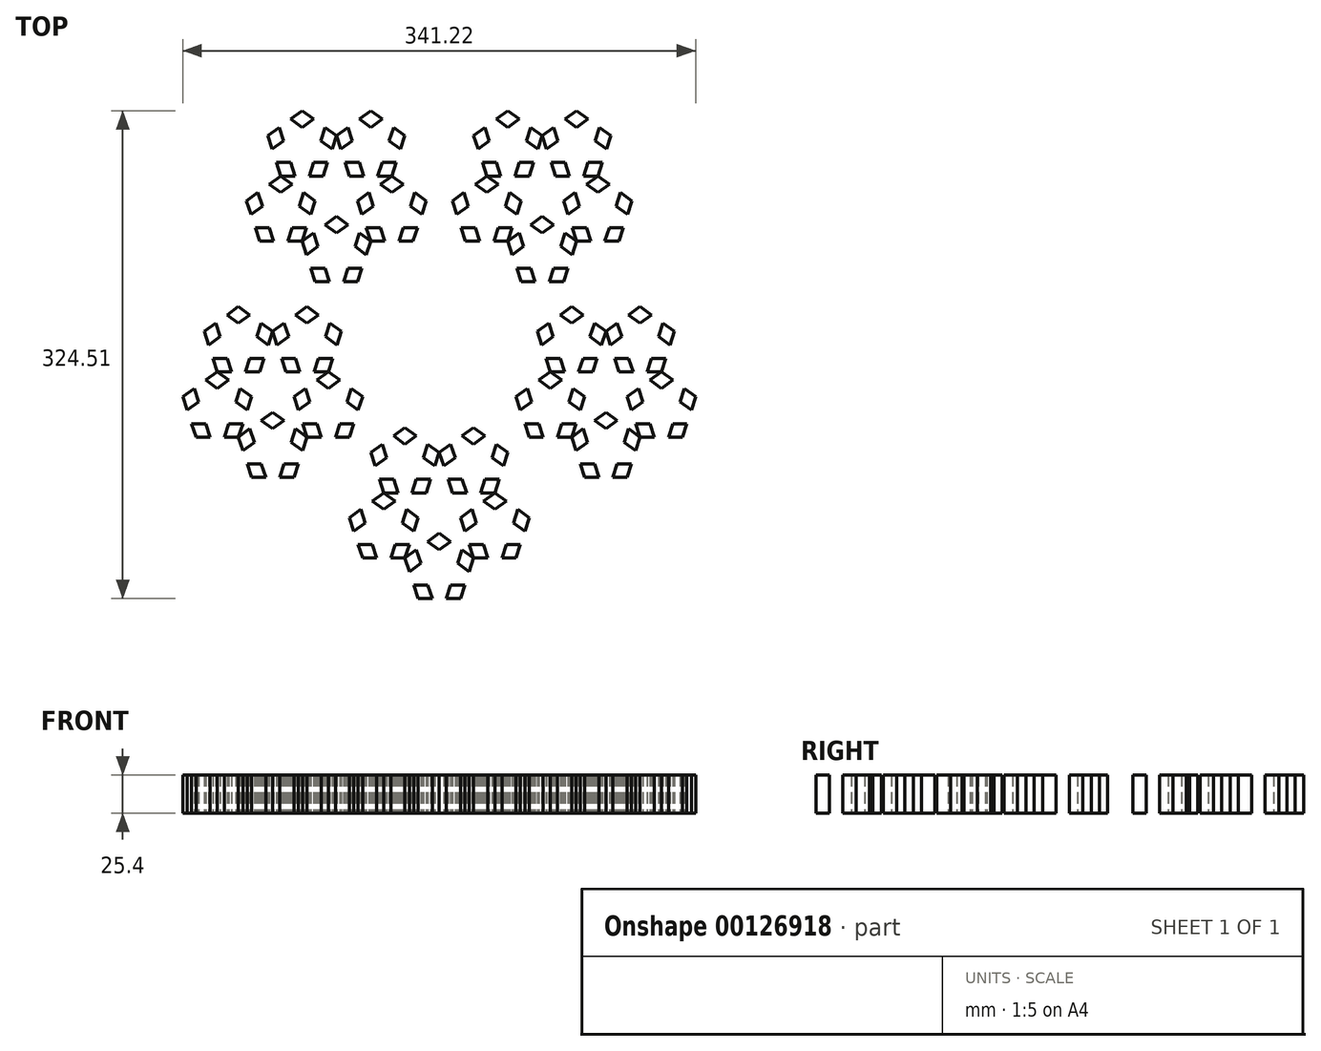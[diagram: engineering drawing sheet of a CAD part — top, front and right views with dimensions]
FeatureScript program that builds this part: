
annotation { "Feature Type Name" : "Feature", "Feature Type Description" : "" }
export const myFeature = defineFeature(function(context is Context, id is Id, definition is map)
    precondition{}
    {
        {
            var Q0;
            Q0=qCreatedBy(makeId("Top.planeOp"),FACE);
            var sketch = newSketch(context, id + "F0", { "sketchPlane" : qUnion([Q0])});
            skLineSegment(sketch, "E0.0", {"start": v(127, -174.8) * mm, "end": v(-127, -174.8) * mm});
            skLineSegment(sketch, "E0.1", {"start": v(-127, -174.8) * mm, "end": v(-205.5, 66.77) * mm});
            skLineSegment(sketch, "E0.2", {"start": v(-205.5, 66.77) * mm, "end": v(0, 216.07) * mm});
            skLineSegment(sketch, "E0.3", {"start": v(0, 216.07) * mm, "end": v(205.5, 66.77) * mm});
            skLineSegment(sketch, "E0.4", {"start": v(205.5, 66.77) * mm, "end": v(127, -174.8) * mm});
            skPoint(sketch, "E0.0.midPoint", {"position": v(0, -174.8) * mm});
            skLineSegment(sketch, "E1.0", {"start": v(42.33, -174.8) * mm, "end": v(-42.33, -174.8) * mm});
            skLineSegment(sketch, "E1.1", {"start": v(-42.33, -174.8) * mm, "end": v(-68.5, -94.28) * mm});
            skLineSegment(sketch, "E1.2", {"start": v(-68.5, -94.28) * mm, "end": v(0, -44.51) * mm});
            skLineSegment(sketch, "E1.3", {"start": v(0, -44.51) * mm, "end": v(68.5, -94.28) * mm});
            skLineSegment(sketch, "E1.4", {"start": v(68.5, -94.28) * mm, "end": v(42.33, -174.8) * mm});
            skLineSegment(sketch, "E2.0", {"start": v(14.11, -174.8) * mm, "end": v(-14.11, -174.8) * mm});
            skLineSegment(sketch, "E2.1", {"start": v(-14.11, -174.8) * mm, "end": v(-22.83, -147.96) * mm});
            skLineSegment(sketch, "E2.2", {"start": v(-22.83, -147.96) * mm, "end": v(0, -131.37) * mm});
            skLineSegment(sketch, "E2.3", {"start": v(0, -131.37) * mm, "end": v(22.83, -147.96) * mm});
            skLineSegment(sketch, "E2.4", {"start": v(22.83, -147.96) * mm, "end": v(14.11, -174.8) * mm});
            skLineSegment(sketch, "E3.0", {"start": v(4.7, -174.8) * mm, "end": v(-4.7, -174.8) * mm});
            skLineSegment(sketch, "E3.1", {"start": v(-4.7, -174.8) * mm, "end": v(-7.61, -165.85) * mm});
            skLineSegment(sketch, "E3.2", {"start": v(-7.61, -165.85) * mm, "end": v(0, -160.32) * mm});
            skLineSegment(sketch, "E3.3", {"start": v(0, -160.32) * mm, "end": v(7.61, -165.85) * mm});
            skLineSegment(sketch, "E3.4", {"start": v(7.61, -165.85) * mm, "end": v(4.7, -174.8) * mm});
            skLineSegment(sketch, "E4.1.0", {"start": v(4.7, -156.9) * mm, "end": v(12.31, -151.38) * mm});
            skLineSegment(sketch, "E4.1.1", {"start": v(19.93, -156.9) * mm, "end": v(17.02, -165.85) * mm});
            skPoint(sketch, "E4.1.2", {"position": v(18.47, -161.38) * mm});
            skLineSegment(sketch, "E4.1.3", {"start": v(17.02, -165.85) * mm, "end": v(7.61, -165.85) * mm});
            skLineSegment(sketch, "E4.1.4", {"start": v(12.31, -151.38) * mm, "end": v(19.93, -156.9) * mm});
            skLineSegment(sketch, "E4.1.5", {"start": v(7.61, -165.85) * mm, "end": v(4.7, -156.9) * mm});
            skPoint(sketch, "E4.1.6", {"position": v(18.47, -161.38) * mm});
            skPoint(sketch, "E4.1.7", {"position": v(18.47, -161.38) * mm});
            skPoint(sketch, "E4.1.8", {"position": v(18.47, -161.38) * mm});
            skLineSegment(sketch, "E4.2.0", {"start": v(2.9, -151.38) * mm, "end": v(0, -142.43) * mm});
            skLineSegment(sketch, "E4.2.1", {"start": v(7.61, -136.9) * mm, "end": v(15.22, -142.43) * mm});
            skPoint(sketch, "E4.2.2", {"position": v(11.42, -139.67) * mm});
            skLineSegment(sketch, "E4.2.3", {"start": v(15.22, -142.43) * mm, "end": v(12.31, -151.38) * mm});
            skLineSegment(sketch, "E4.2.4", {"start": v(0, -142.43) * mm, "end": v(7.61, -136.9) * mm});
            skLineSegment(sketch, "E4.2.5", {"start": v(12.31, -151.38) * mm, "end": v(2.9, -151.38) * mm});
            skPoint(sketch, "E4.2.6", {"position": v(11.42, -139.67) * mm});
            skPoint(sketch, "E4.2.7", {"position": v(11.42, -139.67) * mm});
            skPoint(sketch, "E4.2.8", {"position": v(11.42, -139.67) * mm});
            skLineSegment(sketch, "E4.3.0", {"start": v(-2.9, -151.38) * mm, "end": v(-12.31, -151.38) * mm});
            skLineSegment(sketch, "E4.3.1", {"start": v(-15.22, -142.43) * mm, "end": v(-7.61, -136.9) * mm});
            skPoint(sketch, "E4.3.2", {"position": v(-11.42, -139.67) * mm});
            skLineSegment(sketch, "E4.3.3", {"start": v(-7.61, -136.9) * mm, "end": v(0, -142.43) * mm});
            skLineSegment(sketch, "E4.3.4", {"start": v(-12.31, -151.38) * mm, "end": v(-15.22, -142.43) * mm});
            skLineSegment(sketch, "E4.3.5", {"start": v(0, -142.43) * mm, "end": v(-2.9, -151.38) * mm});
            skPoint(sketch, "E4.3.6", {"position": v(-11.42, -139.67) * mm});
            skPoint(sketch, "E4.3.7", {"position": v(-11.42, -139.67) * mm});
            skPoint(sketch, "E4.3.8", {"position": v(-11.42, -139.67) * mm});
            skLineSegment(sketch, "E4.4.0", {"start": v(-4.7, -156.9) * mm, "end": v(-7.61, -165.85) * mm});
            skLineSegment(sketch, "E4.4.1", {"start": v(-17.02, -165.85) * mm, "end": v(-19.93, -156.9) * mm});
            skPoint(sketch, "E4.4.2", {"position": v(-18.47, -161.38) * mm});
            skLineSegment(sketch, "E4.4.3", {"start": v(-19.93, -156.9) * mm, "end": v(-12.31, -151.38) * mm});
            skLineSegment(sketch, "E4.4.4", {"start": v(-7.61, -165.85) * mm, "end": v(-17.02, -165.85) * mm});
            skLineSegment(sketch, "E4.4.5", {"start": v(-12.31, -151.38) * mm, "end": v(-4.7, -156.9) * mm});
            skPoint(sketch, "E4.4.6", {"position": v(-18.47, -161.38) * mm});
            skPoint(sketch, "E4.4.7", {"position": v(-18.47, -161.38) * mm});
            skPoint(sketch, "E4.4.8", {"position": v(-18.47, -161.38) * mm});
            skPoint(sketch, "E4.center", {"position": v(0, -155.38) * mm});
            skLineSegment(sketch, "E5.1.0", {"start": v(34.04, -124.54) * mm, "end": v(24.63, -124.54) * mm});
            skLineSegment(sketch, "E5.1.1", {"start": v(44.55, -139.01) * mm, "end": v(41.65, -147.96) * mm});
            skLineSegment(sketch, "E5.1.2", {"start": v(52.16, -115.59) * mm, "end": v(49.26, -124.54) * mm});
            skLineSegment(sketch, "E5.1.3", {"start": v(24.63, -124.54) * mm, "end": v(32.24, -130.07) * mm});
            skLineSegment(sketch, "E5.1.4", {"start": v(41.65, -130.07) * mm, "end": v(49.26, -124.54) * mm});
            skLineSegment(sketch, "E5.1.5", {"start": v(32.24, -130.07) * mm, "end": v(29.33, -139.01) * mm});
            skLineSegment(sketch, "E5.1.6", {"start": v(36.94, -104.53) * mm, "end": v(59.78, -121.12) * mm});
            skLineSegment(sketch, "E5.1.7", {"start": v(39.85, -124.54) * mm, "end": v(36.94, -115.59) * mm});
            skLineSegment(sketch, "E5.1.8", {"start": v(29.33, -139.01) * mm, "end": v(36.94, -133.48) * mm});
            skPoint(sketch, "E5.1.9", {"position": v(18.47, -134.54) * mm});
            skPoint(sketch, "E5.1.10", {"position": v(48.36, -112.82) * mm});
            skPoint(sketch, "E5.1.11", {"position": v(55.42, -134.54) * mm});
            skLineSegment(sketch, "E5.1.12", {"start": v(53.96, -139.01) * mm, "end": v(44.55, -139.01) * mm});
            skLineSegment(sketch, "E5.1.13", {"start": v(22.83, -147.96) * mm, "end": v(14.11, -121.12) * mm});
            skLineSegment(sketch, "E5.1.14", {"start": v(29.33, -139.01) * mm, "end": v(19.93, -139.01) * mm});
            skLineSegment(sketch, "E5.1.15", {"start": v(14.11, -121.12) * mm, "end": v(36.94, -104.53) * mm});
            skLineSegment(sketch, "E5.1.16", {"start": v(36.94, -133.48) * mm, "end": v(44.55, -139.01) * mm});
            skLineSegment(sketch, "E5.1.17", {"start": v(59.78, -121.12) * mm, "end": v(51.05, -147.96) * mm});
            skLineSegment(sketch, "E5.1.18", {"start": v(56.87, -130.07) * mm, "end": v(53.96, -139.01) * mm});
            skLineSegment(sketch, "E5.1.19", {"start": v(24.63, -124.54) * mm, "end": v(21.72, -115.59) * mm});
            skLineSegment(sketch, "E5.1.20", {"start": v(44.55, -110.06) * mm, "end": v(52.16, -115.59) * mm});
            skLineSegment(sketch, "E5.1.21", {"start": v(17.02, -130.07) * mm, "end": v(24.63, -124.54) * mm});
            skPoint(sketch, "E5.1.22", {"position": v(36.94, -128.54) * mm});
            skLineSegment(sketch, "E5.1.23", {"start": v(36.94, -115.59) * mm, "end": v(34.04, -124.54) * mm});
            skLineSegment(sketch, "E5.1.24", {"start": v(44.55, -139.01) * mm, "end": v(41.65, -130.07) * mm});
            skLineSegment(sketch, "E5.1.25", {"start": v(49.26, -124.54) * mm, "end": v(56.87, -130.07) * mm});
            skLineSegment(sketch, "E5.1.26", {"start": v(29.33, -110.06) * mm, "end": v(36.94, -115.59) * mm});
            skLineSegment(sketch, "E5.1.27", {"start": v(36.94, -115.59) * mm, "end": v(44.55, -110.06) * mm});
            skPoint(sketch, "E5.1.28", {"position": v(36.94, -147.96) * mm});
            skLineSegment(sketch, "E5.1.29", {"start": v(32.24, -147.96) * mm, "end": v(29.33, -139.01) * mm});
            skLineSegment(sketch, "E5.1.30", {"start": v(51.05, -147.96) * mm, "end": v(22.83, -147.96) * mm});
            skPoint(sketch, "E5.1.31", {"position": v(25.53, -112.82) * mm});
            skLineSegment(sketch, "E5.1.32", {"start": v(49.26, -124.54) * mm, "end": v(39.85, -124.54) * mm});
            skPoint(sketch, "E5.1.33", {"position": v(48.36, -112.82) * mm});
            skPoint(sketch, "E5.1.34", {"position": v(36.94, -147.96) * mm});
            skPoint(sketch, "E5.1.35", {"position": v(55.42, -134.54) * mm});
            skPoint(sketch, "E5.1.36", {"position": v(18.47, -134.54) * mm});
            skLineSegment(sketch, "E5.1.37", {"start": v(41.65, -147.96) * mm, "end": v(32.24, -147.96) * mm});
            skPoint(sketch, "E5.1.38", {"position": v(25.53, -112.82) * mm});
            skPoint(sketch, "E5.1.39", {"position": v(48.36, -112.82) * mm});
            skPoint(sketch, "E5.1.40", {"position": v(18.47, -134.54) * mm});
            skPoint(sketch, "E5.1.41", {"position": v(25.53, -112.82) * mm});
            skLineSegment(sketch, "E5.1.42", {"start": v(21.72, -115.59) * mm, "end": v(29.33, -110.06) * mm});
            skLineSegment(sketch, "E5.1.43", {"start": v(19.93, -139.01) * mm, "end": v(17.02, -130.07) * mm});
            skPoint(sketch, "E5.1.44", {"position": v(55.42, -134.54) * mm});
            skPoint(sketch, "E5.1.45", {"position": v(36.94, -147.96) * mm});
            skPoint(sketch, "E5.1.46", {"position": v(36.94, -147.96) * mm});
            skPoint(sketch, "E5.1.47", {"position": v(55.42, -134.54) * mm});
            skPoint(sketch, "E5.1.48", {"position": v(25.53, -112.82) * mm});
            skPoint(sketch, "E5.1.49", {"position": v(18.47, -134.54) * mm});
            skPoint(sketch, "E5.1.50", {"position": v(48.36, -112.82) * mm});
            skLineSegment(sketch, "E5.2.0", {"start": v(18.13, -86.64) * mm, "end": v(15.22, -95.58) * mm});
            skLineSegment(sketch, "E5.2.1", {"start": v(35.15, -81.1) * mm, "end": v(42.76, -86.64) * mm});
            skLineSegment(sketch, "E5.2.2", {"start": v(15.22, -66.63) * mm, "end": v(22.83, -72.16) * mm});
            skLineSegment(sketch, "E5.2.3", {"start": v(15.22, -95.58) * mm, "end": v(22.83, -90.05) * mm});
            skLineSegment(sketch, "E5.2.4", {"start": v(25.74, -81.1) * mm, "end": v(22.83, -72.16) * mm});
            skLineSegment(sketch, "E5.2.5", {"start": v(22.83, -90.05) * mm, "end": v(30.44, -95.58) * mm});
            skLineSegment(sketch, "E5.2.6", {"start": v(0, -77.69) * mm, "end": v(22.83, -61.1) * mm});
            skLineSegment(sketch, "E5.2.7", {"start": v(19.93, -81.1) * mm, "end": v(10.52, -81.1) * mm});
            skLineSegment(sketch, "E5.2.8", {"start": v(30.44, -95.58) * mm, "end": v(27.54, -86.64) * mm});
            skPoint(sketch, "E5.2.9", {"position": v(22.83, -104.53) * mm});
            skPoint(sketch, "E5.2.10", {"position": v(11.42, -69.4) * mm});
            skPoint(sketch, "E5.2.11", {"position": v(34.25, -69.4) * mm});
            skLineSegment(sketch, "E5.2.12", {"start": v(38.05, -72.16) * mm, "end": v(35.15, -81.1) * mm});
            skLineSegment(sketch, "E5.2.13", {"start": v(36.94, -104.53) * mm, "end": v(8.72, -104.53) * mm});
            skLineSegment(sketch, "E5.2.14", {"start": v(30.44, -95.58) * mm, "end": v(27.54, -104.53) * mm});
            skLineSegment(sketch, "E5.2.15", {"start": v(8.72, -104.53) * mm, "end": v(0, -77.69) * mm});
            skLineSegment(sketch, "E5.2.16", {"start": v(27.54, -86.64) * mm, "end": v(35.15, -81.1) * mm});
            skLineSegment(sketch, "E5.2.17", {"start": v(22.83, -61.1) * mm, "end": v(45.66, -77.69) * mm});
            skLineSegment(sketch, "E5.2.18", {"start": v(30.44, -66.63) * mm, "end": v(38.05, -72.16) * mm});
            skLineSegment(sketch, "E5.2.19", {"start": v(15.22, -95.58) * mm, "end": v(5.81, -95.58) * mm});
            skLineSegment(sketch, "E5.2.20", {"start": v(7.61, -72.16) * mm, "end": v(15.22, -66.63) * mm});
            skLineSegment(sketch, "E5.2.21", {"start": v(18.13, -104.53) * mm, "end": v(15.22, -95.58) * mm});
            skPoint(sketch, "E5.2.22", {"position": v(22.83, -85.1) * mm});
            skLineSegment(sketch, "E5.2.23", {"start": v(10.52, -81.1) * mm, "end": v(18.13, -86.64) * mm});
            skLineSegment(sketch, "E5.2.24", {"start": v(35.15, -81.1) * mm, "end": v(25.74, -81.1) * mm});
            skLineSegment(sketch, "E5.2.25", {"start": v(22.83, -72.16) * mm, "end": v(30.44, -66.63) * mm});
            skLineSegment(sketch, "E5.2.26", {"start": v(2.9, -86.64) * mm, "end": v(10.52, -81.1) * mm});
            skLineSegment(sketch, "E5.2.27", {"start": v(10.52, -81.1) * mm, "end": v(7.61, -72.16) * mm});
            skPoint(sketch, "E5.2.28", {"position": v(41.3, -91.1) * mm});
            skLineSegment(sketch, "E5.2.29", {"start": v(39.85, -95.58) * mm, "end": v(30.44, -95.58) * mm});
            skLineSegment(sketch, "E5.2.30", {"start": v(45.66, -77.69) * mm, "end": v(36.94, -104.53) * mm});
            skPoint(sketch, "E5.2.31", {"position": v(4.36, -91.1) * mm});
            skLineSegment(sketch, "E5.2.32", {"start": v(22.83, -72.16) * mm, "end": v(19.93, -81.1) * mm});
            skPoint(sketch, "E5.2.33", {"position": v(11.42, -69.4) * mm});
            skPoint(sketch, "E5.2.34", {"position": v(41.3, -91.1) * mm});
            skPoint(sketch, "E5.2.35", {"position": v(34.25, -69.4) * mm});
            skPoint(sketch, "E5.2.36", {"position": v(22.83, -104.53) * mm});
            skLineSegment(sketch, "E5.2.37", {"start": v(42.76, -86.64) * mm, "end": v(39.85, -95.58) * mm});
            skPoint(sketch, "E5.2.38", {"position": v(4.36, -91.1) * mm});
            skPoint(sketch, "E5.2.39", {"position": v(11.42, -69.4) * mm});
            skPoint(sketch, "E5.2.40", {"position": v(22.83, -104.53) * mm});
            skPoint(sketch, "E5.2.41", {"position": v(4.36, -91.1) * mm});
            skLineSegment(sketch, "E5.2.42", {"start": v(5.81, -95.58) * mm, "end": v(2.9, -86.64) * mm});
            skLineSegment(sketch, "E5.2.43", {"start": v(27.54, -104.53) * mm, "end": v(18.13, -104.53) * mm});
            skPoint(sketch, "E5.2.44", {"position": v(34.25, -69.4) * mm});
            skPoint(sketch, "E5.2.45", {"position": v(41.3, -91.1) * mm});
            skPoint(sketch, "E5.2.46", {"position": v(41.3, -91.1) * mm});
            skPoint(sketch, "E5.2.47", {"position": v(34.25, -69.4) * mm});
            skPoint(sketch, "E5.2.48", {"position": v(4.36, -91.1) * mm});
            skPoint(sketch, "E5.2.49", {"position": v(22.83, -104.53) * mm});
            skPoint(sketch, "E5.2.50", {"position": v(11.42, -69.4) * mm});
            skLineSegment(sketch, "E5.3.0", {"start": v(-22.83, -90.05) * mm, "end": v(-15.22, -95.58) * mm});
            skLineSegment(sketch, "E5.3.1", {"start": v(-22.83, -72.16) * mm, "end": v(-15.22, -66.63) * mm});
            skLineSegment(sketch, "E5.3.2", {"start": v(-42.76, -86.64) * mm, "end": v(-35.15, -81.1) * mm});
            skLineSegment(sketch, "E5.3.3", {"start": v(-15.22, -95.58) * mm, "end": v(-18.13, -86.64) * mm});
            skLineSegment(sketch, "E5.3.4", {"start": v(-25.74, -81.1) * mm, "end": v(-35.15, -81.1) * mm});
            skLineSegment(sketch, "E5.3.5", {"start": v(-18.13, -86.64) * mm, "end": v(-10.52, -81.1) * mm});
            skLineSegment(sketch, "E5.3.6", {"start": v(-36.94, -104.53) * mm, "end": v(-45.66, -77.69) * mm});
            skLineSegment(sketch, "E5.3.7", {"start": v(-27.54, -86.64) * mm, "end": v(-30.44, -95.58) * mm});
            skLineSegment(sketch, "E5.3.8", {"start": v(-10.52, -81.1) * mm, "end": v(-19.93, -81.1) * mm});
            skPoint(sketch, "E5.3.9", {"position": v(-4.36, -91.1) * mm});
            skPoint(sketch, "E5.3.10", {"position": v(-41.3, -91.1) * mm});
            skPoint(sketch, "E5.3.11", {"position": v(-34.25, -69.4) * mm});
            skLineSegment(sketch, "E5.3.12", {"start": v(-30.44, -66.63) * mm, "end": v(-22.83, -72.16) * mm});
            skLineSegment(sketch, "E5.3.13", {"start": v(0, -77.69) * mm, "end": v(-8.72, -104.53) * mm});
            skLineSegment(sketch, "E5.3.14", {"start": v(-10.52, -81.1) * mm, "end": v(-2.9, -86.64) * mm});
            skLineSegment(sketch, "E5.3.15", {"start": v(-8.72, -104.53) * mm, "end": v(-36.94, -104.53) * mm});
            skLineSegment(sketch, "E5.3.16", {"start": v(-19.93, -81.1) * mm, "end": v(-22.83, -72.16) * mm});
            skLineSegment(sketch, "E5.3.17", {"start": v(-45.66, -77.69) * mm, "end": v(-22.83, -61.1) * mm});
            skLineSegment(sketch, "E5.3.18", {"start": v(-38.05, -72.16) * mm, "end": v(-30.44, -66.63) * mm});
            skLineSegment(sketch, "E5.3.19", {"start": v(-15.22, -95.58) * mm, "end": v(-18.13, -104.53) * mm});
            skLineSegment(sketch, "E5.3.20", {"start": v(-39.85, -95.58) * mm, "end": v(-42.76, -86.64) * mm});
            skLineSegment(sketch, "E5.3.21", {"start": v(-5.81, -95.58) * mm, "end": v(-15.22, -95.58) * mm});
            skPoint(sketch, "E5.3.22", {"position": v(-22.83, -85.1) * mm});
            skLineSegment(sketch, "E5.3.23", {"start": v(-30.44, -95.58) * mm, "end": v(-22.83, -90.05) * mm});
            skLineSegment(sketch, "E5.3.24", {"start": v(-22.83, -72.16) * mm, "end": v(-25.74, -81.1) * mm});
            skLineSegment(sketch, "E5.3.25", {"start": v(-35.15, -81.1) * mm, "end": v(-38.05, -72.16) * mm});
            skLineSegment(sketch, "E5.3.26", {"start": v(-27.54, -104.53) * mm, "end": v(-30.44, -95.58) * mm});
            skLineSegment(sketch, "E5.3.27", {"start": v(-30.44, -95.58) * mm, "end": v(-39.85, -95.58) * mm});
            skPoint(sketch, "E5.3.28", {"position": v(-11.42, -69.4) * mm});
            skLineSegment(sketch, "E5.3.29", {"start": v(-7.61, -72.16) * mm, "end": v(-10.52, -81.1) * mm});
            skLineSegment(sketch, "E5.3.30", {"start": v(-22.83, -61.1) * mm, "end": v(0, -77.69) * mm});
            skPoint(sketch, "E5.3.31", {"position": v(-22.83, -104.53) * mm});
            skLineSegment(sketch, "E5.3.32", {"start": v(-35.15, -81.1) * mm, "end": v(-27.54, -86.64) * mm});
            skPoint(sketch, "E5.3.33", {"position": v(-41.3, -91.1) * mm});
            skPoint(sketch, "E5.3.34", {"position": v(-11.42, -69.4) * mm});
            skPoint(sketch, "E5.3.35", {"position": v(-34.25, -69.4) * mm});
            skPoint(sketch, "E5.3.36", {"position": v(-4.36, -91.1) * mm});
            skLineSegment(sketch, "E5.3.37", {"start": v(-15.22, -66.63) * mm, "end": v(-7.61, -72.16) * mm});
            skPoint(sketch, "E5.3.38", {"position": v(-22.83, -104.53) * mm});
            skPoint(sketch, "E5.3.39", {"position": v(-41.3, -91.1) * mm});
            skPoint(sketch, "E5.3.40", {"position": v(-4.36, -91.1) * mm});
            skPoint(sketch, "E5.3.41", {"position": v(-22.83, -104.53) * mm});
            skLineSegment(sketch, "E5.3.42", {"start": v(-18.13, -104.53) * mm, "end": v(-27.54, -104.53) * mm});
            skLineSegment(sketch, "E5.3.43", {"start": v(-2.9, -86.64) * mm, "end": v(-5.81, -95.58) * mm});
            skPoint(sketch, "E5.3.44", {"position": v(-34.25, -69.4) * mm});
            skPoint(sketch, "E5.3.45", {"position": v(-11.42, -69.4) * mm});
            skPoint(sketch, "E5.3.46", {"position": v(-11.42, -69.4) * mm});
            skPoint(sketch, "E5.3.47", {"position": v(-34.25, -69.4) * mm});
            skPoint(sketch, "E5.3.48", {"position": v(-22.83, -104.53) * mm});
            skPoint(sketch, "E5.3.49", {"position": v(-4.36, -91.1) * mm});
            skPoint(sketch, "E5.3.50", {"position": v(-41.3, -91.1) * mm});
            skLineSegment(sketch, "E5.4.0", {"start": v(-32.24, -130.07) * mm, "end": v(-24.63, -124.54) * mm});
            skLineSegment(sketch, "E5.4.1", {"start": v(-49.26, -124.54) * mm, "end": v(-52.16, -115.59) * mm});
            skLineSegment(sketch, "E5.4.2", {"start": v(-41.65, -147.96) * mm, "end": v(-44.55, -139.01) * mm});
            skLineSegment(sketch, "E5.4.3", {"start": v(-24.63, -124.54) * mm, "end": v(-34.04, -124.54) * mm});
            skLineSegment(sketch, "E5.4.4", {"start": v(-41.65, -130.07) * mm, "end": v(-44.55, -139.01) * mm});
            skLineSegment(sketch, "E5.4.5", {"start": v(-34.04, -124.54) * mm, "end": v(-36.94, -115.59) * mm});
            skLineSegment(sketch, "E5.4.6", {"start": v(-22.83, -147.96) * mm, "end": v(-51.05, -147.96) * mm});
            skLineSegment(sketch, "E5.4.7", {"start": v(-36.94, -133.48) * mm, "end": v(-29.33, -139.01) * mm});
            skLineSegment(sketch, "E5.4.8", {"start": v(-36.94, -115.59) * mm, "end": v(-39.85, -124.54) * mm});
            skPoint(sketch, "E5.4.9", {"position": v(-25.53, -112.82) * mm});
            skPoint(sketch, "E5.4.10", {"position": v(-36.94, -147.96) * mm});
            skPoint(sketch, "E5.4.11", {"position": v(-55.42, -134.54) * mm});
            skLineSegment(sketch, "E5.4.12", {"start": v(-56.87, -130.07) * mm, "end": v(-49.26, -124.54) * mm});
            skLineSegment(sketch, "E5.4.13", {"start": v(-36.94, -104.53) * mm, "end": v(-14.11, -121.12) * mm});
            skLineSegment(sketch, "E5.4.14", {"start": v(-36.94, -115.59) * mm, "end": v(-29.33, -110.06) * mm});
            skLineSegment(sketch, "E5.4.15", {"start": v(-14.11, -121.12) * mm, "end": v(-22.83, -147.96) * mm});
            skLineSegment(sketch, "E5.4.16", {"start": v(-39.85, -124.54) * mm, "end": v(-49.26, -124.54) * mm});
            skLineSegment(sketch, "E5.4.17", {"start": v(-51.05, -147.96) * mm, "end": v(-59.78, -121.12) * mm});
            skLineSegment(sketch, "E5.4.18", {"start": v(-53.96, -139.01) * mm, "end": v(-56.87, -130.07) * mm});
            skLineSegment(sketch, "E5.4.19", {"start": v(-24.63, -124.54) * mm, "end": v(-17.02, -130.07) * mm});
            skLineSegment(sketch, "E5.4.20", {"start": v(-32.24, -147.96) * mm, "end": v(-41.65, -147.96) * mm});
            skLineSegment(sketch, "E5.4.21", {"start": v(-21.72, -115.59) * mm, "end": v(-24.63, -124.54) * mm});
            skPoint(sketch, "E5.4.22", {"position": v(-36.94, -128.54) * mm});
            skLineSegment(sketch, "E5.4.23", {"start": v(-29.33, -139.01) * mm, "end": v(-32.24, -130.07) * mm});
            skLineSegment(sketch, "E5.4.24", {"start": v(-49.26, -124.54) * mm, "end": v(-41.65, -130.07) * mm});
            skLineSegment(sketch, "E5.4.25", {"start": v(-44.55, -139.01) * mm, "end": v(-53.96, -139.01) * mm});
            skLineSegment(sketch, "E5.4.26", {"start": v(-19.93, -139.01) * mm, "end": v(-29.33, -139.01) * mm});
            skLineSegment(sketch, "E5.4.27", {"start": v(-29.33, -139.01) * mm, "end": v(-32.24, -147.96) * mm});
            skPoint(sketch, "E5.4.28", {"position": v(-48.36, -112.82) * mm});
            skLineSegment(sketch, "E5.4.29", {"start": v(-44.55, -110.06) * mm, "end": v(-36.94, -115.59) * mm});
            skLineSegment(sketch, "E5.4.30", {"start": v(-59.78, -121.12) * mm, "end": v(-36.94, -104.53) * mm});
            skPoint(sketch, "E5.4.31", {"position": v(-18.47, -134.54) * mm});
            skLineSegment(sketch, "E5.4.32", {"start": v(-44.55, -139.01) * mm, "end": v(-36.94, -133.48) * mm});
            skPoint(sketch, "E5.4.33", {"position": v(-36.94, -147.96) * mm});
            skPoint(sketch, "E5.4.34", {"position": v(-48.36, -112.82) * mm});
            skPoint(sketch, "E5.4.35", {"position": v(-55.42, -134.54) * mm});
            skPoint(sketch, "E5.4.36", {"position": v(-25.53, -112.82) * mm});
            skLineSegment(sketch, "E5.4.37", {"start": v(-52.16, -115.59) * mm, "end": v(-44.55, -110.06) * mm});
            skPoint(sketch, "E5.4.38", {"position": v(-18.47, -134.54) * mm});
            skPoint(sketch, "E5.4.39", {"position": v(-36.94, -147.96) * mm});
            skPoint(sketch, "E5.4.40", {"position": v(-25.53, -112.82) * mm});
            skPoint(sketch, "E5.4.41", {"position": v(-18.47, -134.54) * mm});
            skLineSegment(sketch, "E5.4.42", {"start": v(-17.02, -130.07) * mm, "end": v(-19.93, -139.01) * mm});
            skLineSegment(sketch, "E5.4.43", {"start": v(-29.33, -110.06) * mm, "end": v(-21.72, -115.59) * mm});
            skPoint(sketch, "E5.4.44", {"position": v(-55.42, -134.54) * mm});
            skPoint(sketch, "E5.4.45", {"position": v(-48.36, -112.82) * mm});
            skPoint(sketch, "E5.4.46", {"position": v(-48.36, -112.82) * mm});
            skPoint(sketch, "E5.4.47", {"position": v(-55.42, -134.54) * mm});
            skPoint(sketch, "E5.4.48", {"position": v(-18.47, -134.54) * mm});
            skPoint(sketch, "E5.4.49", {"position": v(-25.53, -112.82) * mm});
            skPoint(sketch, "E5.4.50", {"position": v(-36.94, -147.96) * mm});
            skPoint(sketch, "E5.center", {"position": v(0, -116.53) * mm});
            skPoint(sketch, "E6.1.0", {"position": v(145.08, 11.13) * mm});
            skPoint(sketch, "E6.1.1", {"position": v(55.42, -54.02) * mm});
            skPoint(sketch, "E6.1.2", {"position": v(159.19, -32.3) * mm});
            skPoint(sketch, "E6.1.3", {"position": v(62.47, -32.3) * mm});
            skPoint(sketch, "E6.1.4", {"position": v(99.41, -59.14) * mm});
            skPoint(sketch, "E6.1.5", {"position": v(110.83, -74.86) * mm});
            skPoint(sketch, "E6.1.6", {"position": v(99.41, 11.13) * mm});
            skPoint(sketch, "E6.1.7", {"position": v(73.89, -67.44) * mm});
            skPoint(sketch, "E6.1.8", {"position": v(92.36, -80.86) * mm});
            skPoint(sketch, "E6.1.9", {"position": v(85.3, -32.3) * mm});
            skPoint(sketch, "E6.1.10", {"position": v(129.3, -80.86) * mm});
            skPoint(sketch, "E6.1.11", {"position": v(166.25, -54.02) * mm});
            skPoint(sketch, "E6.1.12", {"position": v(115.2, -10.59) * mm});
            skPoint(sketch, "E6.1.13", {"position": v(147.77, -67.44) * mm});
            skPoint(sketch, "E6.1.14", {"position": v(122.25, -59.14) * mm});
            skPoint(sketch, "E6.1.15", {"position": v(136.36, -32.3) * mm});
            skLineSegment(sketch, "E6.1.16", {"start": v(110.83, 36.01) * mm, "end": v(179.33, -13.75) * mm});
            skPoint(sketch, "E6.1.17", {"position": v(122.25, 11.13) * mm});
            skLineSegment(sketch, "E6.1.18", {"start": v(68.5, -94.28) * mm, "end": v(42.33, -13.75) * mm});
            skPoint(sketch, "E6.1.19", {"position": v(69.53, -10.59) * mm});
            skPoint(sketch, "E6.1.20", {"position": v(110.83, -36.01) * mm});
            skLineSegment(sketch, "E6.1.21", {"start": v(179.33, -13.75) * mm, "end": v(153.16, -94.28) * mm});
            skPoint(sketch, "E6.1.22", {"position": v(133.66, -4.58) * mm});
            skPoint(sketch, "E6.1.23", {"position": v(88, -24) * mm});
            skPoint(sketch, "E6.1.24", {"position": v(133.66, -24) * mm});
            skPoint(sketch, "E6.1.25", {"position": v(110.83, -94.28) * mm});
            skPoint(sketch, "E6.1.26", {"position": v(92.36, -54.02) * mm});
            skLineSegment(sketch, "E6.1.27", {"start": v(153.16, -94.28) * mm, "end": v(68.5, -94.28) * mm});
            skPoint(sketch, "E6.1.28", {"position": v(106.47, -10.59) * mm});
            skPoint(sketch, "E6.1.29", {"position": v(129.3, -54.02) * mm});
            skPoint(sketch, "E6.1.30", {"position": v(152.13, -10.59) * mm});
            skPoint(sketch, "E6.1.31", {"position": v(76.58, 11.13) * mm});
            skLineSegment(sketch, "E6.1.32", {"start": v(42.33, -13.75) * mm, "end": v(110.83, 36.01) * mm});
            skPoint(sketch, "E6.1.33", {"position": v(147.77, -48.01) * mm});
            skPoint(sketch, "E6.1.34", {"position": v(88, -4.58) * mm});
            skPoint(sketch, "E6.1.35", {"position": v(73.89, -48.01) * mm});
            skPoint(sketch, "E6.1.36", {"position": v(88, -24) * mm});
            skPoint(sketch, "E6.1.37", {"position": v(62.47, -32.3) * mm});
            skPoint(sketch, "E6.1.38", {"position": v(106.47, -10.59) * mm});
            skPoint(sketch, "E6.1.39", {"position": v(129.3, -54.02) * mm});
            skPoint(sketch, "E6.1.40", {"position": v(110.83, -94.28) * mm});
            skPoint(sketch, "E6.1.41", {"position": v(145.08, 11.13) * mm});
            skPoint(sketch, "E6.1.42", {"position": v(122.25, -59.14) * mm});
            skPoint(sketch, "E6.1.43", {"position": v(115.2, -10.59) * mm});
            skPoint(sketch, "E6.1.44", {"position": v(159.19, -32.3) * mm});
            skPoint(sketch, "E6.1.45", {"position": v(133.66, -24) * mm});
            skPoint(sketch, "E6.1.46", {"position": v(76.58, 11.13) * mm});
            skPoint(sketch, "E6.1.47", {"position": v(69.53, -10.59) * mm});
            skPoint(sketch, "E6.1.48", {"position": v(73.89, -67.44) * mm});
            skPoint(sketch, "E6.1.49", {"position": v(136.36, -32.3) * mm});
            skPoint(sketch, "E6.1.50", {"position": v(92.36, -54.02) * mm});
            skPoint(sketch, "E6.1.51", {"position": v(99.41, 11.13) * mm});
            skPoint(sketch, "E6.1.52", {"position": v(129.3, -80.86) * mm});
            skPoint(sketch, "E6.1.53", {"position": v(152.13, -10.59) * mm});
            skPoint(sketch, "E6.1.54", {"position": v(85.3, -32.3) * mm});
            skPoint(sketch, "E6.1.55", {"position": v(92.36, -80.86) * mm});
            skPoint(sketch, "E6.1.56", {"position": v(122.25, 11.13) * mm});
            skPoint(sketch, "E6.1.57", {"position": v(99.41, -59.14) * mm});
            skPoint(sketch, "E6.1.58", {"position": v(147.77, -67.44) * mm});
            skPoint(sketch, "E6.1.59", {"position": v(166.25, -54.02) * mm});
            skPoint(sketch, "E6.1.60", {"position": v(55.42, -54.02) * mm});
            skLineSegment(sketch, "E6.1.61", {"start": v(145.98, -0.58) * mm, "end": v(136.57, -0.58) * mm});
            skPoint(sketch, "E6.1.62", {"position": v(129.3, -54.02) * mm});
            skLineSegment(sketch, "E6.1.63", {"start": v(100.31, -0.58) * mm, "end": v(90.9, -0.58) * mm});
            skLineSegment(sketch, "E6.1.64", {"start": v(133.66, 19.42) * mm, "end": v(156.5, 2.83) * mm});
            skLineSegment(sketch, "E6.1.65", {"start": v(110.83, 2.83) * mm, "end": v(133.66, 19.42) * mm});
            skLineSegment(sketch, "E6.1.66", {"start": v(86.2, -44.01) * mm, "end": v(76.8, -44.01) * mm});
            skLineSegment(sketch, "E6.1.67", {"start": v(88, -9.53) * mm, "end": v(95.6, -15.06) * mm});
            skLineSegment(sketch, "E6.1.68", {"start": v(115.53, -76.38) * mm, "end": v(123.14, -70.85) * mm});
            skLineSegment(sketch, "E6.1.69", {"start": v(128.96, -24) * mm, "end": v(126.05, -15.06) * mm});
            skPoint(sketch, "E6.1.70", {"position": v(69.53, -10.59) * mm});
            skLineSegment(sketch, "E6.1.71", {"start": v(73.89, -24) * mm, "end": v(96.72, -40.6) * mm});
            skLineSegment(sketch, "E6.1.72", {"start": v(110.83, 2.83) * mm, "end": v(102.1, -24) * mm});
            skPoint(sketch, "E6.1.73", {"position": v(122.25, 11.13) * mm});
            skPoint(sketch, "E6.1.74", {"position": v(99.41, -59.14) * mm});
            skLineSegment(sketch, "E6.1.75", {"start": v(141.27, -15.06) * mm, "end": v(138.37, -6.11) * mm});
            skLineSegment(sketch, "E6.1.76", {"start": v(51.05, -40.6) * mm, "end": v(73.89, -24) * mm});
            skLineSegment(sketch, "E6.1.77", {"start": v(81.5, -58.49) * mm, "end": v(78.6, -49.54) * mm});
            skLineSegment(sketch, "E6.1.78", {"start": v(66.28, -58.49) * mm, "end": v(73.89, -52.96) * mm});
            skLineSegment(sketch, "E6.1.79", {"start": v(110.83, -79.8) * mm, "end": v(118.44, -85.33) * mm});
            skLineSegment(sketch, "E6.1.80", {"start": v(143.07, -49.54) * mm, "end": v(140.16, -58.49) * mm});
            skLineSegment(sketch, "E6.1.81", {"start": v(98.52, -70.85) * mm, "end": v(106.13, -76.38) * mm});
            skLineSegment(sketch, "E6.1.82", {"start": v(123.14, -70.85) * mm, "end": v(130.76, -76.38) * mm});
            skLineSegment(sketch, "E6.1.83", {"start": v(136.57, -0.58) * mm, "end": v(133.66, 8.36) * mm});
            skLineSegment(sketch, "E6.1.84", {"start": v(90.9, -58.49) * mm, "end": v(81.5, -58.49) * mm});
            skPoint(sketch, "E6.1.85", {"position": v(55.42, -54.02) * mm});
            skLineSegment(sketch, "E6.1.86", {"start": v(76.8, -44.01) * mm, "end": v(73.89, -35.07) * mm});
            skLineSegment(sketch, "E6.1.87", {"start": v(85.1, -0.58) * mm, "end": v(75.68, -0.58) * mm});
            skLineSegment(sketch, "E6.1.88", {"start": v(110.83, -50.85) * mm, "end": v(133.66, -67.44) * mm});
            skLineSegment(sketch, "E6.1.89", {"start": v(140.16, -58.49) * mm, "end": v(147.77, -52.96) * mm});
            skLineSegment(sketch, "E6.1.90", {"start": v(103.22, -85.33) * mm, "end": v(110.83, -79.8) * mm});
            skPoint(sketch, "E6.1.91", {"position": v(62.47, -32.3) * mm});
            skLineSegment(sketch, "E6.1.92", {"start": v(150.68, -15.06) * mm, "end": v(141.27, -15.06) * mm});
            skLineSegment(sketch, "E6.1.93", {"start": v(147.77, -35.07) * mm, "end": v(155.38, -29.54) * mm});
            skPoint(sketch, "E6.1.94", {"position": v(145.08, 11.13) * mm});
            skLineSegment(sketch, "E6.1.95", {"start": v(133.66, -67.44) * mm, "end": v(124.94, -94.28) * mm});
            skLineSegment(sketch, "E6.1.96", {"start": v(88, 19.42) * mm, "end": v(110.83, 2.83) * mm});
            skLineSegment(sketch, "E6.1.97", {"start": v(110.83, -61.9) * mm, "end": v(107.92, -70.85) * mm});
            skLineSegment(sketch, "E6.1.98", {"start": v(123.14, -70.85) * mm, "end": v(113.74, -70.85) * mm});
            skLineSegment(sketch, "E6.1.99", {"start": v(143.07, -67.44) * mm, "end": v(140.16, -58.49) * mm});
            skLineSegment(sketch, "E6.1.100", {"start": v(138.37, -6.11) * mm, "end": v(145.98, -0.58) * mm});
            skPoint(sketch, "E6.1.101", {"position": v(110.83, -94.28) * mm});
            skPoint(sketch, "E6.1.102", {"position": v(129.3, -80.86) * mm});
            skLineSegment(sketch, "E6.1.103", {"start": v(133.66, -9.53) * mm, "end": v(141.27, -15.06) * mm});
            skLineSegment(sketch, "E6.1.104", {"start": v(147.77, -35.07) * mm, "end": v(144.87, -44.01) * mm});
            skLineSegment(sketch, "E6.1.105", {"start": v(121.35, -0.58) * mm, "end": v(128.96, -6.11) * mm});
            skPoint(sketch, "E6.1.106", {"position": v(152.13, -10.59) * mm});
            skPoint(sketch, "E6.1.107", {"position": v(136.36, -32.3) * mm});
            skLineSegment(sketch, "E6.1.108", {"start": v(96.72, -40.6) * mm, "end": v(88, -67.44) * mm});
            skPoint(sketch, "E6.1.109", {"position": v(159.19, -32.3) * mm});
            skPoint(sketch, "E6.1.110", {"position": v(106.47, -10.59) * mm});
            skLineSegment(sketch, "E6.1.111", {"start": v(78.6, -49.54) * mm, "end": v(86.2, -44.01) * mm});
            skLineSegment(sketch, "E6.1.112", {"start": v(170.6, -40.6) * mm, "end": v(161.88, -67.44) * mm});
            skLineSegment(sketch, "E6.1.113", {"start": v(144.87, -44.01) * mm, "end": v(135.46, -44.01) * mm});
            skLineSegment(sketch, "E6.1.114", {"start": v(90.9, -0.58) * mm, "end": v(88, 8.36) * mm});
            skLineSegment(sketch, "E6.1.115", {"start": v(80.39, -15.06) * mm, "end": v(88, -9.53) * mm});
            skLineSegment(sketch, "E6.1.116", {"start": v(65.17, 2.83) * mm, "end": v(88, 19.42) * mm});
            skLineSegment(sketch, "E6.1.117", {"start": v(150.68, -44.01) * mm, "end": v(147.77, -35.07) * mm});
            skLineSegment(sketch, "E6.1.118", {"start": v(130.76, -0.58) * mm, "end": v(121.35, -0.58) * mm});
            skLineSegment(sketch, "E6.1.119", {"start": v(124.94, -94.28) * mm, "end": v(96.72, -94.28) * mm});
            skLineSegment(sketch, "E6.1.120", {"start": v(147.77, -52.96) * mm, "end": v(155.38, -58.49) * mm});
            skLineSegment(sketch, "E6.1.121", {"start": v(88, 8.36) * mm, "end": v(85.1, -0.58) * mm});
            skLineSegment(sketch, "E6.1.122", {"start": v(69.18, -49.54) * mm, "end": v(66.28, -58.49) * mm});
            skLineSegment(sketch, "E6.1.123", {"start": v(160.09, -44.01) * mm, "end": v(150.68, -44.01) * mm});
            skLineSegment(sketch, "E6.1.124", {"start": v(61.57, -44.01) * mm, "end": v(69.18, -49.54) * mm});
            skLineSegment(sketch, "E6.1.125", {"start": v(88, -67.44) * mm, "end": v(59.78, -67.44) * mm});
            skLineSegment(sketch, "E6.1.126", {"start": v(128.96, -6.11) * mm, "end": v(126.05, -15.06) * mm});
            skPoint(sketch, "E6.1.127", {"position": v(76.58, 11.13) * mm});
            skLineSegment(sketch, "E6.1.128", {"start": v(124.94, -40.6) * mm, "end": v(147.77, -24) * mm});
            skLineSegment(sketch, "E6.1.129", {"start": v(147.77, -24) * mm, "end": v(170.6, -40.6) * mm});
            skLineSegment(sketch, "E6.1.130", {"start": v(106.13, -94.28) * mm, "end": v(103.22, -85.33) * mm});
            skPoint(sketch, "E6.1.131", {"position": v(73.89, -67.44) * mm});
            skLineSegment(sketch, "E6.1.132", {"start": v(96.72, -94.28) * mm, "end": v(88, -67.44) * mm});
            skLineSegment(sketch, "E6.1.133", {"start": v(161.88, -67.44) * mm, "end": v(133.66, -67.44) * mm});
            skLineSegment(sketch, "E6.1.134", {"start": v(106.13, -76.38) * mm, "end": v(103.22, -85.33) * mm});
            skLineSegment(sketch, "E6.1.135", {"start": v(160.09, -44.01) * mm, "end": v(167.7, -49.54) * mm});
            skPoint(sketch, "E6.1.136", {"position": v(92.36, -80.86) * mm});
            skLineSegment(sketch, "E6.1.137", {"start": v(75.68, -0.58) * mm, "end": v(83.3, -6.11) * mm});
            skLineSegment(sketch, "E6.1.138", {"start": v(107.92, -70.85) * mm, "end": v(98.52, -70.85) * mm});
            skLineSegment(sketch, "E6.1.139", {"start": v(119.55, -24) * mm, "end": v(110.83, 2.83) * mm});
            skLineSegment(sketch, "E6.1.140", {"start": v(133.66, -67.44) * mm, "end": v(124.94, -40.6) * mm});
            skLineSegment(sketch, "E6.1.141", {"start": v(95.6, -15.06) * mm, "end": v(92.7, -6.11) * mm});
            skPoint(sketch, "E6.1.142", {"position": v(88, -24) * mm});
            skPoint(sketch, "E6.1.143", {"position": v(92.36, -54.02) * mm});
            skLineSegment(sketch, "E6.1.144", {"start": v(92.7, -6.11) * mm, "end": v(100.31, -0.58) * mm});
            skLineSegment(sketch, "E6.1.145", {"start": v(88, -67.44) * mm, "end": v(110.83, -50.85) * mm});
            skLineSegment(sketch, "E6.1.146", {"start": v(73.89, -52.96) * mm, "end": v(81.5, -58.49) * mm});
            skLineSegment(sketch, "E6.1.147", {"start": v(118.44, -85.33) * mm, "end": v(115.53, -76.38) * mm});
            skLineSegment(sketch, "E6.1.148", {"start": v(73.89, -24) * mm, "end": v(65.17, 2.83) * mm});
            skLineSegment(sketch, "E6.1.149", {"start": v(126.05, -15.06) * mm, "end": v(133.66, -9.53) * mm});
            skLineSegment(sketch, "E6.1.150", {"start": v(83.3, -24) * mm, "end": v(80.39, -15.06) * mm});
            skLineSegment(sketch, "E6.1.151", {"start": v(73.89, -35.07) * mm, "end": v(70.98, -44.01) * mm});
            skLineSegment(sketch, "E6.1.152", {"start": v(59.78, -67.44) * mm, "end": v(51.05, -40.6) * mm});
            skLineSegment(sketch, "E6.1.153", {"start": v(113.74, -70.85) * mm, "end": v(110.83, -61.9) * mm});
            skLineSegment(sketch, "E6.1.154", {"start": v(110.83, -61.9) * mm, "end": v(118.44, -56.38) * mm});
            skLineSegment(sketch, "E6.1.155", {"start": v(135.46, -44.01) * mm, "end": v(143.07, -49.54) * mm});
            skLineSegment(sketch, "E6.1.156", {"start": v(147.77, -24) * mm, "end": v(119.55, -24) * mm});
            skLineSegment(sketch, "E6.1.157", {"start": v(133.66, 8.36) * mm, "end": v(130.76, -0.58) * mm});
            skLineSegment(sketch, "E6.1.158", {"start": v(102.1, -24) * mm, "end": v(73.89, -24) * mm});
            skLineSegment(sketch, "E6.1.159", {"start": v(133.66, 8.36) * mm, "end": v(141.27, 13.9) * mm});
            skLineSegment(sketch, "E6.1.160", {"start": v(83.3, -6.11) * mm, "end": v(80.39, -15.06) * mm});
            skLineSegment(sketch, "E6.1.161", {"start": v(152.48, -49.54) * mm, "end": v(160.09, -44.01) * mm});
            skPoint(sketch, "E6.1.162", {"position": v(85.3, -32.3) * mm});
            skPoint(sketch, "E6.1.163", {"position": v(115.2, -10.59) * mm});
            skLineSegment(sketch, "E6.1.164", {"start": v(70.98, -44.01) * mm, "end": v(61.57, -44.01) * mm});
            skLineSegment(sketch, "E6.1.165", {"start": v(156.5, 2.83) * mm, "end": v(147.77, -24) * mm});
            skLineSegment(sketch, "E6.1.166", {"start": v(100.31, -0.58) * mm, "end": v(107.92, -6.11) * mm});
            skPoint(sketch, "E6.1.167", {"position": v(122.25, -59.14) * mm});
            skLineSegment(sketch, "E6.1.168", {"start": v(155.38, -58.49) * mm, "end": v(152.48, -49.54) * mm});
            skPoint(sketch, "E6.1.169", {"position": v(147.77, -67.44) * mm});
            skPoint(sketch, "E6.1.170", {"position": v(133.66, -24) * mm});
            skPoint(sketch, "E6.1.171", {"position": v(99.41, 11.13) * mm});
            skPoint(sketch, "E6.1.172", {"position": v(166.25, -54.02) * mm});
            skPoint(sketch, "E6.1.173", {"position": v(92.36, -80.86) * mm});
            skPoint(sketch, "E6.1.174", {"position": v(88, -24) * mm});
            skPoint(sketch, "E6.1.175", {"position": v(166.25, -54.02) * mm});
            skPoint(sketch, "E6.1.176", {"position": v(85.3, -32.3) * mm});
            skPoint(sketch, "E6.1.177", {"position": v(62.47, -32.3) * mm});
            skPoint(sketch, "E6.1.178", {"position": v(147.77, -67.44) * mm});
            skPoint(sketch, "E6.1.179", {"position": v(122.25, -59.14) * mm});
            skPoint(sketch, "E6.1.180", {"position": v(73.89, -67.44) * mm});
            skPoint(sketch, "E6.1.181", {"position": v(133.66, -24) * mm});
            skPoint(sketch, "E6.1.182", {"position": v(115.2, -10.59) * mm});
            skPoint(sketch, "E6.1.183", {"position": v(122.25, 11.13) * mm});
            skPoint(sketch, "E6.1.184", {"position": v(129.3, -80.86) * mm});
            skPoint(sketch, "E6.1.185", {"position": v(99.41, 11.13) * mm});
            skPoint(sketch, "E6.1.186", {"position": v(69.53, -10.59) * mm});
            skPoint(sketch, "E6.1.187", {"position": v(136.36, -32.3) * mm});
            skPoint(sketch, "E6.1.188", {"position": v(159.19, -32.3) * mm});
            skPoint(sketch, "E6.1.189", {"position": v(152.13, -10.59) * mm});
            skPoint(sketch, "E6.1.190", {"position": v(55.42, -54.02) * mm});
            skPoint(sketch, "E6.1.191", {"position": v(99.41, -59.14) * mm});
            skPoint(sketch, "E6.1.192", {"position": v(129.3, -54.02) * mm});
            skPoint(sketch, "E6.1.193", {"position": v(145.08, 11.13) * mm});
            skPoint(sketch, "E6.1.194", {"position": v(106.47, -10.59) * mm});
            skPoint(sketch, "E6.1.195", {"position": v(110.83, -94.28) * mm});
            skPoint(sketch, "E6.1.196", {"position": v(76.58, 11.13) * mm});
            skPoint(sketch, "E6.1.197", {"position": v(92.36, -54.02) * mm});
            skLineSegment(sketch, "E6.1.198", {"start": v(80.39, -15.06) * mm, "end": v(70.98, -15.06) * mm});
            skLineSegment(sketch, "E6.1.199", {"start": v(70.98, -15.06) * mm, "end": v(68.07, -6.11) * mm});
            skLineSegment(sketch, "E6.1.200", {"start": v(127.85, -49.54) * mm, "end": v(135.46, -44.01) * mm});
            skLineSegment(sketch, "E6.1.201", {"start": v(113.74, -6.11) * mm, "end": v(121.35, -0.58) * mm});
            skLineSegment(sketch, "E6.1.202", {"start": v(80.39, 13.9) * mm, "end": v(88, 8.36) * mm});
            skLineSegment(sketch, "E6.1.203", {"start": v(141.27, 13.9) * mm, "end": v(148.88, 8.36) * mm});
            skLineSegment(sketch, "E6.1.204", {"start": v(89.1, -35.07) * mm, "end": v(86.2, -44.01) * mm});
            skLineSegment(sketch, "E6.1.205", {"start": v(88, 8.36) * mm, "end": v(95.6, 13.9) * mm});
            skLineSegment(sketch, "E6.1.206", {"start": v(95.6, -15.06) * mm, "end": v(92.7, -24) * mm});
            skLineSegment(sketch, "E6.1.207", {"start": v(132.55, -35.07) * mm, "end": v(140.16, -29.54) * mm});
            skLineSegment(sketch, "E6.1.208", {"start": v(121.35, -0.58) * mm, "end": v(118.44, 8.36) * mm});
            skLineSegment(sketch, "E6.1.209", {"start": v(93.81, -85.33) * mm, "end": v(90.9, -76.38) * mm});
            skLineSegment(sketch, "E6.1.210", {"start": v(164.8, -58.49) * mm, "end": v(155.38, -58.49) * mm});
            skLineSegment(sketch, "E6.1.211", {"start": v(126.05, 13.9) * mm, "end": v(133.66, 8.36) * mm});
            skLineSegment(sketch, "E6.1.212", {"start": v(118.44, -85.33) * mm, "end": v(115.53, -94.28) * mm});
            skLineSegment(sketch, "E6.1.213", {"start": v(118.44, -56.38) * mm, "end": v(126.05, -61.9) * mm});
            skLineSegment(sketch, "E6.1.214", {"start": v(95.6, -61.9) * mm, "end": v(103.22, -56.38) * mm});
            skLineSegment(sketch, "E6.1.215", {"start": v(163, -35.07) * mm, "end": v(160.09, -44.01) * mm});
            skLineSegment(sketch, "E6.1.216", {"start": v(53.96, -49.54) * mm, "end": v(61.57, -44.01) * mm});
            skLineSegment(sketch, "E6.1.217", {"start": v(69.18, -67.44) * mm, "end": v(66.28, -58.49) * mm});
            skLineSegment(sketch, "E6.1.218", {"start": v(90.9, -76.38) * mm, "end": v(98.52, -70.85) * mm});
            skLineSegment(sketch, "E6.1.219", {"start": v(103.22, 8.36) * mm, "end": v(100.31, -0.58) * mm});
            skLineSegment(sketch, "E6.1.220", {"start": v(155.38, -58.49) * mm, "end": v(152.48, -67.44) * mm});
            skLineSegment(sketch, "E6.1.221", {"start": v(145.98, -0.58) * mm, "end": v(153.59, -6.11) * mm});
            skLineSegment(sketch, "E6.1.222", {"start": v(61.57, -44.01) * mm, "end": v(58.67, -35.07) * mm});
            skLineSegment(sketch, "E6.1.223", {"start": v(78.6, -67.44) * mm, "end": v(69.18, -67.44) * mm});
            skLineSegment(sketch, "E6.1.224", {"start": v(73.89, -35.07) * mm, "end": v(81.5, -29.54) * mm});
            skLineSegment(sketch, "E6.1.225", {"start": v(138.37, -24) * mm, "end": v(128.96, -24) * mm});
            skLineSegment(sketch, "E6.1.226", {"start": v(72.78, 8.36) * mm, "end": v(80.39, 13.9) * mm});
            skLineSegment(sketch, "E6.1.227", {"start": v(155.38, -29.54) * mm, "end": v(163, -35.07) * mm});
            skLineSegment(sketch, "E6.1.228", {"start": v(58.67, -35.07) * mm, "end": v(66.28, -29.54) * mm});
            skLineSegment(sketch, "E6.1.229", {"start": v(86.2, -44.01) * mm, "end": v(93.81, -49.54) * mm});
            skLineSegment(sketch, "E6.1.230", {"start": v(105.02, -15.06) * mm, "end": v(95.6, -15.06) * mm});
            skLineSegment(sketch, "E6.1.231", {"start": v(93.81, -49.54) * mm, "end": v(90.9, -58.49) * mm});
            skLineSegment(sketch, "E6.1.232", {"start": v(130.76, -58.49) * mm, "end": v(127.85, -49.54) * mm});
            skLineSegment(sketch, "E6.1.233", {"start": v(126.05, -61.9) * mm, "end": v(123.14, -70.85) * mm});
            skLineSegment(sketch, "E6.1.234", {"start": v(68.07, -6.11) * mm, "end": v(75.68, -0.58) * mm});
            skLineSegment(sketch, "E6.1.235", {"start": v(153.59, -6.11) * mm, "end": v(150.68, -15.06) * mm});
            skLineSegment(sketch, "E6.1.236", {"start": v(141.27, -15.06) * mm, "end": v(138.37, -24) * mm});
            skLineSegment(sketch, "E6.1.237", {"start": v(130.76, -76.38) * mm, "end": v(127.85, -85.33) * mm});
            skLineSegment(sketch, "E6.1.238", {"start": v(103.22, -85.33) * mm, "end": v(93.81, -85.33) * mm});
            skLineSegment(sketch, "E6.1.239", {"start": v(56.87, -58.49) * mm, "end": v(53.96, -49.54) * mm});
            skLineSegment(sketch, "E6.1.240", {"start": v(107.92, -6.11) * mm, "end": v(105.02, -15.06) * mm});
            skLineSegment(sketch, "E6.1.241", {"start": v(98.52, -70.85) * mm, "end": v(95.6, -61.9) * mm});
            skLineSegment(sketch, "E6.1.242", {"start": v(126.05, -15.06) * mm, "end": v(116.64, -15.06) * mm});
            skLineSegment(sketch, "E6.1.243", {"start": v(167.7, -49.54) * mm, "end": v(164.8, -58.49) * mm});
            skLineSegment(sketch, "E6.1.244", {"start": v(116.64, -15.06) * mm, "end": v(113.74, -6.11) * mm});
            skLineSegment(sketch, "E6.1.245", {"start": v(127.85, -85.33) * mm, "end": v(118.44, -85.33) * mm});
            skLineSegment(sketch, "E6.1.246", {"start": v(152.48, -67.44) * mm, "end": v(143.07, -67.44) * mm});
            skLineSegment(sketch, "E6.1.247", {"start": v(118.44, 8.36) * mm, "end": v(126.05, 13.9) * mm});
            skLineSegment(sketch, "E6.1.248", {"start": v(103.22, -56.38) * mm, "end": v(110.83, -61.9) * mm});
            skLineSegment(sketch, "E6.1.249", {"start": v(75.68, -0.58) * mm, "end": v(72.78, 8.36) * mm});
            skLineSegment(sketch, "E6.1.250", {"start": v(81.5, -58.49) * mm, "end": v(78.6, -67.44) * mm});
            skLineSegment(sketch, "E6.1.251", {"start": v(140.16, -29.54) * mm, "end": v(147.77, -35.07) * mm});
            skLineSegment(sketch, "E6.1.252", {"start": v(66.28, -29.54) * mm, "end": v(73.89, -35.07) * mm});
            skLineSegment(sketch, "E6.1.253", {"start": v(66.28, -58.49) * mm, "end": v(56.87, -58.49) * mm});
            skLineSegment(sketch, "E6.1.254", {"start": v(135.46, -44.01) * mm, "end": v(132.55, -35.07) * mm});
            skLineSegment(sketch, "E6.1.255", {"start": v(92.7, -24) * mm, "end": v(83.3, -24) * mm});
            skLineSegment(sketch, "E6.1.256", {"start": v(95.6, 13.9) * mm, "end": v(103.22, 8.36) * mm});
            skLineSegment(sketch, "E6.1.257", {"start": v(81.5, -29.54) * mm, "end": v(89.1, -35.07) * mm});
            skLineSegment(sketch, "E6.1.258", {"start": v(115.53, -94.28) * mm, "end": v(106.13, -94.28) * mm});
            skLineSegment(sketch, "E6.1.259", {"start": v(140.16, -58.49) * mm, "end": v(130.76, -58.49) * mm});
            skLineSegment(sketch, "E6.1.260", {"start": v(148.88, 8.36) * mm, "end": v(145.98, -0.58) * mm});
            skPoint(sketch, "E6.2.0", {"position": v(34.25, 141.42) * mm});
            skPoint(sketch, "E6.2.1", {"position": v(68.5, 36.01) * mm});
            skPoint(sketch, "E6.2.2", {"position": v(79.91, 141.42) * mm});
            skPoint(sketch, "E6.2.3", {"position": v(50.03, 49.43) * mm});
            skPoint(sketch, "E6.2.4", {"position": v(86.97, 76.27) * mm});
            skPoint(sketch, "E6.2.5", {"position": v(105.44, 82.27) * mm});
            skPoint(sketch, "E6.2.6", {"position": v(20.14, 97.99) * mm});
            skPoint(sketch, "E6.2.7", {"position": v(86.97, 49.43) * mm});
            skPoint(sketch, "E6.2.8", {"position": v(105.44, 62.85) * mm});
            skPoint(sketch, "E6.2.9", {"position": v(57.08, 71.15) * mm});
            skPoint(sketch, "E6.2.10", {"position": v(116.86, 97.99) * mm});
            skPoint(sketch, "E6.2.11", {"position": v(102.75, 141.42) * mm});
            skPoint(sketch, "E6.2.12", {"position": v(45.66, 106.28) * mm});
            skPoint(sketch, "E6.2.13", {"position": v(109.8, 119.7) * mm});
            skPoint(sketch, "E6.2.14", {"position": v(94.02, 97.99) * mm});
            skPoint(sketch, "E6.2.15", {"position": v(72.86, 119.7) * mm});
            skLineSegment(sketch, "E6.2.16", {"start": v(0, 116.53) * mm, "end": v(68.5, 166.3) * mm});
            skPoint(sketch, "E6.2.17", {"position": v(27.2, 119.7) * mm});
            skLineSegment(sketch, "E6.2.18", {"start": v(110.83, 36.01) * mm, "end": v(26.16, 36.01) * mm});
            skPoint(sketch, "E6.2.19", {"position": v(31.55, 62.85) * mm});
            skPoint(sketch, "E6.2.20", {"position": v(68.5, 94.28) * mm});
            skLineSegment(sketch, "E6.2.21", {"start": v(68.5, 166.3) * mm, "end": v(137, 116.53) * mm});
            skPoint(sketch, "E6.2.22", {"position": v(45.66, 125.7) * mm});
            skPoint(sketch, "E6.2.23", {"position": v(50.03, 76.27) * mm});
            skPoint(sketch, "E6.2.24", {"position": v(64.14, 119.7) * mm});
            skPoint(sketch, "E6.2.25", {"position": v(123.91, 76.27) * mm});
            skPoint(sketch, "E6.2.26", {"position": v(79.91, 71.15) * mm});
            skLineSegment(sketch, "E6.2.27", {"start": v(137, 116.53) * mm, "end": v(110.83, 36.01) * mm});
            skPoint(sketch, "E6.2.28", {"position": v(42.97, 97.99) * mm});
            skPoint(sketch, "E6.2.29", {"position": v(91.33, 106.28) * mm});
            skPoint(sketch, "E6.2.30", {"position": v(57.08, 141.42) * mm});
            skPoint(sketch, "E6.2.31", {"position": v(13.08, 76.27) * mm});
            skLineSegment(sketch, "E6.2.32", {"start": v(26.16, 36.01) * mm, "end": v(0, 116.53) * mm});
            skPoint(sketch, "E6.2.33", {"position": v(91.33, 125.7) * mm});
            skPoint(sketch, "E6.2.34", {"position": v(31.55, 82.27) * mm});
            skPoint(sketch, "E6.2.35", {"position": v(68.5, 55.43) * mm});
            skPoint(sketch, "E6.2.36", {"position": v(50.03, 76.27) * mm});
            skPoint(sketch, "E6.2.37", {"position": v(50.03, 49.43) * mm});
            skPoint(sketch, "E6.2.38", {"position": v(42.97, 97.99) * mm});
            skPoint(sketch, "E6.2.39", {"position": v(91.33, 106.28) * mm});
            skPoint(sketch, "E6.2.40", {"position": v(123.91, 76.27) * mm});
            skPoint(sketch, "E6.2.41", {"position": v(34.25, 141.42) * mm});
            skPoint(sketch, "E6.2.42", {"position": v(94.02, 97.99) * mm});
            skPoint(sketch, "E6.2.43", {"position": v(45.66, 106.28) * mm});
            skPoint(sketch, "E6.2.44", {"position": v(79.91, 141.42) * mm});
            skPoint(sketch, "E6.2.45", {"position": v(64.14, 119.7) * mm});
            skPoint(sketch, "E6.2.46", {"position": v(13.08, 76.27) * mm});
            skPoint(sketch, "E6.2.47", {"position": v(31.55, 62.85) * mm});
            skPoint(sketch, "E6.2.48", {"position": v(86.97, 49.43) * mm});
            skPoint(sketch, "E6.2.49", {"position": v(72.86, 119.7) * mm});
            skPoint(sketch, "E6.2.50", {"position": v(79.91, 71.15) * mm});
            skPoint(sketch, "E6.2.51", {"position": v(20.14, 97.99) * mm});
            skPoint(sketch, "E6.2.52", {"position": v(116.86, 97.99) * mm});
            skPoint(sketch, "E6.2.53", {"position": v(57.08, 141.42) * mm});
            skPoint(sketch, "E6.2.54", {"position": v(57.08, 71.15) * mm});
            skPoint(sketch, "E6.2.55", {"position": v(105.44, 62.85) * mm});
            skPoint(sketch, "E6.2.56", {"position": v(27.2, 119.7) * mm});
            skPoint(sketch, "E6.2.57", {"position": v(86.97, 76.27) * mm});
            skPoint(sketch, "E6.2.58", {"position": v(109.8, 119.7) * mm});
            skPoint(sketch, "E6.2.59", {"position": v(102.75, 141.42) * mm});
            skPoint(sketch, "E6.2.60", {"position": v(68.5, 36.01) * mm});
            skLineSegment(sketch, "E6.2.61", {"start": v(45.66, 138.65) * mm, "end": v(42.76, 129.7) * mm});
            skPoint(sketch, "E6.2.62", {"position": v(91.33, 106.28) * mm});
            skLineSegment(sketch, "E6.2.63", {"start": v(31.55, 95.22) * mm, "end": v(28.65, 86.28) * mm});
            skLineSegment(sketch, "E6.2.64", {"start": v(22.83, 133.12) * mm, "end": v(45.66, 149.71) * mm});
            skLineSegment(sketch, "E6.2.65", {"start": v(31.55, 106.28) * mm, "end": v(22.83, 133.12) * mm});
            skLineSegment(sketch, "E6.2.66", {"start": v(68.5, 68.38) * mm, "end": v(65.59, 59.43) * mm});
            skLineSegment(sketch, "E6.2.67", {"start": v(36.26, 80.75) * mm, "end": v(43.87, 86.28) * mm});
            skLineSegment(sketch, "E6.2.68", {"start": v(108.35, 86.28) * mm, "end": v(105.44, 95.22) * mm});
            skLineSegment(sketch, "E6.2.69", {"start": v(62.68, 115.23) * mm, "end": v(53.28, 115.23) * mm});
            skPoint(sketch, "E6.2.70", {"position": v(31.55, 62.85) * mm});
            skLineSegment(sketch, "E6.2.71", {"start": v(45.66, 62.85) * mm, "end": v(68.5, 79.44) * mm});
            skLineSegment(sketch, "E6.2.72", {"start": v(31.55, 106.28) * mm, "end": v(54.39, 89.7) * mm});
            skPoint(sketch, "E6.2.73", {"position": v(27.2, 119.7) * mm});
            skPoint(sketch, "E6.2.74", {"position": v(86.97, 76.27) * mm});
            skLineSegment(sketch, "E6.2.75", {"start": v(57.98, 129.7) * mm, "end": v(48.57, 129.7) * mm});
            skLineSegment(sketch, "E6.2.76", {"start": v(54.39, 36.01) * mm, "end": v(45.66, 62.85) * mm});
            skLineSegment(sketch, "E6.2.77", {"start": v(80.81, 59.43) * mm, "end": v(71.4, 59.43) * mm});
            skLineSegment(sketch, "E6.2.78", {"start": v(76.1, 44.96) * mm, "end": v(73.2, 53.9) * mm});
            skLineSegment(sketch, "E6.2.79", {"start": v(110.14, 80.75) * mm, "end": v(117.75, 86.28) * mm});
            skLineSegment(sketch, "E6.2.80", {"start": v(91.33, 120.76) * mm, "end": v(98.94, 115.23) * mm});
            skLineSegment(sketch, "E6.2.81", {"start": v(97.83, 71.8) * mm, "end": v(105.44, 77.33) * mm});
            skLineSegment(sketch, "E6.2.82", {"start": v(105.44, 95.22) * mm, "end": v(113.05, 100.75) * mm});
            skLineSegment(sketch, "E6.2.83", {"start": v(42.76, 129.7) * mm, "end": v(33.35, 129.7) * mm});
            skLineSegment(sketch, "E6.2.84", {"start": v(83.72, 68.38) * mm, "end": v(80.81, 59.43) * mm});
            skPoint(sketch, "E6.2.85", {"position": v(68.5, 36.01) * mm});
            skLineSegment(sketch, "E6.2.86", {"start": v(65.59, 59.43) * mm, "end": v(56.18, 59.43) * mm});
            skLineSegment(sketch, "E6.2.87", {"start": v(26.85, 80.75) * mm, "end": v(23.94, 71.8) * mm});
            skLineSegment(sketch, "E6.2.88", {"start": v(82.6, 89.7) * mm, "end": v(105.44, 106.28) * mm});
            skLineSegment(sketch, "E6.2.89", {"start": v(98.94, 115.23) * mm, "end": v(96.03, 124.18) * mm});
            skLineSegment(sketch, "E6.2.90", {"start": v(113.05, 71.8) * mm, "end": v(110.14, 80.75) * mm});
            skPoint(sketch, "E6.2.91", {"position": v(50.03, 49.43) * mm});
            skLineSegment(sketch, "E6.2.92", {"start": v(60.89, 138.65) * mm, "end": v(57.98, 129.7) * mm});
            skLineSegment(sketch, "E6.2.93", {"start": v(79.01, 129.7) * mm, "end": v(76.1, 138.65) * mm});
            skPoint(sketch, "E6.2.94", {"position": v(34.25, 141.42) * mm});
            skLineSegment(sketch, "E6.2.95", {"start": v(105.44, 106.28) * mm, "end": v(128.27, 89.7) * mm});
            skLineSegment(sketch, "E6.2.96", {"start": v(8.72, 89.7) * mm, "end": v(31.55, 106.28) * mm});
            skLineSegment(sketch, "E6.2.97", {"start": v(93.13, 86.28) * mm, "end": v(100.74, 80.75) * mm});
            skLineSegment(sketch, "E6.2.98", {"start": v(105.44, 95.22) * mm, "end": v(102.53, 86.28) * mm});
            skLineSegment(sketch, "E6.2.99", {"start": v(108.35, 115.23) * mm, "end": v(98.94, 115.23) * mm});
            skLineSegment(sketch, "E6.2.100", {"start": v(48.57, 129.7) * mm, "end": v(45.66, 138.65) * mm});
            skPoint(sketch, "E6.2.101", {"position": v(123.91, 76.27) * mm});
            skPoint(sketch, "E6.2.102", {"position": v(116.86, 97.99) * mm});
            skLineSegment(sketch, "E6.2.103", {"start": v(50.37, 124.18) * mm, "end": v(57.98, 129.7) * mm});
            skLineSegment(sketch, "E6.2.104", {"start": v(79.01, 129.7) * mm, "end": v(86.63, 124.18) * mm});
            skLineSegment(sketch, "E6.2.105", {"start": v(38.05, 115.23) * mm, "end": v(45.66, 120.76) * mm});
            skPoint(sketch, "E6.2.106", {"position": v(57.08, 141.42) * mm});
            skPoint(sketch, "E6.2.107", {"position": v(72.86, 119.7) * mm});
            skLineSegment(sketch, "E6.2.108", {"start": v(68.5, 79.44) * mm, "end": v(91.33, 62.85) * mm});
            skPoint(sketch, "E6.2.109", {"position": v(79.91, 141.42) * mm});
            skPoint(sketch, "E6.2.110", {"position": v(42.97, 97.99) * mm});
            skLineSegment(sketch, "E6.2.111", {"start": v(71.4, 59.43) * mm, "end": v(68.5, 68.38) * mm});
            skLineSegment(sketch, "E6.2.112", {"start": v(91.33, 149.71) * mm, "end": v(114.16, 133.12) * mm});
            skLineSegment(sketch, "E6.2.113", {"start": v(86.63, 124.18) * mm, "end": v(83.72, 115.23) * mm});
            skLineSegment(sketch, "E6.2.114", {"start": v(28.65, 86.28) * mm, "end": v(19.24, 86.28) * mm});
            skLineSegment(sketch, "E6.2.115", {"start": v(39.16, 71.8) * mm, "end": v(36.26, 80.75) * mm});
            skLineSegment(sketch, "E6.2.116", {"start": v(17.44, 62.85) * mm, "end": v(8.72, 89.7) * mm});
            skLineSegment(sketch, "E6.2.117", {"start": v(88.42, 129.7) * mm, "end": v(79.01, 129.7) * mm});
            skLineSegment(sketch, "E6.2.118", {"start": v(40.96, 124.18) * mm, "end": v(38.05, 115.23) * mm});
            skLineSegment(sketch, "E6.2.119", {"start": v(128.27, 89.7) * mm, "end": v(119.55, 62.85) * mm});
            skLineSegment(sketch, "E6.2.120", {"start": v(96.03, 124.18) * mm, "end": v(103.64, 129.7) * mm});
            skLineSegment(sketch, "E6.2.121", {"start": v(19.24, 86.28) * mm, "end": v(26.85, 80.75) * mm});
            skLineSegment(sketch, "E6.2.122", {"start": v(68.5, 50.49) * mm, "end": v(76.1, 44.96) * mm});
            skLineSegment(sketch, "E6.2.123", {"start": v(91.33, 138.65) * mm, "end": v(88.42, 129.7) * mm});
            skLineSegment(sketch, "E6.2.124", {"start": v(60.89, 44.96) * mm, "end": v(68.5, 50.49) * mm});
            skLineSegment(sketch, "E6.2.125", {"start": v(91.33, 62.85) * mm, "end": v(82.6, 36.01) * mm});
            skLineSegment(sketch, "E6.2.126", {"start": v(45.66, 120.76) * mm, "end": v(53.28, 115.23) * mm});
            skPoint(sketch, "E6.2.127", {"position": v(13.08, 76.27) * mm});
            skLineSegment(sketch, "E6.2.128", {"start": v(77.22, 106.28) * mm, "end": v(68.5, 133.12) * mm});
            skLineSegment(sketch, "E6.2.129", {"start": v(68.5, 133.12) * mm, "end": v(91.33, 149.71) * mm});
            skLineSegment(sketch, "E6.2.130", {"start": v(122.46, 71.8) * mm, "end": v(113.05, 71.8) * mm});
            skPoint(sketch, "E6.2.131", {"position": v(86.97, 49.43) * mm});
            skLineSegment(sketch, "E6.2.132", {"start": v(119.55, 62.85) * mm, "end": v(91.33, 62.85) * mm});
            skLineSegment(sketch, "E6.2.133", {"start": v(114.16, 133.12) * mm, "end": v(105.44, 106.28) * mm});
            skLineSegment(sketch, "E6.2.134", {"start": v(105.44, 77.33) * mm, "end": v(113.05, 71.8) * mm});
            skLineSegment(sketch, "E6.2.135", {"start": v(91.33, 138.65) * mm, "end": v(98.94, 144.18) * mm});
            skPoint(sketch, "E6.2.136", {"position": v(105.44, 62.85) * mm});
            skLineSegment(sketch, "E6.2.137", {"start": v(23.94, 71.8) * mm, "end": v(31.55, 77.33) * mm});
            skLineSegment(sketch, "E6.2.138", {"start": v(100.74, 80.75) * mm, "end": v(97.83, 71.8) * mm});
            skLineSegment(sketch, "E6.2.139", {"start": v(59.78, 106.28) * mm, "end": v(31.55, 106.28) * mm});
            skLineSegment(sketch, "E6.2.140", {"start": v(105.44, 106.28) * mm, "end": v(77.22, 106.28) * mm});
            skLineSegment(sketch, "E6.2.141", {"start": v(43.87, 86.28) * mm, "end": v(34.46, 86.28) * mm});
            skPoint(sketch, "E6.2.142", {"position": v(50.03, 76.27) * mm});
            skPoint(sketch, "E6.2.143", {"position": v(79.91, 71.15) * mm});
            skLineSegment(sketch, "E6.2.144", {"start": v(34.46, 86.28) * mm, "end": v(31.55, 95.22) * mm});
            skLineSegment(sketch, "E6.2.145", {"start": v(91.33, 62.85) * mm, "end": v(82.6, 89.7) * mm});
            skLineSegment(sketch, "E6.2.146", {"start": v(73.2, 53.9) * mm, "end": v(80.81, 59.43) * mm});
            skLineSegment(sketch, "E6.2.147", {"start": v(117.75, 86.28) * mm, "end": v(108.35, 86.28) * mm});
            skLineSegment(sketch, "E6.2.148", {"start": v(45.66, 62.85) * mm, "end": v(17.44, 62.85) * mm});
            skLineSegment(sketch, "E6.2.149", {"start": v(53.28, 115.23) * mm, "end": v(50.37, 124.18) * mm});
            skLineSegment(sketch, "E6.2.150", {"start": v(48.57, 71.8) * mm, "end": v(39.16, 71.8) * mm});
            skLineSegment(sketch, "E6.2.151", {"start": v(56.18, 59.43) * mm, "end": v(63.8, 53.9) * mm});
            skLineSegment(sketch, "E6.2.152", {"start": v(82.6, 36.01) * mm, "end": v(54.39, 36.01) * mm});
            skLineSegment(sketch, "E6.2.153", {"start": v(102.53, 86.28) * mm, "end": v(93.13, 86.28) * mm});
            skLineSegment(sketch, "E6.2.154", {"start": v(93.13, 86.28) * mm, "end": v(90.22, 95.22) * mm});
            skLineSegment(sketch, "E6.2.155", {"start": v(83.72, 115.23) * mm, "end": v(91.33, 120.76) * mm});
            skLineSegment(sketch, "E6.2.156", {"start": v(68.5, 133.12) * mm, "end": v(59.78, 106.28) * mm});
            skLineSegment(sketch, "E6.2.157", {"start": v(33.35, 129.7) * mm, "end": v(40.96, 124.18) * mm});
            skLineSegment(sketch, "E6.2.158", {"start": v(54.39, 89.7) * mm, "end": v(45.66, 62.85) * mm});
            skLineSegment(sketch, "E6.2.159", {"start": v(33.35, 129.7) * mm, "end": v(30.44, 138.65) * mm});
            skLineSegment(sketch, "E6.2.160", {"start": v(31.55, 77.33) * mm, "end": v(39.16, 71.8) * mm});
            skLineSegment(sketch, "E6.2.161", {"start": v(94.24, 129.7) * mm, "end": v(91.33, 138.65) * mm});
            skPoint(sketch, "E6.2.162", {"position": v(57.08, 71.15) * mm});
            skPoint(sketch, "E6.2.163", {"position": v(45.66, 106.28) * mm});
            skLineSegment(sketch, "E6.2.164", {"start": v(63.8, 53.9) * mm, "end": v(60.89, 44.96) * mm});
            skLineSegment(sketch, "E6.2.165", {"start": v(45.66, 149.71) * mm, "end": v(68.5, 133.12) * mm});
            skLineSegment(sketch, "E6.2.166", {"start": v(31.55, 95.22) * mm, "end": v(39.16, 100.75) * mm});
            skPoint(sketch, "E6.2.167", {"position": v(94.02, 97.99) * mm});
            skLineSegment(sketch, "E6.2.168", {"start": v(103.64, 129.7) * mm, "end": v(94.24, 129.7) * mm});
            skPoint(sketch, "E6.2.169", {"position": v(109.8, 119.7) * mm});
            skPoint(sketch, "E6.2.170", {"position": v(64.14, 119.7) * mm});
            skPoint(sketch, "E6.2.171", {"position": v(20.14, 97.99) * mm});
            skPoint(sketch, "E6.2.172", {"position": v(102.75, 141.42) * mm});
            skPoint(sketch, "E6.2.173", {"position": v(105.44, 62.85) * mm});
            skPoint(sketch, "E6.2.174", {"position": v(50.03, 76.27) * mm});
            skPoint(sketch, "E6.2.175", {"position": v(102.75, 141.42) * mm});
            skPoint(sketch, "E6.2.176", {"position": v(57.08, 71.15) * mm});
            skPoint(sketch, "E6.2.177", {"position": v(50.03, 49.43) * mm});
            skPoint(sketch, "E6.2.178", {"position": v(109.8, 119.7) * mm});
            skPoint(sketch, "E6.2.179", {"position": v(94.02, 97.99) * mm});
            skPoint(sketch, "E6.2.180", {"position": v(86.97, 49.43) * mm});
            skPoint(sketch, "E6.2.181", {"position": v(64.14, 119.7) * mm});
            skPoint(sketch, "E6.2.182", {"position": v(45.66, 106.28) * mm});
            skPoint(sketch, "E6.2.183", {"position": v(27.2, 119.7) * mm});
            skPoint(sketch, "E6.2.184", {"position": v(116.86, 97.99) * mm});
            skPoint(sketch, "E6.2.185", {"position": v(20.14, 97.99) * mm});
            skPoint(sketch, "E6.2.186", {"position": v(31.55, 62.85) * mm});
            skPoint(sketch, "E6.2.187", {"position": v(72.86, 119.7) * mm});
            skPoint(sketch, "E6.2.188", {"position": v(79.91, 141.42) * mm});
            skPoint(sketch, "E6.2.189", {"position": v(57.08, 141.42) * mm});
            skPoint(sketch, "E6.2.190", {"position": v(68.5, 36.01) * mm});
            skPoint(sketch, "E6.2.191", {"position": v(86.97, 76.27) * mm});
            skPoint(sketch, "E6.2.192", {"position": v(91.33, 106.28) * mm});
            skPoint(sketch, "E6.2.193", {"position": v(34.25, 141.42) * mm});
            skPoint(sketch, "E6.2.194", {"position": v(42.97, 97.99) * mm});
            skPoint(sketch, "E6.2.195", {"position": v(123.91, 76.27) * mm});
            skPoint(sketch, "E6.2.196", {"position": v(13.08, 76.27) * mm});
            skPoint(sketch, "E6.2.197", {"position": v(79.91, 71.15) * mm});
            skLineSegment(sketch, "E6.2.198", {"start": v(39.16, 71.8) * mm, "end": v(36.26, 62.85) * mm});
            skLineSegment(sketch, "E6.2.199", {"start": v(36.26, 62.85) * mm, "end": v(26.85, 62.85) * mm});
            skLineSegment(sketch, "E6.2.200", {"start": v(86.63, 106.28) * mm, "end": v(83.72, 115.23) * mm});
            skLineSegment(sketch, "E6.2.201", {"start": v(40.96, 106.28) * mm, "end": v(38.05, 115.23) * mm});
            skLineSegment(sketch, "E6.2.202", {"start": v(11.63, 80.75) * mm, "end": v(19.24, 86.28) * mm});
            skLineSegment(sketch, "E6.2.203", {"start": v(30.44, 138.65) * mm, "end": v(38.05, 144.18) * mm});
            skLineSegment(sketch, "E6.2.204", {"start": v(60.89, 73.91) * mm, "end": v(68.5, 68.38) * mm});
            skLineSegment(sketch, "E6.2.205", {"start": v(19.24, 86.28) * mm, "end": v(16.33, 95.22) * mm});
            skLineSegment(sketch, "E6.2.206", {"start": v(43.87, 86.28) * mm, "end": v(51.48, 80.75) * mm});
            skLineSegment(sketch, "E6.2.207", {"start": v(74.31, 115.23) * mm, "end": v(71.4, 124.18) * mm});
            skLineSegment(sketch, "E6.2.208", {"start": v(38.05, 115.23) * mm, "end": v(28.65, 115.23) * mm});
            skLineSegment(sketch, "E6.2.209", {"start": v(110.14, 62.85) * mm, "end": v(100.74, 62.85) * mm});
            skLineSegment(sketch, "E6.2.210", {"start": v(106.55, 138.65) * mm, "end": v(103.64, 129.7) * mm});
            skLineSegment(sketch, "E6.2.211", {"start": v(25.74, 124.18) * mm, "end": v(33.35, 129.7) * mm});
            skLineSegment(sketch, "E6.2.212", {"start": v(117.75, 86.28) * mm, "end": v(125.37, 80.75) * mm});
            skLineSegment(sketch, "E6.2.213", {"start": v(90.22, 95.22) * mm, "end": v(97.83, 100.75) * mm});
            skLineSegment(sketch, "E6.2.214", {"start": v(88.42, 71.8) * mm, "end": v(85.51, 80.75) * mm});
            skLineSegment(sketch, "E6.2.215", {"start": v(83.72, 144.18) * mm, "end": v(91.33, 138.65) * mm});
            skLineSegment(sketch, "E6.2.216", {"start": v(63.8, 36.01) * mm, "end": v(60.89, 44.96) * mm});
            skLineSegment(sketch, "E6.2.217", {"start": v(85.51, 44.96) * mm, "end": v(76.1, 44.96) * mm});
            skLineSegment(sketch, "E6.2.218", {"start": v(100.74, 62.85) * mm, "end": v(97.83, 71.8) * mm});
            skLineSegment(sketch, "E6.2.219", {"start": v(23.94, 100.75) * mm, "end": v(31.55, 95.22) * mm});
            skLineSegment(sketch, "E6.2.220", {"start": v(103.64, 129.7) * mm, "end": v(111.25, 124.18) * mm});
            skLineSegment(sketch, "E6.2.221", {"start": v(45.66, 138.65) * mm, "end": v(53.28, 144.18) * mm});
            skLineSegment(sketch, "E6.2.222", {"start": v(60.89, 44.96) * mm, "end": v(51.48, 44.96) * mm});
            skLineSegment(sketch, "E6.2.223", {"start": v(88.42, 53.9) * mm, "end": v(85.51, 44.96) * mm});
            skLineSegment(sketch, "E6.2.224", {"start": v(56.18, 59.43) * mm, "end": v(53.28, 68.38) * mm});
            skLineSegment(sketch, "E6.2.225", {"start": v(65.59, 124.18) * mm, "end": v(62.68, 115.23) * mm});
            skLineSegment(sketch, "E6.2.226", {"start": v(14.54, 71.8) * mm, "end": v(11.63, 80.75) * mm});
            skLineSegment(sketch, "E6.2.227", {"start": v(76.1, 138.65) * mm, "end": v(83.72, 144.18) * mm});
            skLineSegment(sketch, "E6.2.228", {"start": v(51.48, 44.96) * mm, "end": v(48.57, 53.9) * mm});
            skLineSegment(sketch, "E6.2.229", {"start": v(68.5, 68.38) * mm, "end": v(76.1, 73.91) * mm});
            skLineSegment(sketch, "E6.2.230", {"start": v(46.77, 95.22) * mm, "end": v(43.87, 86.28) * mm});
            skLineSegment(sketch, "E6.2.231", {"start": v(76.1, 73.91) * mm, "end": v(83.72, 68.38) * mm});
            skLineSegment(sketch, "E6.2.232", {"start": v(96.03, 106.28) * mm, "end": v(86.63, 106.28) * mm});
            skLineSegment(sketch, "E6.2.233", {"start": v(97.83, 100.75) * mm, "end": v(105.44, 95.22) * mm});
            skLineSegment(sketch, "E6.2.234", {"start": v(26.85, 62.85) * mm, "end": v(23.94, 71.8) * mm});
            skLineSegment(sketch, "E6.2.235", {"start": v(53.28, 144.18) * mm, "end": v(60.89, 138.65) * mm});
            skLineSegment(sketch, "E6.2.236", {"start": v(57.98, 129.7) * mm, "end": v(65.59, 124.18) * mm});
            skLineSegment(sketch, "E6.2.237", {"start": v(113.05, 100.75) * mm, "end": v(120.66, 95.22) * mm});
            skLineSegment(sketch, "E6.2.238", {"start": v(113.05, 71.8) * mm, "end": v(110.14, 62.85) * mm});
            skLineSegment(sketch, "E6.2.239", {"start": v(73.2, 36.01) * mm, "end": v(63.8, 36.01) * mm});
            skLineSegment(sketch, "E6.2.240", {"start": v(39.16, 100.75) * mm, "end": v(46.77, 95.22) * mm});
            skLineSegment(sketch, "E6.2.241", {"start": v(97.83, 71.8) * mm, "end": v(88.42, 71.8) * mm});
            skLineSegment(sketch, "E6.2.242", {"start": v(53.28, 115.23) * mm, "end": v(50.37, 106.28) * mm});
            skLineSegment(sketch, "E6.2.243", {"start": v(98.94, 144.18) * mm, "end": v(106.55, 138.65) * mm});
            skLineSegment(sketch, "E6.2.244", {"start": v(50.37, 106.28) * mm, "end": v(40.96, 106.28) * mm});
            skLineSegment(sketch, "E6.2.245", {"start": v(120.66, 95.22) * mm, "end": v(117.75, 86.28) * mm});
            skLineSegment(sketch, "E6.2.246", {"start": v(111.25, 124.18) * mm, "end": v(108.35, 115.23) * mm});
            skLineSegment(sketch, "E6.2.247", {"start": v(28.65, 115.23) * mm, "end": v(25.74, 124.18) * mm});
            skLineSegment(sketch, "E6.2.248", {"start": v(85.51, 80.75) * mm, "end": v(93.13, 86.28) * mm});
            skLineSegment(sketch, "E6.2.249", {"start": v(23.94, 71.8) * mm, "end": v(14.54, 71.8) * mm});
            skLineSegment(sketch, "E6.2.250", {"start": v(80.81, 59.43) * mm, "end": v(88.42, 53.9) * mm});
            skLineSegment(sketch, "E6.2.251", {"start": v(71.4, 124.18) * mm, "end": v(79.01, 129.7) * mm});
            skLineSegment(sketch, "E6.2.252", {"start": v(48.57, 53.9) * mm, "end": v(56.18, 59.43) * mm});
            skLineSegment(sketch, "E6.2.253", {"start": v(76.1, 44.96) * mm, "end": v(73.2, 36.01) * mm});
            skLineSegment(sketch, "E6.2.254", {"start": v(83.72, 115.23) * mm, "end": v(74.31, 115.23) * mm});
            skLineSegment(sketch, "E6.2.255", {"start": v(51.48, 80.75) * mm, "end": v(48.57, 71.8) * mm});
            skLineSegment(sketch, "E6.2.256", {"start": v(16.33, 95.22) * mm, "end": v(23.94, 100.75) * mm});
            skLineSegment(sketch, "E6.2.257", {"start": v(53.28, 68.38) * mm, "end": v(60.89, 73.91) * mm});
            skLineSegment(sketch, "E6.2.258", {"start": v(125.37, 80.75) * mm, "end": v(122.46, 71.8) * mm});
            skLineSegment(sketch, "E6.2.259", {"start": v(98.94, 115.23) * mm, "end": v(96.03, 106.28) * mm});
            skLineSegment(sketch, "E6.2.260", {"start": v(38.05, 144.18) * mm, "end": v(45.66, 138.65) * mm});
            skPoint(sketch, "E6.3.0", {"position": v(-123.91, 76.27) * mm});
            skPoint(sketch, "E6.3.1", {"position": v(-13.08, 76.27) * mm});
            skPoint(sketch, "E6.3.2", {"position": v(-109.8, 119.7) * mm});
            skPoint(sketch, "E6.3.3", {"position": v(-31.55, 62.85) * mm});
            skPoint(sketch, "E6.3.4", {"position": v(-45.66, 106.28) * mm});
            skPoint(sketch, "E6.3.5", {"position": v(-45.66, 125.7) * mm});
            skPoint(sketch, "E6.3.6", {"position": v(-86.97, 49.43) * mm});
            skPoint(sketch, "E6.3.7", {"position": v(-20.14, 97.99) * mm});
            skPoint(sketch, "E6.3.8", {"position": v(-27.2, 119.7) * mm});
            skPoint(sketch, "E6.3.9", {"position": v(-50.03, 76.27) * mm});
            skPoint(sketch, "E6.3.10", {"position": v(-57.08, 141.42) * mm});
            skPoint(sketch, "E6.3.11", {"position": v(-102.75, 141.42) * mm});
            skPoint(sketch, "E6.3.12", {"position": v(-86.97, 76.27) * mm});
            skPoint(sketch, "E6.3.13", {"position": v(-79.91, 141.42) * mm});
            skPoint(sketch, "E6.3.14", {"position": v(-64.14, 119.7) * mm});
            skPoint(sketch, "E6.3.15", {"position": v(-91.33, 106.28) * mm});
            skLineSegment(sketch, "E6.3.16", {"start": v(-110.83, 36.01) * mm, "end": v(-137, 116.53) * mm});
            skPoint(sketch, "E6.3.17", {"position": v(-105.44, 62.85) * mm});
            skLineSegment(sketch, "E6.3.18", {"start": v(0, 116.53) * mm, "end": v(-26.16, 36.01) * mm});
            skPoint(sketch, "E6.3.19", {"position": v(-50.03, 49.43) * mm});
            skPoint(sketch, "E6.3.20", {"position": v(-68.5, 94.28) * mm});
            skLineSegment(sketch, "E6.3.21", {"start": v(-137, 116.53) * mm, "end": v(-68.5, 166.3) * mm});
            skPoint(sketch, "E6.3.22", {"position": v(-105.44, 82.27) * mm});
            skPoint(sketch, "E6.3.23", {"position": v(-57.08, 71.15) * mm});
            skPoint(sketch, "E6.3.24", {"position": v(-94.02, 97.99) * mm});
            skPoint(sketch, "E6.3.25", {"position": v(-34.25, 141.42) * mm});
            skPoint(sketch, "E6.3.26", {"position": v(-42.97, 97.99) * mm});
            skLineSegment(sketch, "E6.3.27", {"start": v(-68.5, 166.3) * mm, "end": v(0, 116.53) * mm});
            skPoint(sketch, "E6.3.28", {"position": v(-79.91, 71.15) * mm});
            skPoint(sketch, "E6.3.29", {"position": v(-72.86, 119.7) * mm});
            skPoint(sketch, "E6.3.30", {"position": v(-116.86, 97.99) * mm});
            skPoint(sketch, "E6.3.31", {"position": v(-68.5, 36.01) * mm});
            skLineSegment(sketch, "E6.3.32", {"start": v(-26.16, 36.01) * mm, "end": v(-110.83, 36.01) * mm});
            skPoint(sketch, "E6.3.33", {"position": v(-91.33, 125.7) * mm});
            skPoint(sketch, "E6.3.34", {"position": v(-68.5, 55.43) * mm});
            skPoint(sketch, "E6.3.35", {"position": v(-31.55, 82.27) * mm});
            skPoint(sketch, "E6.3.36", {"position": v(-57.08, 71.15) * mm});
            skPoint(sketch, "E6.3.37", {"position": v(-31.55, 62.85) * mm});
            skPoint(sketch, "E6.3.38", {"position": v(-79.91, 71.15) * mm});
            skPoint(sketch, "E6.3.39", {"position": v(-72.86, 119.7) * mm});
            skPoint(sketch, "E6.3.40", {"position": v(-34.25, 141.42) * mm});
            skPoint(sketch, "E6.3.41", {"position": v(-123.91, 76.27) * mm});
            skPoint(sketch, "E6.3.42", {"position": v(-64.14, 119.7) * mm});
            skPoint(sketch, "E6.3.43", {"position": v(-86.97, 76.27) * mm});
            skPoint(sketch, "E6.3.44", {"position": v(-109.8, 119.7) * mm});
            skPoint(sketch, "E6.3.45", {"position": v(-94.02, 97.99) * mm});
            skPoint(sketch, "E6.3.46", {"position": v(-68.5, 36.01) * mm});
            skPoint(sketch, "E6.3.47", {"position": v(-50.03, 49.43) * mm});
            skPoint(sketch, "E6.3.48", {"position": v(-20.14, 97.99) * mm});
            skPoint(sketch, "E6.3.49", {"position": v(-91.33, 106.28) * mm});
            skPoint(sketch, "E6.3.50", {"position": v(-42.97, 97.99) * mm});
            skPoint(sketch, "E6.3.51", {"position": v(-86.97, 49.43) * mm});
            skPoint(sketch, "E6.3.52", {"position": v(-57.08, 141.42) * mm});
            skPoint(sketch, "E6.3.53", {"position": v(-116.86, 97.99) * mm});
            skPoint(sketch, "E6.3.54", {"position": v(-50.03, 76.27) * mm});
            skPoint(sketch, "E6.3.55", {"position": v(-27.2, 119.7) * mm});
            skPoint(sketch, "E6.3.56", {"position": v(-105.44, 62.85) * mm});
            skPoint(sketch, "E6.3.57", {"position": v(-45.66, 106.28) * mm});
            skPoint(sketch, "E6.3.58", {"position": v(-79.91, 141.42) * mm});
            skPoint(sketch, "E6.3.59", {"position": v(-102.75, 141.42) * mm});
            skPoint(sketch, "E6.3.60", {"position": v(-13.08, 76.27) * mm});
            skLineSegment(sketch, "E6.3.61", {"start": v(-117.75, 86.28) * mm, "end": v(-110.14, 80.75) * mm});
            skPoint(sketch, "E6.3.62", {"position": v(-72.86, 119.7) * mm});
            skLineSegment(sketch, "E6.3.63", {"start": v(-80.81, 59.43) * mm, "end": v(-73.2, 53.9) * mm});
            skLineSegment(sketch, "E6.3.64", {"start": v(-119.55, 62.85) * mm, "end": v(-128.27, 89.7) * mm});
            skLineSegment(sketch, "E6.3.65", {"start": v(-91.33, 62.85) * mm, "end": v(-119.55, 62.85) * mm});
            skLineSegment(sketch, "E6.3.66", {"start": v(-43.87, 86.28) * mm, "end": v(-36.26, 80.75) * mm});
            skLineSegment(sketch, "E6.3.67", {"start": v(-65.59, 59.43) * mm, "end": v(-68.5, 68.38) * mm});
            skLineSegment(sketch, "E6.3.68", {"start": v(-48.57, 129.7) * mm, "end": v(-57.98, 129.7) * mm});
            skLineSegment(sketch, "E6.3.69", {"start": v(-90.22, 95.22) * mm, "end": v(-93.13, 86.28) * mm});
            skPoint(sketch, "E6.3.70", {"position": v(-50.03, 49.43) * mm});
            skLineSegment(sketch, "E6.3.71", {"start": v(-45.66, 62.85) * mm, "end": v(-54.39, 89.7) * mm});
            skLineSegment(sketch, "E6.3.72", {"start": v(-91.33, 62.85) * mm, "end": v(-68.5, 79.44) * mm});
            skPoint(sketch, "E6.3.73", {"position": v(-105.44, 62.85) * mm});
            skPoint(sketch, "E6.3.74", {"position": v(-45.66, 106.28) * mm});
            skLineSegment(sketch, "E6.3.75", {"start": v(-105.44, 95.22) * mm, "end": v(-108.35, 86.28) * mm});
            skLineSegment(sketch, "E6.3.76", {"start": v(-17.44, 62.85) * mm, "end": v(-45.66, 62.85) * mm});
            skLineSegment(sketch, "E6.3.77", {"start": v(-31.55, 95.22) * mm, "end": v(-34.46, 86.28) * mm});
            skLineSegment(sketch, "E6.3.78", {"start": v(-19.24, 86.28) * mm, "end": v(-28.65, 86.28) * mm});
            skLineSegment(sketch, "E6.3.79", {"start": v(-42.76, 129.7) * mm, "end": v(-45.66, 138.65) * mm});
            skLineSegment(sketch, "E6.3.80", {"start": v(-86.63, 124.18) * mm, "end": v(-79.01, 129.7) * mm});
            skLineSegment(sketch, "E6.3.81", {"start": v(-38.05, 115.23) * mm, "end": v(-40.96, 124.18) * mm});
            skLineSegment(sketch, "E6.3.82", {"start": v(-57.98, 129.7) * mm, "end": v(-60.89, 138.65) * mm});
            skLineSegment(sketch, "E6.3.83", {"start": v(-110.14, 80.75) * mm, "end": v(-113.05, 71.8) * mm});
            skLineSegment(sketch, "E6.3.84", {"start": v(-39.16, 100.75) * mm, "end": v(-31.55, 95.22) * mm});
            skPoint(sketch, "E6.3.85", {"position": v(-13.08, 76.27) * mm});
            skLineSegment(sketch, "E6.3.86", {"start": v(-36.26, 80.75) * mm, "end": v(-39.16, 71.8) * mm});
            skLineSegment(sketch, "E6.3.87", {"start": v(-68.5, 50.49) * mm, "end": v(-60.89, 44.96) * mm});
            skLineSegment(sketch, "E6.3.88", {"start": v(-59.78, 106.28) * mm, "end": v(-68.5, 133.12) * mm});
            skLineSegment(sketch, "E6.3.89", {"start": v(-79.01, 129.7) * mm, "end": v(-88.42, 129.7) * mm});
            skLineSegment(sketch, "E6.3.90", {"start": v(-33.35, 129.7) * mm, "end": v(-42.76, 129.7) * mm});
            skPoint(sketch, "E6.3.91", {"position": v(-31.55, 62.85) * mm});
            skLineSegment(sketch, "E6.3.92", {"start": v(-113.05, 100.75) * mm, "end": v(-105.44, 95.22) * mm});
            skLineSegment(sketch, "E6.3.93", {"start": v(-98.94, 115.23) * mm, "end": v(-108.35, 115.23) * mm});
            skPoint(sketch, "E6.3.94", {"position": v(-123.91, 76.27) * mm});
            skLineSegment(sketch, "E6.3.95", {"start": v(-68.5, 133.12) * mm, "end": v(-45.66, 149.71) * mm});
            skLineSegment(sketch, "E6.3.96", {"start": v(-82.6, 36.01) * mm, "end": v(-91.33, 62.85) * mm});
            skLineSegment(sketch, "E6.3.97", {"start": v(-53.28, 115.23) * mm, "end": v(-45.66, 120.76) * mm});
            skLineSegment(sketch, "E6.3.98", {"start": v(-57.98, 129.7) * mm, "end": v(-50.37, 124.18) * mm});
            skLineSegment(sketch, "E6.3.99", {"start": v(-76.1, 138.65) * mm, "end": v(-79.01, 129.7) * mm});
            skLineSegment(sketch, "E6.3.100", {"start": v(-108.35, 86.28) * mm, "end": v(-117.75, 86.28) * mm});
            skPoint(sketch, "E6.3.101", {"position": v(-34.25, 141.42) * mm});
            skPoint(sketch, "E6.3.102", {"position": v(-57.08, 141.42) * mm});
            skLineSegment(sketch, "E6.3.103", {"start": v(-102.53, 86.28) * mm, "end": v(-105.44, 95.22) * mm});
            skLineSegment(sketch, "E6.3.104", {"start": v(-98.94, 115.23) * mm, "end": v(-91.33, 120.76) * mm});
            skLineSegment(sketch, "E6.3.105", {"start": v(-97.83, 71.8) * mm, "end": v(-100.74, 80.75) * mm});
            skPoint(sketch, "E6.3.106", {"position": v(-116.86, 97.99) * mm});
            skPoint(sketch, "E6.3.107", {"position": v(-91.33, 106.28) * mm});
            skLineSegment(sketch, "E6.3.108", {"start": v(-54.39, 89.7) * mm, "end": v(-31.55, 106.28) * mm});
            skPoint(sketch, "E6.3.109", {"position": v(-109.8, 119.7) * mm});
            skPoint(sketch, "E6.3.110", {"position": v(-79.91, 71.15) * mm});
            skLineSegment(sketch, "E6.3.111", {"start": v(-34.46, 86.28) * mm, "end": v(-43.87, 86.28) * mm});
            skLineSegment(sketch, "E6.3.112", {"start": v(-114.16, 133.12) * mm, "end": v(-91.33, 149.71) * mm});
            skLineSegment(sketch, "E6.3.113", {"start": v(-91.33, 120.76) * mm, "end": v(-83.72, 115.23) * mm});
            skLineSegment(sketch, "E6.3.114", {"start": v(-73.2, 53.9) * mm, "end": v(-76.1, 44.96) * mm});
            skLineSegment(sketch, "E6.3.115", {"start": v(-56.18, 59.43) * mm, "end": v(-65.59, 59.43) * mm});
            skLineSegment(sketch, "E6.3.116", {"start": v(-54.39, 36.01) * mm, "end": v(-82.6, 36.01) * mm});
            skLineSegment(sketch, "E6.3.117", {"start": v(-96.03, 124.18) * mm, "end": v(-98.94, 115.23) * mm});
            skLineSegment(sketch, "E6.3.118", {"start": v(-105.44, 77.33) * mm, "end": v(-97.83, 71.8) * mm});
            skLineSegment(sketch, "E6.3.119", {"start": v(-45.66, 149.71) * mm, "end": v(-22.83, 133.12) * mm});
            skLineSegment(sketch, "E6.3.120", {"start": v(-88.42, 129.7) * mm, "end": v(-91.33, 138.65) * mm});
            skLineSegment(sketch, "E6.3.121", {"start": v(-76.1, 44.96) * mm, "end": v(-68.5, 50.49) * mm});
            skLineSegment(sketch, "E6.3.122", {"start": v(-26.85, 80.75) * mm, "end": v(-19.24, 86.28) * mm});
            skLineSegment(sketch, "E6.3.123", {"start": v(-103.64, 129.7) * mm, "end": v(-96.03, 124.18) * mm});
            skLineSegment(sketch, "E6.3.124", {"start": v(-23.94, 71.8) * mm, "end": v(-26.85, 80.75) * mm});
            skLineSegment(sketch, "E6.3.125", {"start": v(-31.55, 106.28) * mm, "end": v(-8.72, 89.7) * mm});
            skLineSegment(sketch, "E6.3.126", {"start": v(-100.74, 80.75) * mm, "end": v(-93.13, 86.28) * mm});
            skPoint(sketch, "E6.3.127", {"position": v(-68.5, 36.01) * mm});
            skLineSegment(sketch, "E6.3.128", {"start": v(-77.22, 106.28) * mm, "end": v(-105.44, 106.28) * mm});
            skLineSegment(sketch, "E6.3.129", {"start": v(-105.44, 106.28) * mm, "end": v(-114.16, 133.12) * mm});
            skLineSegment(sketch, "E6.3.130", {"start": v(-30.44, 138.65) * mm, "end": v(-33.35, 129.7) * mm});
            skPoint(sketch, "E6.3.131", {"position": v(-20.14, 97.99) * mm});
            skLineSegment(sketch, "E6.3.132", {"start": v(-22.83, 133.12) * mm, "end": v(-31.55, 106.28) * mm});
            skLineSegment(sketch, "E6.3.133", {"start": v(-91.33, 149.71) * mm, "end": v(-68.5, 133.12) * mm});
            skLineSegment(sketch, "E6.3.134", {"start": v(-40.96, 124.18) * mm, "end": v(-33.35, 129.7) * mm});
            skLineSegment(sketch, "E6.3.135", {"start": v(-103.64, 129.7) * mm, "end": v(-106.55, 138.65) * mm});
            skPoint(sketch, "E6.3.136", {"position": v(-27.2, 119.7) * mm});
            skLineSegment(sketch, "E6.3.137", {"start": v(-60.89, 44.96) * mm, "end": v(-63.8, 53.9) * mm});
            skLineSegment(sketch, "E6.3.138", {"start": v(-45.66, 120.76) * mm, "end": v(-38.05, 115.23) * mm});
            skLineSegment(sketch, "E6.3.139", {"start": v(-82.6, 89.7) * mm, "end": v(-91.33, 62.85) * mm});
            skLineSegment(sketch, "E6.3.140", {"start": v(-68.5, 133.12) * mm, "end": v(-77.22, 106.28) * mm});
            skLineSegment(sketch, "E6.3.141", {"start": v(-68.5, 68.38) * mm, "end": v(-71.4, 59.43) * mm});
            skPoint(sketch, "E6.3.142", {"position": v(-57.08, 71.15) * mm});
            skPoint(sketch, "E6.3.143", {"position": v(-42.97, 97.99) * mm});
            skLineSegment(sketch, "E6.3.144", {"start": v(-71.4, 59.43) * mm, "end": v(-80.81, 59.43) * mm});
            skLineSegment(sketch, "E6.3.145", {"start": v(-31.55, 106.28) * mm, "end": v(-59.78, 106.28) * mm});
            skLineSegment(sketch, "E6.3.146", {"start": v(-28.65, 86.28) * mm, "end": v(-31.55, 95.22) * mm});
            skLineSegment(sketch, "E6.3.147", {"start": v(-45.66, 138.65) * mm, "end": v(-48.57, 129.7) * mm});
            skLineSegment(sketch, "E6.3.148", {"start": v(-45.66, 62.85) * mm, "end": v(-54.39, 36.01) * mm});
            skLineSegment(sketch, "E6.3.149", {"start": v(-93.13, 86.28) * mm, "end": v(-102.53, 86.28) * mm});
            skLineSegment(sketch, "E6.3.150", {"start": v(-53.28, 68.38) * mm, "end": v(-56.18, 59.43) * mm});
            skLineSegment(sketch, "E6.3.151", {"start": v(-39.16, 71.8) * mm, "end": v(-31.55, 77.33) * mm});
            skLineSegment(sketch, "E6.3.152", {"start": v(-8.72, 89.7) * mm, "end": v(-17.44, 62.85) * mm});
            skLineSegment(sketch, "E6.3.153", {"start": v(-50.37, 124.18) * mm, "end": v(-53.28, 115.23) * mm});
            skLineSegment(sketch, "E6.3.154", {"start": v(-53.28, 115.23) * mm, "end": v(-62.68, 115.23) * mm});
            skLineSegment(sketch, "E6.3.155", {"start": v(-83.72, 115.23) * mm, "end": v(-86.63, 124.18) * mm});
            skLineSegment(sketch, "E6.3.156", {"start": v(-105.44, 106.28) * mm, "end": v(-82.6, 89.7) * mm});
            skLineSegment(sketch, "E6.3.157", {"start": v(-113.05, 71.8) * mm, "end": v(-105.44, 77.33) * mm});
            skLineSegment(sketch, "E6.3.158", {"start": v(-68.5, 79.44) * mm, "end": v(-45.66, 62.85) * mm});
            skLineSegment(sketch, "E6.3.159", {"start": v(-113.05, 71.8) * mm, "end": v(-122.46, 71.8) * mm});
            skLineSegment(sketch, "E6.3.160", {"start": v(-63.8, 53.9) * mm, "end": v(-56.18, 59.43) * mm});
            skLineSegment(sketch, "E6.3.161", {"start": v(-94.24, 129.7) * mm, "end": v(-103.64, 129.7) * mm});
            skPoint(sketch, "E6.3.162", {"position": v(-50.03, 76.27) * mm});
            skPoint(sketch, "E6.3.163", {"position": v(-86.97, 76.27) * mm});
            skLineSegment(sketch, "E6.3.164", {"start": v(-31.55, 77.33) * mm, "end": v(-23.94, 71.8) * mm});
            skLineSegment(sketch, "E6.3.165", {"start": v(-128.27, 89.7) * mm, "end": v(-105.44, 106.28) * mm});
            skLineSegment(sketch, "E6.3.166", {"start": v(-80.81, 59.43) * mm, "end": v(-83.72, 68.38) * mm});
            skPoint(sketch, "E6.3.167", {"position": v(-64.14, 119.7) * mm});
            skLineSegment(sketch, "E6.3.168", {"start": v(-91.33, 138.65) * mm, "end": v(-94.24, 129.7) * mm});
            skPoint(sketch, "E6.3.169", {"position": v(-79.91, 141.42) * mm});
            skPoint(sketch, "E6.3.170", {"position": v(-94.02, 97.99) * mm});
            skPoint(sketch, "E6.3.171", {"position": v(-86.97, 49.43) * mm});
            skPoint(sketch, "E6.3.172", {"position": v(-102.75, 141.42) * mm});
            skPoint(sketch, "E6.3.173", {"position": v(-27.2, 119.7) * mm});
            skPoint(sketch, "E6.3.174", {"position": v(-57.08, 71.15) * mm});
            skPoint(sketch, "E6.3.175", {"position": v(-102.75, 141.42) * mm});
            skPoint(sketch, "E6.3.176", {"position": v(-50.03, 76.27) * mm});
            skPoint(sketch, "E6.3.177", {"position": v(-31.55, 62.85) * mm});
            skPoint(sketch, "E6.3.178", {"position": v(-79.91, 141.42) * mm});
            skPoint(sketch, "E6.3.179", {"position": v(-64.14, 119.7) * mm});
            skPoint(sketch, "E6.3.180", {"position": v(-20.14, 97.99) * mm});
            skPoint(sketch, "E6.3.181", {"position": v(-94.02, 97.99) * mm});
            skPoint(sketch, "E6.3.182", {"position": v(-86.97, 76.27) * mm});
            skPoint(sketch, "E6.3.183", {"position": v(-105.44, 62.85) * mm});
            skPoint(sketch, "E6.3.184", {"position": v(-57.08, 141.42) * mm});
            skPoint(sketch, "E6.3.185", {"position": v(-86.97, 49.43) * mm});
            skPoint(sketch, "E6.3.186", {"position": v(-50.03, 49.43) * mm});
            skPoint(sketch, "E6.3.187", {"position": v(-91.33, 106.28) * mm});
            skPoint(sketch, "E6.3.188", {"position": v(-109.8, 119.7) * mm});
            skPoint(sketch, "E6.3.189", {"position": v(-116.86, 97.99) * mm});
            skPoint(sketch, "E6.3.190", {"position": v(-13.08, 76.27) * mm});
            skPoint(sketch, "E6.3.191", {"position": v(-45.66, 106.28) * mm});
            skPoint(sketch, "E6.3.192", {"position": v(-72.86, 119.7) * mm});
            skPoint(sketch, "E6.3.193", {"position": v(-123.91, 76.27) * mm});
            skPoint(sketch, "E6.3.194", {"position": v(-79.91, 71.15) * mm});
            skPoint(sketch, "E6.3.195", {"position": v(-34.25, 141.42) * mm});
            skPoint(sketch, "E6.3.196", {"position": v(-68.5, 36.01) * mm});
            skPoint(sketch, "E6.3.197", {"position": v(-42.97, 97.99) * mm});
            skLineSegment(sketch, "E6.3.198", {"start": v(-56.18, 59.43) * mm, "end": v(-48.57, 53.9) * mm});
            skLineSegment(sketch, "E6.3.199", {"start": v(-48.57, 53.9) * mm, "end": v(-51.48, 44.96) * mm});
            skLineSegment(sketch, "E6.3.200", {"start": v(-74.31, 115.23) * mm, "end": v(-83.72, 115.23) * mm});
            skLineSegment(sketch, "E6.3.201", {"start": v(-88.42, 71.8) * mm, "end": v(-97.83, 71.8) * mm});
            skLineSegment(sketch, "E6.3.202", {"start": v(-73.2, 36.01) * mm, "end": v(-76.1, 44.96) * mm});
            skLineSegment(sketch, "E6.3.203", {"start": v(-122.46, 71.8) * mm, "end": v(-125.37, 80.75) * mm});
            skLineSegment(sketch, "E6.3.204", {"start": v(-51.48, 80.75) * mm, "end": v(-43.87, 86.28) * mm});
            skLineSegment(sketch, "E6.3.205", {"start": v(-76.1, 44.96) * mm, "end": v(-85.51, 44.96) * mm});
            skLineSegment(sketch, "E6.3.206", {"start": v(-68.5, 68.38) * mm, "end": v(-60.89, 73.91) * mm});
            skLineSegment(sketch, "E6.3.207", {"start": v(-86.63, 106.28) * mm, "end": v(-96.03, 106.28) * mm});
            skLineSegment(sketch, "E6.3.208", {"start": v(-97.83, 71.8) * mm, "end": v(-100.74, 62.85) * mm});
            skLineSegment(sketch, "E6.3.209", {"start": v(-25.74, 124.18) * mm, "end": v(-28.65, 115.23) * mm});
            skLineSegment(sketch, "E6.3.210", {"start": v(-98.94, 144.18) * mm, "end": v(-91.33, 138.65) * mm});
            skLineSegment(sketch, "E6.3.211", {"start": v(-110.14, 62.85) * mm, "end": v(-113.05, 71.8) * mm});
            skLineSegment(sketch, "E6.3.212", {"start": v(-45.66, 138.65) * mm, "end": v(-38.05, 144.18) * mm});
            skLineSegment(sketch, "E6.3.213", {"start": v(-62.68, 115.23) * mm, "end": v(-65.59, 124.18) * mm});
            skLineSegment(sketch, "E6.3.214", {"start": v(-40.96, 106.28) * mm, "end": v(-50.37, 106.28) * mm});
            skLineSegment(sketch, "E6.3.215", {"start": v(-111.25, 124.18) * mm, "end": v(-103.64, 129.7) * mm});
            skLineSegment(sketch, "E6.3.216", {"start": v(-14.54, 71.8) * mm, "end": v(-23.94, 71.8) * mm});
            skLineSegment(sketch, "E6.3.217", {"start": v(-16.33, 95.22) * mm, "end": v(-19.24, 86.28) * mm});
            skLineSegment(sketch, "E6.3.218", {"start": v(-28.65, 115.23) * mm, "end": v(-38.05, 115.23) * mm});
            skLineSegment(sketch, "E6.3.219", {"start": v(-88.42, 53.9) * mm, "end": v(-80.81, 59.43) * mm});
            skLineSegment(sketch, "E6.3.220", {"start": v(-91.33, 138.65) * mm, "end": v(-83.72, 144.18) * mm});
            skLineSegment(sketch, "E6.3.221", {"start": v(-117.75, 86.28) * mm, "end": v(-120.66, 95.22) * mm});
            skLineSegment(sketch, "E6.3.222", {"start": v(-23.94, 71.8) * mm, "end": v(-26.85, 62.85) * mm});
            skLineSegment(sketch, "E6.3.223", {"start": v(-23.94, 100.75) * mm, "end": v(-16.33, 95.22) * mm});
            skLineSegment(sketch, "E6.3.224", {"start": v(-39.16, 71.8) * mm, "end": v(-48.57, 71.8) * mm});
            skLineSegment(sketch, "E6.3.225", {"start": v(-97.83, 100.75) * mm, "end": v(-90.22, 95.22) * mm});
            skLineSegment(sketch, "E6.3.226", {"start": v(-63.8, 36.01) * mm, "end": v(-73.2, 36.01) * mm});
            skLineSegment(sketch, "E6.3.227", {"start": v(-108.35, 115.23) * mm, "end": v(-111.25, 124.18) * mm});
            skLineSegment(sketch, "E6.3.228", {"start": v(-26.85, 62.85) * mm, "end": v(-36.26, 62.85) * mm});
            skLineSegment(sketch, "E6.3.229", {"start": v(-43.87, 86.28) * mm, "end": v(-46.77, 95.22) * mm});
            skLineSegment(sketch, "E6.3.230", {"start": v(-76.1, 73.91) * mm, "end": v(-68.5, 68.38) * mm});
            skLineSegment(sketch, "E6.3.231", {"start": v(-46.77, 95.22) * mm, "end": v(-39.16, 100.75) * mm});
            skLineSegment(sketch, "E6.3.232", {"start": v(-71.4, 124.18) * mm, "end": v(-74.31, 115.23) * mm});
            skLineSegment(sketch, "E6.3.233", {"start": v(-65.59, 124.18) * mm, "end": v(-57.98, 129.7) * mm});
            skLineSegment(sketch, "E6.3.234", {"start": v(-51.48, 44.96) * mm, "end": v(-60.89, 44.96) * mm});
            skLineSegment(sketch, "E6.3.235", {"start": v(-120.66, 95.22) * mm, "end": v(-113.05, 100.75) * mm});
            skLineSegment(sketch, "E6.3.236", {"start": v(-105.44, 95.22) * mm, "end": v(-97.83, 100.75) * mm});
            skLineSegment(sketch, "E6.3.237", {"start": v(-60.89, 138.65) * mm, "end": v(-53.28, 144.18) * mm});
            skLineSegment(sketch, "E6.3.238", {"start": v(-33.35, 129.7) * mm, "end": v(-25.74, 124.18) * mm});
            skLineSegment(sketch, "E6.3.239", {"start": v(-11.63, 80.75) * mm, "end": v(-14.54, 71.8) * mm});
            skLineSegment(sketch, "E6.3.240", {"start": v(-83.72, 68.38) * mm, "end": v(-76.1, 73.91) * mm});
            skLineSegment(sketch, "E6.3.241", {"start": v(-38.05, 115.23) * mm, "end": v(-40.96, 106.28) * mm});
            skLineSegment(sketch, "E6.3.242", {"start": v(-93.13, 86.28) * mm, "end": v(-85.51, 80.75) * mm});
            skLineSegment(sketch, "E6.3.243", {"start": v(-106.55, 138.65) * mm, "end": v(-98.94, 144.18) * mm});
            skLineSegment(sketch, "E6.3.244", {"start": v(-85.51, 80.75) * mm, "end": v(-88.42, 71.8) * mm});
            skLineSegment(sketch, "E6.3.245", {"start": v(-53.28, 144.18) * mm, "end": v(-45.66, 138.65) * mm});
            skLineSegment(sketch, "E6.3.246", {"start": v(-83.72, 144.18) * mm, "end": v(-76.1, 138.65) * mm});
            skLineSegment(sketch, "E6.3.247", {"start": v(-100.74, 62.85) * mm, "end": v(-110.14, 62.85) * mm});
            skLineSegment(sketch, "E6.3.248", {"start": v(-50.37, 106.28) * mm, "end": v(-53.28, 115.23) * mm});
            skLineSegment(sketch, "E6.3.249", {"start": v(-60.89, 44.96) * mm, "end": v(-63.8, 36.01) * mm});
            skLineSegment(sketch, "E6.3.250", {"start": v(-31.55, 95.22) * mm, "end": v(-23.94, 100.75) * mm});
            skLineSegment(sketch, "E6.3.251", {"start": v(-96.03, 106.28) * mm, "end": v(-98.94, 115.23) * mm});
            skLineSegment(sketch, "E6.3.252", {"start": v(-36.26, 62.85) * mm, "end": v(-39.16, 71.8) * mm});
            skLineSegment(sketch, "E6.3.253", {"start": v(-19.24, 86.28) * mm, "end": v(-11.63, 80.75) * mm});
            skLineSegment(sketch, "E6.3.254", {"start": v(-83.72, 115.23) * mm, "end": v(-86.63, 106.28) * mm});
            skLineSegment(sketch, "E6.3.255", {"start": v(-60.89, 73.91) * mm, "end": v(-53.28, 68.38) * mm});
            skLineSegment(sketch, "E6.3.256", {"start": v(-85.51, 44.96) * mm, "end": v(-88.42, 53.9) * mm});
            skLineSegment(sketch, "E6.3.257", {"start": v(-48.57, 71.8) * mm, "end": v(-51.48, 80.75) * mm});
            skLineSegment(sketch, "E6.3.258", {"start": v(-38.05, 144.18) * mm, "end": v(-30.44, 138.65) * mm});
            skLineSegment(sketch, "E6.3.259", {"start": v(-79.01, 129.7) * mm, "end": v(-71.4, 124.18) * mm});
            skLineSegment(sketch, "E6.3.260", {"start": v(-125.37, 80.75) * mm, "end": v(-117.75, 86.28) * mm});
            skPoint(sketch, "E6.4.0", {"position": v(-110.83, -94.28) * mm});
            skPoint(sketch, "E6.4.1", {"position": v(-76.58, 11.13) * mm});
            skPoint(sketch, "E6.4.2", {"position": v(-147.77, -67.44) * mm});
            skPoint(sketch, "E6.4.3", {"position": v(-69.53, -10.59) * mm});
            skPoint(sketch, "E6.4.4", {"position": v(-115.2, -10.59) * mm});
            skPoint(sketch, "E6.4.5", {"position": v(-133.66, -4.58) * mm});
            skPoint(sketch, "E6.4.6", {"position": v(-73.89, -67.44) * mm});
            skPoint(sketch, "E6.4.7", {"position": v(-99.41, 11.13) * mm});
            skPoint(sketch, "E6.4.8", {"position": v(-122.25, 11.13) * mm});
            skPoint(sketch, "E6.4.9", {"position": v(-88, -24) * mm});
            skPoint(sketch, "E6.4.10", {"position": v(-152.13, -10.59) * mm});
            skPoint(sketch, "E6.4.11", {"position": v(-166.25, -54.02) * mm});
            skPoint(sketch, "E6.4.12", {"position": v(-99.41, -59.14) * mm});
            skPoint(sketch, "E6.4.13", {"position": v(-159.19, -32.3) * mm});
            skPoint(sketch, "E6.4.14", {"position": v(-133.66, -24) * mm});
            skPoint(sketch, "E6.4.15", {"position": v(-129.3, -54.02) * mm});
            skLineSegment(sketch, "E6.4.16", {"start": v(-68.5, -94.28) * mm, "end": v(-153.16, -94.28) * mm});
            skPoint(sketch, "E6.4.17", {"position": v(-92.36, -80.86) * mm});
            skLineSegment(sketch, "E6.4.18", {"start": v(-110.83, 36.01) * mm, "end": v(-42.33, -13.75) * mm});
            skPoint(sketch, "E6.4.19", {"position": v(-62.47, -32.3) * mm});
            skPoint(sketch, "E6.4.20", {"position": v(-110.83, -36.01) * mm});
            skLineSegment(sketch, "E6.4.21", {"start": v(-153.16, -94.28) * mm, "end": v(-179.33, -13.75) * mm});
            skPoint(sketch, "E6.4.22", {"position": v(-110.83, -74.86) * mm});
            skPoint(sketch, "E6.4.23", {"position": v(-85.3, -32.3) * mm});
            skPoint(sketch, "E6.4.24", {"position": v(-122.25, -59.14) * mm});
            skPoint(sketch, "E6.4.25", {"position": v(-145.08, 11.13) * mm});
            skPoint(sketch, "E6.4.26", {"position": v(-106.47, -10.59) * mm});
            skLineSegment(sketch, "E6.4.27", {"start": v(-179.33, -13.75) * mm, "end": v(-110.83, 36.01) * mm});
            skPoint(sketch, "E6.4.28", {"position": v(-92.36, -54.02) * mm});
            skPoint(sketch, "E6.4.29", {"position": v(-136.36, -32.3) * mm});
            skPoint(sketch, "E6.4.30", {"position": v(-129.3, -80.86) * mm});
            skPoint(sketch, "E6.4.31", {"position": v(-55.42, -54.02) * mm});
            skLineSegment(sketch, "E6.4.32", {"start": v(-42.33, -13.75) * mm, "end": v(-68.5, -94.28) * mm});
            skPoint(sketch, "E6.4.33", {"position": v(-147.77, -48.01) * mm});
            skPoint(sketch, "E6.4.34", {"position": v(-73.89, -48.01) * mm});
            skPoint(sketch, "E6.4.35", {"position": v(-88, -4.58) * mm});
            skPoint(sketch, "E6.4.36", {"position": v(-85.3, -32.3) * mm});
            skPoint(sketch, "E6.4.37", {"position": v(-69.53, -10.59) * mm});
            skPoint(sketch, "E6.4.38", {"position": v(-92.36, -54.02) * mm});
            skPoint(sketch, "E6.4.39", {"position": v(-136.36, -32.3) * mm});
            skPoint(sketch, "E6.4.40", {"position": v(-145.08, 11.13) * mm});
            skPoint(sketch, "E6.4.41", {"position": v(-110.83, -94.28) * mm});
            skPoint(sketch, "E6.4.42", {"position": v(-133.66, -24) * mm});
            skPoint(sketch, "E6.4.43", {"position": v(-99.41, -59.14) * mm});
            skPoint(sketch, "E6.4.44", {"position": v(-147.77, -67.44) * mm});
            skPoint(sketch, "E6.4.45", {"position": v(-122.25, -59.14) * mm});
            skPoint(sketch, "E6.4.46", {"position": v(-55.42, -54.02) * mm});
            skPoint(sketch, "E6.4.47", {"position": v(-62.47, -32.3) * mm});
            skPoint(sketch, "E6.4.48", {"position": v(-99.41, 11.13) * mm});
            skPoint(sketch, "E6.4.49", {"position": v(-129.3, -54.02) * mm});
            skPoint(sketch, "E6.4.50", {"position": v(-106.47, -10.59) * mm});
            skPoint(sketch, "E6.4.51", {"position": v(-73.89, -67.44) * mm});
            skPoint(sketch, "E6.4.52", {"position": v(-152.13, -10.59) * mm});
            skPoint(sketch, "E6.4.53", {"position": v(-129.3, -80.86) * mm});
            skPoint(sketch, "E6.4.54", {"position": v(-88, -24) * mm});
            skPoint(sketch, "E6.4.55", {"position": v(-122.25, 11.13) * mm});
            skPoint(sketch, "E6.4.56", {"position": v(-92.36, -80.86) * mm});
            skPoint(sketch, "E6.4.57", {"position": v(-115.2, -10.59) * mm});
            skPoint(sketch, "E6.4.58", {"position": v(-159.19, -32.3) * mm});
            skPoint(sketch, "E6.4.59", {"position": v(-166.25, -54.02) * mm});
            skPoint(sketch, "E6.4.60", {"position": v(-76.58, 11.13) * mm});
            skLineSegment(sketch, "E6.4.61", {"start": v(-118.44, -85.33) * mm, "end": v(-110.83, -79.8) * mm});
            skPoint(sketch, "E6.4.62", {"position": v(-136.36, -32.3) * mm});
            skLineSegment(sketch, "E6.4.63", {"start": v(-81.5, -58.49) * mm, "end": v(-73.89, -52.96) * mm});
            skLineSegment(sketch, "E6.4.64", {"start": v(-96.72, -94.28) * mm, "end": v(-124.94, -94.28) * mm});
            skLineSegment(sketch, "E6.4.65", {"start": v(-88, -67.44) * mm, "end": v(-96.72, -94.28) * mm});
            skLineSegment(sketch, "E6.4.66", {"start": v(-95.6, -15.06) * mm, "end": v(-88, -9.53) * mm});
            skLineSegment(sketch, "E6.4.67", {"start": v(-76.8, -44.01) * mm, "end": v(-86.2, -44.01) * mm});
            skLineSegment(sketch, "E6.4.68", {"start": v(-138.37, -6.11) * mm, "end": v(-141.27, -15.06) * mm});
            skLineSegment(sketch, "E6.4.69", {"start": v(-118.44, -56.38) * mm, "end": v(-110.83, -61.9) * mm});
            skPoint(sketch, "E6.4.70", {"position": v(-62.47, -32.3) * mm});
            skLineSegment(sketch, "E6.4.71", {"start": v(-73.89, -24) * mm, "end": v(-102.1, -24) * mm});
            skLineSegment(sketch, "E6.4.72", {"start": v(-88, -67.44) * mm, "end": v(-96.72, -40.6) * mm});
            skPoint(sketch, "E6.4.73", {"position": v(-92.36, -80.86) * mm});
            skPoint(sketch, "E6.4.74", {"position": v(-115.2, -10.59) * mm});
            skLineSegment(sketch, "E6.4.75", {"start": v(-123.14, -70.85) * mm, "end": v(-115.53, -76.38) * mm});
            skLineSegment(sketch, "E6.4.76", {"start": v(-65.17, 2.83) * mm, "end": v(-73.89, -24) * mm});
            skLineSegment(sketch, "E6.4.77", {"start": v(-100.31, -0.58) * mm, "end": v(-92.7, -6.11) * mm});
            skLineSegment(sketch, "E6.4.78", {"start": v(-88, 8.36) * mm, "end": v(-90.9, -0.58) * mm});
            skLineSegment(sketch, "E6.4.79", {"start": v(-136.57, -0.58) * mm, "end": v(-145.98, -0.58) * mm});
            skLineSegment(sketch, "E6.4.80", {"start": v(-144.87, -44.01) * mm, "end": v(-147.77, -35.07) * mm});
            skLineSegment(sketch, "E6.4.81", {"start": v(-121.35, -0.58) * mm, "end": v(-130.76, -0.58) * mm});
            skLineSegment(sketch, "E6.4.82", {"start": v(-141.27, -15.06) * mm, "end": v(-150.68, -15.06) * mm});
            skLineSegment(sketch, "E6.4.83", {"start": v(-110.83, -79.8) * mm, "end": v(-103.22, -85.33) * mm});
            skLineSegment(sketch, "E6.4.84", {"start": v(-107.92, -6.11) * mm, "end": v(-100.31, -0.58) * mm});
            skPoint(sketch, "E6.4.85", {"position": v(-76.58, 11.13) * mm});
            skLineSegment(sketch, "E6.4.86", {"start": v(-88, -9.53) * mm, "end": v(-80.39, -15.06) * mm});
            skLineSegment(sketch, "E6.4.87", {"start": v(-69.18, -49.54) * mm, "end": v(-61.57, -44.01) * mm});
            skLineSegment(sketch, "E6.4.88", {"start": v(-119.55, -24) * mm, "end": v(-147.77, -24) * mm});
            skLineSegment(sketch, "E6.4.89", {"start": v(-147.77, -35.07) * mm, "end": v(-150.68, -44.01) * mm});
            skLineSegment(sketch, "E6.4.90", {"start": v(-133.66, 8.36) * mm, "end": v(-136.57, -0.58) * mm});
            skPoint(sketch, "E6.4.91", {"position": v(-69.53, -10.59) * mm});
            skLineSegment(sketch, "E6.4.92", {"start": v(-130.76, -76.38) * mm, "end": v(-123.14, -70.85) * mm});
            skLineSegment(sketch, "E6.4.93", {"start": v(-140.16, -58.49) * mm, "end": v(-143.07, -67.44) * mm});
            skPoint(sketch, "E6.4.94", {"position": v(-110.83, -94.28) * mm});
            skLineSegment(sketch, "E6.4.95", {"start": v(-147.77, -24) * mm, "end": v(-156.5, 2.83) * mm});
            skLineSegment(sketch, "E6.4.96", {"start": v(-59.78, -67.44) * mm, "end": v(-88, -67.44) * mm});
            skLineSegment(sketch, "E6.4.97", {"start": v(-126.05, -15.06) * mm, "end": v(-128.96, -6.11) * mm});
            skLineSegment(sketch, "E6.4.98", {"start": v(-141.27, -15.06) * mm, "end": v(-133.66, -9.53) * mm});
            skLineSegment(sketch, "E6.4.99", {"start": v(-155.38, -29.54) * mm, "end": v(-147.77, -35.07) * mm});
            skLineSegment(sketch, "E6.4.100", {"start": v(-115.53, -76.38) * mm, "end": v(-118.44, -85.33) * mm});
            skPoint(sketch, "E6.4.101", {"position": v(-145.08, 11.13) * mm});
            skPoint(sketch, "E6.4.102", {"position": v(-152.13, -10.59) * mm});
            skLineSegment(sketch, "E6.4.103", {"start": v(-113.74, -70.85) * mm, "end": v(-123.14, -70.85) * mm});
            skLineSegment(sketch, "E6.4.104", {"start": v(-140.16, -58.49) * mm, "end": v(-143.07, -49.54) * mm});
            skLineSegment(sketch, "E6.4.105", {"start": v(-98.52, -70.85) * mm, "end": v(-107.92, -70.85) * mm});
            skPoint(sketch, "E6.4.106", {"position": v(-129.3, -80.86) * mm});
            skPoint(sketch, "E6.4.107", {"position": v(-129.3, -54.02) * mm});
            skLineSegment(sketch, "E6.4.108", {"start": v(-102.1, -24) * mm, "end": v(-110.83, 2.83) * mm});
            skPoint(sketch, "E6.4.109", {"position": v(-147.77, -67.44) * mm});
            skPoint(sketch, "E6.4.110", {"position": v(-92.36, -54.02) * mm});
            skLineSegment(sketch, "E6.4.111", {"start": v(-92.7, -6.11) * mm, "end": v(-95.6, -15.06) * mm});
            skLineSegment(sketch, "E6.4.112", {"start": v(-161.88, -67.44) * mm, "end": v(-170.6, -40.6) * mm});
            skLineSegment(sketch, "E6.4.113", {"start": v(-143.07, -49.54) * mm, "end": v(-135.46, -44.01) * mm});
            skLineSegment(sketch, "E6.4.114", {"start": v(-73.89, -52.96) * mm, "end": v(-66.28, -58.49) * mm});
            skLineSegment(sketch, "E6.4.115", {"start": v(-73.89, -35.07) * mm, "end": v(-76.8, -44.01) * mm});
            skLineSegment(sketch, "E6.4.116", {"start": v(-51.05, -40.6) * mm, "end": v(-59.78, -67.44) * mm});
            skLineSegment(sketch, "E6.4.117", {"start": v(-147.77, -52.96) * mm, "end": v(-140.16, -58.49) * mm});
            skLineSegment(sketch, "E6.4.118", {"start": v(-106.13, -76.38) * mm, "end": v(-98.52, -70.85) * mm});
            skLineSegment(sketch, "E6.4.119", {"start": v(-156.5, 2.83) * mm, "end": v(-133.66, 19.42) * mm});
            skLineSegment(sketch, "E6.4.120", {"start": v(-150.68, -44.01) * mm, "end": v(-160.09, -44.01) * mm});
            skLineSegment(sketch, "E6.4.121", {"start": v(-66.28, -58.49) * mm, "end": v(-69.18, -49.54) * mm});
            skLineSegment(sketch, "E6.4.122", {"start": v(-85.1, -0.58) * mm, "end": v(-88, 8.36) * mm});
            skLineSegment(sketch, "E6.4.123", {"start": v(-155.38, -58.49) * mm, "end": v(-147.77, -52.96) * mm});
            skLineSegment(sketch, "E6.4.124", {"start": v(-75.68, -0.58) * mm, "end": v(-85.1, -0.58) * mm});
            skLineSegment(sketch, "E6.4.125", {"start": v(-110.83, 2.83) * mm, "end": v(-88, 19.42) * mm});
            skLineSegment(sketch, "E6.4.126", {"start": v(-107.92, -70.85) * mm, "end": v(-110.83, -61.9) * mm});
            skPoint(sketch, "E6.4.127", {"position": v(-55.42, -54.02) * mm});
            skLineSegment(sketch, "E6.4.128", {"start": v(-124.94, -40.6) * mm, "end": v(-133.66, -67.44) * mm});
            skLineSegment(sketch, "E6.4.129", {"start": v(-133.66, -67.44) * mm, "end": v(-161.88, -67.44) * mm});
            skLineSegment(sketch, "E6.4.130", {"start": v(-141.27, 13.9) * mm, "end": v(-133.66, 8.36) * mm});
            skPoint(sketch, "E6.4.131", {"position": v(-99.41, 11.13) * mm});
            skLineSegment(sketch, "E6.4.132", {"start": v(-133.66, 19.42) * mm, "end": v(-110.83, 2.83) * mm});
            skLineSegment(sketch, "E6.4.133", {"start": v(-170.6, -40.6) * mm, "end": v(-147.77, -24) * mm});
            skLineSegment(sketch, "E6.4.134", {"start": v(-130.76, -0.58) * mm, "end": v(-133.66, 8.36) * mm});
            skLineSegment(sketch, "E6.4.135", {"start": v(-155.38, -58.49) * mm, "end": v(-164.8, -58.49) * mm});
            skPoint(sketch, "E6.4.136", {"position": v(-122.25, 11.13) * mm});
            skLineSegment(sketch, "E6.4.137", {"start": v(-61.57, -44.01) * mm, "end": v(-70.98, -44.01) * mm});
            skLineSegment(sketch, "E6.4.138", {"start": v(-128.96, -6.11) * mm, "end": v(-121.35, -0.58) * mm});
            skLineSegment(sketch, "E6.4.139", {"start": v(-110.83, -50.85) * mm, "end": v(-88, -67.44) * mm});
            skLineSegment(sketch, "E6.4.140", {"start": v(-147.77, -24) * mm, "end": v(-124.94, -40.6) * mm});
            skLineSegment(sketch, "E6.4.141", {"start": v(-86.2, -44.01) * mm, "end": v(-78.6, -49.54) * mm});
            skPoint(sketch, "E6.4.142", {"position": v(-85.3, -32.3) * mm});
            skPoint(sketch, "E6.4.143", {"position": v(-106.47, -10.59) * mm});
            skLineSegment(sketch, "E6.4.144", {"start": v(-78.6, -49.54) * mm, "end": v(-81.5, -58.49) * mm});
            skLineSegment(sketch, "E6.4.145", {"start": v(-110.83, 2.83) * mm, "end": v(-119.55, -24) * mm});
            skLineSegment(sketch, "E6.4.146", {"start": v(-90.9, -0.58) * mm, "end": v(-100.31, -0.58) * mm});
            skLineSegment(sketch, "E6.4.147", {"start": v(-145.98, -0.58) * mm, "end": v(-138.37, -6.11) * mm});
            skLineSegment(sketch, "E6.4.148", {"start": v(-73.89, -24) * mm, "end": v(-51.05, -40.6) * mm});
            skLineSegment(sketch, "E6.4.149", {"start": v(-110.83, -61.9) * mm, "end": v(-113.74, -70.85) * mm});
            skLineSegment(sketch, "E6.4.150", {"start": v(-81.5, -29.54) * mm, "end": v(-73.89, -35.07) * mm});
            skLineSegment(sketch, "E6.4.151", {"start": v(-80.39, -15.06) * mm, "end": v(-83.3, -6.11) * mm});
            skLineSegment(sketch, "E6.4.152", {"start": v(-88, 19.42) * mm, "end": v(-65.17, 2.83) * mm});
            skLineSegment(sketch, "E6.4.153", {"start": v(-133.66, -9.53) * mm, "end": v(-126.05, -15.06) * mm});
            skLineSegment(sketch, "E6.4.154", {"start": v(-126.05, -15.06) * mm, "end": v(-128.96, -24) * mm});
            skLineSegment(sketch, "E6.4.155", {"start": v(-135.46, -44.01) * mm, "end": v(-144.87, -44.01) * mm});
            skLineSegment(sketch, "E6.4.156", {"start": v(-133.66, -67.44) * mm, "end": v(-110.83, -50.85) * mm});
            skLineSegment(sketch, "E6.4.157", {"start": v(-103.22, -85.33) * mm, "end": v(-106.13, -76.38) * mm});
            skLineSegment(sketch, "E6.4.158", {"start": v(-96.72, -40.6) * mm, "end": v(-73.89, -24) * mm});
            skLineSegment(sketch, "E6.4.159", {"start": v(-103.22, -85.33) * mm, "end": v(-106.13, -94.28) * mm});
            skLineSegment(sketch, "E6.4.160", {"start": v(-70.98, -44.01) * mm, "end": v(-73.89, -35.07) * mm});
            skLineSegment(sketch, "E6.4.161", {"start": v(-152.48, -49.54) * mm, "end": v(-155.38, -58.49) * mm});
            skPoint(sketch, "E6.4.162", {"position": v(-88, -24) * mm});
            skPoint(sketch, "E6.4.163", {"position": v(-99.41, -59.14) * mm});
            skLineSegment(sketch, "E6.4.164", {"start": v(-83.3, -6.11) * mm, "end": v(-75.68, -0.58) * mm});
            skLineSegment(sketch, "E6.4.165", {"start": v(-124.94, -94.28) * mm, "end": v(-133.66, -67.44) * mm});
            skLineSegment(sketch, "E6.4.166", {"start": v(-81.5, -58.49) * mm, "end": v(-90.9, -58.49) * mm});
            skPoint(sketch, "E6.4.167", {"position": v(-133.66, -24) * mm});
            skLineSegment(sketch, "E6.4.168", {"start": v(-160.09, -44.01) * mm, "end": v(-152.48, -49.54) * mm});
            skPoint(sketch, "E6.4.169", {"position": v(-159.19, -32.3) * mm});
            skPoint(sketch, "E6.4.170", {"position": v(-122.25, -59.14) * mm});
            skPoint(sketch, "E6.4.171", {"position": v(-73.89, -67.44) * mm});
            skPoint(sketch, "E6.4.172", {"position": v(-166.25, -54.02) * mm});
            skPoint(sketch, "E6.4.173", {"position": v(-122.25, 11.13) * mm});
            skPoint(sketch, "E6.4.174", {"position": v(-85.3, -32.3) * mm});
            skPoint(sketch, "E6.4.175", {"position": v(-166.25, -54.02) * mm});
            skPoint(sketch, "E6.4.176", {"position": v(-88, -24) * mm});
            skPoint(sketch, "E6.4.177", {"position": v(-69.53, -10.59) * mm});
            skPoint(sketch, "E6.4.178", {"position": v(-159.19, -32.3) * mm});
            skPoint(sketch, "E6.4.179", {"position": v(-133.66, -24) * mm});
            skPoint(sketch, "E6.4.180", {"position": v(-99.41, 11.13) * mm});
            skPoint(sketch, "E6.4.181", {"position": v(-122.25, -59.14) * mm});
            skPoint(sketch, "E6.4.182", {"position": v(-99.41, -59.14) * mm});
            skPoint(sketch, "E6.4.183", {"position": v(-92.36, -80.86) * mm});
            skPoint(sketch, "E6.4.184", {"position": v(-152.13, -10.59) * mm});
            skPoint(sketch, "E6.4.185", {"position": v(-73.89, -67.44) * mm});
            skPoint(sketch, "E6.4.186", {"position": v(-62.47, -32.3) * mm});
            skPoint(sketch, "E6.4.187", {"position": v(-129.3, -54.02) * mm});
            skPoint(sketch, "E6.4.188", {"position": v(-147.77, -67.44) * mm});
            skPoint(sketch, "E6.4.189", {"position": v(-129.3, -80.86) * mm});
            skPoint(sketch, "E6.4.190", {"position": v(-76.58, 11.13) * mm});
            skPoint(sketch, "E6.4.191", {"position": v(-115.2, -10.59) * mm});
            skPoint(sketch, "E6.4.192", {"position": v(-136.36, -32.3) * mm});
            skPoint(sketch, "E6.4.193", {"position": v(-110.83, -94.28) * mm});
            skPoint(sketch, "E6.4.194", {"position": v(-92.36, -54.02) * mm});
            skPoint(sketch, "E6.4.195", {"position": v(-145.08, 11.13) * mm});
            skPoint(sketch, "E6.4.196", {"position": v(-55.42, -54.02) * mm});
            skPoint(sketch, "E6.4.197", {"position": v(-106.47, -10.59) * mm});
            skLineSegment(sketch, "E6.4.198", {"start": v(-73.89, -35.07) * mm, "end": v(-66.28, -29.54) * mm});
            skLineSegment(sketch, "E6.4.199", {"start": v(-66.28, -29.54) * mm, "end": v(-58.67, -35.07) * mm});
            skLineSegment(sketch, "E6.4.200", {"start": v(-132.55, -35.07) * mm, "end": v(-135.46, -44.01) * mm});
            skLineSegment(sketch, "E6.4.201", {"start": v(-95.6, -61.9) * mm, "end": v(-98.52, -70.85) * mm});
            skLineSegment(sketch, "E6.4.202", {"start": v(-56.87, -58.49) * mm, "end": v(-66.28, -58.49) * mm});
            skLineSegment(sketch, "E6.4.203", {"start": v(-106.13, -94.28) * mm, "end": v(-115.53, -94.28) * mm});
            skLineSegment(sketch, "E6.4.204", {"start": v(-92.7, -24) * mm, "end": v(-95.6, -15.06) * mm});
            skLineSegment(sketch, "E6.4.205", {"start": v(-66.28, -58.49) * mm, "end": v(-69.18, -67.44) * mm});
            skLineSegment(sketch, "E6.4.206", {"start": v(-86.2, -44.01) * mm, "end": v(-89.1, -35.07) * mm});
            skLineSegment(sketch, "E6.4.207", {"start": v(-127.85, -49.54) * mm, "end": v(-130.76, -58.49) * mm});
            skLineSegment(sketch, "E6.4.208", {"start": v(-98.52, -70.85) * mm, "end": v(-90.9, -76.38) * mm});
            skLineSegment(sketch, "E6.4.209", {"start": v(-126.05, 13.9) * mm, "end": v(-118.44, 8.36) * mm});
            skLineSegment(sketch, "E6.4.210", {"start": v(-167.7, -49.54) * mm, "end": v(-160.09, -44.01) * mm});
            skLineSegment(sketch, "E6.4.211", {"start": v(-93.81, -85.33) * mm, "end": v(-103.22, -85.33) * mm});
            skLineSegment(sketch, "E6.4.212", {"start": v(-145.98, -0.58) * mm, "end": v(-148.88, 8.36) * mm});
            skLineSegment(sketch, "E6.4.213", {"start": v(-128.96, -24) * mm, "end": v(-138.37, -24) * mm});
            skLineSegment(sketch, "E6.4.214", {"start": v(-113.74, -6.11) * mm, "end": v(-116.64, -15.06) * mm});
            skLineSegment(sketch, "E6.4.215", {"start": v(-152.48, -67.44) * mm, "end": v(-155.38, -58.49) * mm});
            skLineSegment(sketch, "E6.4.216", {"start": v(-72.78, 8.36) * mm, "end": v(-75.68, -0.58) * mm});
            skLineSegment(sketch, "E6.4.217", {"start": v(-95.6, 13.9) * mm, "end": v(-88, 8.36) * mm});
            skLineSegment(sketch, "E6.4.218", {"start": v(-118.44, 8.36) * mm, "end": v(-121.35, -0.58) * mm});
            skLineSegment(sketch, "E6.4.219", {"start": v(-78.6, -67.44) * mm, "end": v(-81.5, -58.49) * mm});
            skLineSegment(sketch, "E6.4.220", {"start": v(-160.09, -44.01) * mm, "end": v(-163, -35.07) * mm});
            skLineSegment(sketch, "E6.4.221", {"start": v(-118.44, -85.33) * mm, "end": v(-127.85, -85.33) * mm});
            skLineSegment(sketch, "E6.4.222", {"start": v(-75.68, -0.58) * mm, "end": v(-68.07, -6.11) * mm});
            skLineSegment(sketch, "E6.4.223", {"start": v(-103.22, 8.36) * mm, "end": v(-95.6, 13.9) * mm});
            skLineSegment(sketch, "E6.4.224", {"start": v(-80.39, -15.06) * mm, "end": v(-83.3, -24) * mm});
            skLineSegment(sketch, "E6.4.225", {"start": v(-126.05, -61.9) * mm, "end": v(-118.44, -56.38) * mm});
            skLineSegment(sketch, "E6.4.226", {"start": v(-53.96, -49.54) * mm, "end": v(-56.87, -58.49) * mm});
            skLineSegment(sketch, "E6.4.227", {"start": v(-143.07, -67.44) * mm, "end": v(-152.48, -67.44) * mm});
            skLineSegment(sketch, "E6.4.228", {"start": v(-68.07, -6.11) * mm, "end": v(-70.98, -15.06) * mm});
            skLineSegment(sketch, "E6.4.229", {"start": v(-95.6, -15.06) * mm, "end": v(-105.02, -15.06) * mm});
            skLineSegment(sketch, "E6.4.230", {"start": v(-93.81, -49.54) * mm, "end": v(-86.2, -44.01) * mm});
            skLineSegment(sketch, "E6.4.231", {"start": v(-105.02, -15.06) * mm, "end": v(-107.92, -6.11) * mm});
            skLineSegment(sketch, "E6.4.232", {"start": v(-140.16, -29.54) * mm, "end": v(-132.55, -35.07) * mm});
            skLineSegment(sketch, "E6.4.233", {"start": v(-138.37, -24) * mm, "end": v(-141.27, -15.06) * mm});
            skLineSegment(sketch, "E6.4.234", {"start": v(-58.67, -35.07) * mm, "end": v(-61.57, -44.01) * mm});
            skLineSegment(sketch, "E6.4.235", {"start": v(-127.85, -85.33) * mm, "end": v(-130.76, -76.38) * mm});
            skLineSegment(sketch, "E6.4.236", {"start": v(-123.14, -70.85) * mm, "end": v(-126.05, -61.9) * mm});
            skLineSegment(sketch, "E6.4.237", {"start": v(-150.68, -15.06) * mm, "end": v(-153.59, -6.11) * mm});
            skLineSegment(sketch, "E6.4.238", {"start": v(-133.66, 8.36) * mm, "end": v(-126.05, 13.9) * mm});
            skLineSegment(sketch, "E6.4.239", {"start": v(-80.39, 13.9) * mm, "end": v(-72.78, 8.36) * mm});
            skLineSegment(sketch, "E6.4.240", {"start": v(-90.9, -58.49) * mm, "end": v(-93.81, -49.54) * mm});
            skLineSegment(sketch, "E6.4.241", {"start": v(-121.35, -0.58) * mm, "end": v(-113.74, -6.11) * mm});
            skLineSegment(sketch, "E6.4.242", {"start": v(-110.83, -61.9) * mm, "end": v(-103.22, -56.38) * mm});
            skLineSegment(sketch, "E6.4.243", {"start": v(-164.8, -58.49) * mm, "end": v(-167.7, -49.54) * mm});
            skLineSegment(sketch, "E6.4.244", {"start": v(-103.22, -56.38) * mm, "end": v(-95.6, -61.9) * mm});
            skLineSegment(sketch, "E6.4.245", {"start": v(-153.59, -6.11) * mm, "end": v(-145.98, -0.58) * mm});
            skLineSegment(sketch, "E6.4.246", {"start": v(-163, -35.07) * mm, "end": v(-155.38, -29.54) * mm});
            skLineSegment(sketch, "E6.4.247", {"start": v(-90.9, -76.38) * mm, "end": v(-93.81, -85.33) * mm});
            skLineSegment(sketch, "E6.4.248", {"start": v(-116.64, -15.06) * mm, "end": v(-126.05, -15.06) * mm});
            skLineSegment(sketch, "E6.4.249", {"start": v(-61.57, -44.01) * mm, "end": v(-53.96, -49.54) * mm});
            skLineSegment(sketch, "E6.4.250", {"start": v(-100.31, -0.58) * mm, "end": v(-103.22, 8.36) * mm});
            skLineSegment(sketch, "E6.4.251", {"start": v(-130.76, -58.49) * mm, "end": v(-140.16, -58.49) * mm});
            skLineSegment(sketch, "E6.4.252", {"start": v(-70.98, -15.06) * mm, "end": v(-80.39, -15.06) * mm});
            skLineSegment(sketch, "E6.4.253", {"start": v(-88, 8.36) * mm, "end": v(-80.39, 13.9) * mm});
            skLineSegment(sketch, "E6.4.254", {"start": v(-135.46, -44.01) * mm, "end": v(-127.85, -49.54) * mm});
            skLineSegment(sketch, "E6.4.255", {"start": v(-89.1, -35.07) * mm, "end": v(-81.5, -29.54) * mm});
            skLineSegment(sketch, "E6.4.256", {"start": v(-69.18, -67.44) * mm, "end": v(-78.6, -67.44) * mm});
            skLineSegment(sketch, "E6.4.257", {"start": v(-83.3, -24) * mm, "end": v(-92.7, -24) * mm});
            skLineSegment(sketch, "E6.4.258", {"start": v(-148.88, 8.36) * mm, "end": v(-141.27, 13.9) * mm});
            skLineSegment(sketch, "E6.4.259", {"start": v(-147.77, -35.07) * mm, "end": v(-140.16, -29.54) * mm});
            skLineSegment(sketch, "E6.4.260", {"start": v(-115.53, -94.28) * mm, "end": v(-118.44, -85.33) * mm});
            skPoint(sketch, "E6.center", {"position": v(0, 0) * mm});
            skSolve(sketch);
        }
        {
            var Q0;
            {var subQ9=sQuery(id+"F0.wireOp",EDGE,"E6.2.203");Q0=makeQuery(id+"F0.imprint","IMPRINT",FACE,{"disambiguationData":[TD([[makeQuery(id+"F0.imprint","IMPRINT",EDGE,{"derivedFrom":subQ9}),1.0]])]});}
            var Q1;
            {var subQ9=sQuery(id+"F0.wireOp",EDGE,"E6.1.203");Q1=makeQuery(id+"F0.imprint","IMPRINT",FACE,{"disambiguationData":[TD([[makeQuery(id+"F0.imprint","IMPRINT",EDGE,{"derivedFrom":subQ9}),1.0]])]});}
            var Q2;
            {var subQ10=sQuery(id+"F0.wireOp",EDGE,"E5.1.18");Q2=makeQuery(id+"F0.imprint","IMPRINT",FACE,{"disambiguationData":[TD([[makeQuery(id+"F0.imprint","IMPRINT",EDGE,{"derivedFrom":subQ10}),1.0]])]});}
            var Q3;
            {var subQ7=sQuery(id+"F0.wireOp",EDGE,"E5.4.18");Q3=makeQuery(id+"F0.imprint","IMPRINT",FACE,{"disambiguationData":[TD([[makeQuery(id+"F0.imprint","IMPRINT",EDGE,{"derivedFrom":subQ7}),1.0]])]});}
            var Q4;
            {var subQ9=sQuery(id+"F0.wireOp",EDGE,"E6.3.203");Q4=makeQuery(id+"F0.imprint","IMPRINT",FACE,{"disambiguationData":[TD([[makeQuery(id+"F0.imprint","IMPRINT",EDGE,{"derivedFrom":subQ9}),1.0]])]});}
            var Q5;
            {var subQ0=sQuery(id+"F0.wireOp",EDGE,"E6.3.227");Q5=makeQuery(id+"F0.imprint","IMPRINT",FACE,{"disambiguationData":[TD([[makeQuery(id+"F0.imprint","IMPRINT",EDGE,{"derivedFrom":subQ0}),1.0]])]});}
            var Q6;
            {var subQ3=sQuery(id+"F0.wireOp",EDGE,"E6.3.237");Q6=makeQuery(id+"F0.imprint","IMPRINT",FACE,{"disambiguationData":[TD([[makeQuery(id+"F0.imprint","IMPRINT",EDGE,{"derivedFrom":subQ3}),1.0]])]});}
            var Q7;
            {var subQ9=sQuery(id+"F0.wireOp",EDGE,"E6.3.209");Q7=makeQuery(id+"F0.imprint","IMPRINT",FACE,{"disambiguationData":[TD([[makeQuery(id+"F0.imprint","IMPRINT",EDGE,{"derivedFrom":subQ9}),1.0]])]});}
            var Q8;
            {var subQ3=sQuery(id+"F0.wireOp",EDGE,"E6.2.247");Q8=makeQuery(id+"F0.imprint","IMPRINT",FACE,{"disambiguationData":[TD([[makeQuery(id+"F0.imprint","IMPRINT",EDGE,{"derivedFrom":subQ3}),1.0]])]});}
            var Q9;
            {var subQ0=sQuery(id+"F0.wireOp",EDGE,"E6.2.227");Q9=makeQuery(id+"F0.imprint","IMPRINT",FACE,{"disambiguationData":[TD([[makeQuery(id+"F0.imprint","IMPRINT",EDGE,{"derivedFrom":subQ0}),1.0]])]});}
            var Q10;
            {var subQ3=sQuery(id+"F0.wireOp",EDGE,"E6.2.237");Q10=makeQuery(id+"F0.imprint","IMPRINT",FACE,{"disambiguationData":[TD([[makeQuery(id+"F0.imprint","IMPRINT",EDGE,{"derivedFrom":subQ3}),1.0]])]});}
            var Q11;
            {var subQ9=sQuery(id+"F0.wireOp",EDGE,"E6.2.209");Q11=makeQuery(id+"F0.imprint","IMPRINT",FACE,{"disambiguationData":[TD([[makeQuery(id+"F0.imprint","IMPRINT",EDGE,{"derivedFrom":subQ9}),1.0]])]});}
            var Q12;
            {var subQ3=sQuery(id+"F0.wireOp",EDGE,"E6.1.247");Q12=makeQuery(id+"F0.imprint","IMPRINT",FACE,{"disambiguationData":[TD([[makeQuery(id+"F0.imprint","IMPRINT",EDGE,{"derivedFrom":subQ3}),1.0]])]});}
            var Q13;
            {var subQ0=sQuery(id+"F0.wireOp",EDGE,"E6.1.227");Q13=makeQuery(id+"F0.imprint","IMPRINT",FACE,{"disambiguationData":[TD([[makeQuery(id+"F0.imprint","IMPRINT",EDGE,{"derivedFrom":subQ0}),1.0]])]});}
            var Q14;
            {var subQ3=sQuery(id+"F0.wireOp",EDGE,"E6.1.237");Q14=makeQuery(id+"F0.imprint","IMPRINT",FACE,{"disambiguationData":[TD([[makeQuery(id+"F0.imprint","IMPRINT",EDGE,{"derivedFrom":subQ3}),1.0]])]});}
            var Q15;
            {var subQ9=sQuery(id+"F0.wireOp",EDGE,"E6.1.209");Q15=makeQuery(id+"F0.imprint","IMPRINT",FACE,{"disambiguationData":[TD([[makeQuery(id+"F0.imprint","IMPRINT",EDGE,{"derivedFrom":subQ9}),1.0]])]});}
            var Q16;
            {var subQ3=sQuery(id+"F0.wireOp",EDGE,"E5.1.20");Q16=makeQuery(id+"F0.imprint","IMPRINT",FACE,{"disambiguationData":[TD([[makeQuery(id+"F0.imprint","IMPRINT",EDGE,{"derivedFrom":subQ3}),1.0]])]});}
            var Q17;
            {var subQ3=sQuery(id+"F0.wireOp",EDGE,"E4.1.1");Q17=makeQuery(id+"F0.imprint","IMPRINT",FACE,{"disambiguationData":[TD([[makeQuery(id+"F0.imprint","IMPRINT",EDGE,{"derivedFrom":subQ3}),1.0]])]});}
            var Q18;
            {var subQ3=sQuery(id+"F0.wireOp",EDGE,"E4.4.1");Q18=makeQuery(id+"F0.imprint","IMPRINT",FACE,{"disambiguationData":[TD([[makeQuery(id+"F0.imprint","IMPRINT",EDGE,{"derivedFrom":subQ3}),1.0]])]});}
            var Q19;
            {var subQ0=sQuery(id+"F0.wireOp",EDGE,"E5.3.20");Q19=makeQuery(id+"F0.imprint","IMPRINT",FACE,{"disambiguationData":[TD([[makeQuery(id+"F0.imprint","IMPRINT",EDGE,{"derivedFrom":subQ0}),1.0]])]});}
            var Q20;
            {var subQ3=sQuery(id+"F0.wireOp",EDGE,"E6.4.247");Q20=makeQuery(id+"F0.imprint","IMPRINT",FACE,{"disambiguationData":[TD([[makeQuery(id+"F0.imprint","IMPRINT",EDGE,{"derivedFrom":subQ3}),1.0]])]});}
            var Q21;
            {var subQ0=sQuery(id+"F0.wireOp",EDGE,"E6.4.227");Q21=makeQuery(id+"F0.imprint","IMPRINT",FACE,{"disambiguationData":[TD([[makeQuery(id+"F0.imprint","IMPRINT",EDGE,{"derivedFrom":subQ0}),1.0]])]});}
            var Q22;
            {var subQ3=sQuery(id+"F0.wireOp",EDGE,"E6.4.237");Q22=makeQuery(id+"F0.imprint","IMPRINT",FACE,{"disambiguationData":[TD([[makeQuery(id+"F0.imprint","IMPRINT",EDGE,{"derivedFrom":subQ3}),1.0]])]});}
            var Q23;
            {var subQ9=sQuery(id+"F0.wireOp",EDGE,"E6.4.209");Q23=makeQuery(id+"F0.imprint","IMPRINT",FACE,{"disambiguationData":[TD([[makeQuery(id+"F0.imprint","IMPRINT",EDGE,{"derivedFrom":subQ9}),1.0]])]});}
            var Q24;
            {var subQ3=sQuery(id+"F0.wireOp",EDGE,"E6.3.247");Q24=makeQuery(id+"F0.imprint","IMPRINT",FACE,{"disambiguationData":[TD([[makeQuery(id+"F0.imprint","IMPRINT",EDGE,{"derivedFrom":subQ3}),1.0]])]});}
            var Q25;
            {var subQ9=sQuery(id+"F0.wireOp",EDGE,"E6.3.199");Q25=makeQuery(id+"F0.imprint","IMPRINT",FACE,{"disambiguationData":[TD([[makeQuery(id+"F0.imprint","IMPRINT",EDGE,{"derivedFrom":subQ9}),1.0]])]});}
            var Q26;
            {var subQ9=sQuery(id+"F0.wireOp",EDGE,"E6.2.199");Q26=makeQuery(id+"F0.imprint","IMPRINT",FACE,{"disambiguationData":[TD([[makeQuery(id+"F0.imprint","IMPRINT",EDGE,{"derivedFrom":subQ9}),1.0]])]});}
            var Q27;
            {var subQ9=sQuery(id+"F0.wireOp",EDGE,"E6.1.199");Q27=makeQuery(id+"F0.imprint","IMPRINT",FACE,{"disambiguationData":[TD([[makeQuery(id+"F0.imprint","IMPRINT",EDGE,{"derivedFrom":subQ9}),1.0]])]});}
            var Q28;
            {var subQ0=sQuery(id+"F0.wireOp",EDGE,"E5.2.20");Q28=makeQuery(id+"F0.imprint","IMPRINT",FACE,{"disambiguationData":[TD([[makeQuery(id+"F0.imprint","IMPRINT",EDGE,{"derivedFrom":subQ0}),1.0]])]});}
            var Q29;
            {var subQ9=sQuery(id+"F0.wireOp",EDGE,"E6.4.199");Q29=makeQuery(id+"F0.imprint","IMPRINT",FACE,{"disambiguationData":[TD([[makeQuery(id+"F0.imprint","IMPRINT",EDGE,{"derivedFrom":subQ9}),1.0]])]});}
            var Q30;
            {var subQ3=sQuery(id+"F0.wireOp",EDGE,"E6.3.135");Q30=makeQuery(id+"F0.imprint","IMPRINT",FACE,{"disambiguationData":[TD([[makeQuery(id+"F0.imprint","IMPRINT",EDGE,{"derivedFrom":subQ3}),1.0]])]});}
            var Q31;
            {var subQ3=sQuery(id+"F0.wireOp",EDGE,"E6.3.210");Q31=makeQuery(id+"F0.imprint","IMPRINT",FACE,{"disambiguationData":[TD([[makeQuery(id+"F0.imprint","IMPRINT",EDGE,{"derivedFrom":subQ3}),1.0]])]});}
            var Q32;
            {var subQ0=sQuery(id+"F0.wireOp",EDGE,"E6.3.99");Q32=makeQuery(id+"F0.imprint","IMPRINT",FACE,{"disambiguationData":[TD([[makeQuery(id+"F0.imprint","IMPRINT",EDGE,{"derivedFrom":subQ0}),1.0]])]});}
            var Q33;
            {var subQ0=sQuery(id+"F0.wireOp",EDGE,"E6.3.82");Q33=makeQuery(id+"F0.imprint","IMPRINT",FACE,{"disambiguationData":[TD([[makeQuery(id+"F0.imprint","IMPRINT",EDGE,{"derivedFrom":subQ0}),1.0]])]});}
            var Q34;
            {var subQ4=sQuery(id+"F0.wireOp",EDGE,"E6.3.212");Q34=makeQuery(id+"F0.imprint","IMPRINT",FACE,{"disambiguationData":[TD([[makeQuery(id+"F0.imprint","IMPRINT",EDGE,{"derivedFrom":subQ4}),1.0]])]});}
            var Q35;
            {var subQ3=sQuery(id+"F0.wireOp",EDGE,"E6.3.130");Q35=makeQuery(id+"F0.imprint","IMPRINT",FACE,{"disambiguationData":[TD([[makeQuery(id+"F0.imprint","IMPRINT",EDGE,{"derivedFrom":subQ3}),1.0]])]});}
            var Q36;
            {var subQ3=sQuery(id+"F0.wireOp",EDGE,"E6.3.218");Q36=makeQuery(id+"F0.imprint","IMPRINT",FACE,{"disambiguationData":[TD([[makeQuery(id+"F0.imprint","IMPRINT",EDGE,{"derivedFrom":subQ3}),1.0]])]});}
            var Q37;
            {var subQ0=sQuery(id+"F0.wireOp",EDGE,"E6.3.84");Q37=makeQuery(id+"F0.imprint","IMPRINT",FACE,{"disambiguationData":[TD([[makeQuery(id+"F0.imprint","IMPRINT",EDGE,{"derivedFrom":subQ0}),1.0]])]});}
            var Q38;
            {var subQ3=sQuery(id+"F0.wireOp",EDGE,"E6.3.217");Q38=makeQuery(id+"F0.imprint","IMPRINT",FACE,{"disambiguationData":[TD([[makeQuery(id+"F0.imprint","IMPRINT",EDGE,{"derivedFrom":subQ3}),1.0]])]});}
            var Q39;
            {var subQ4=sQuery(id+"F0.wireOp",EDGE,"E6.2.202");Q39=makeQuery(id+"F0.imprint","IMPRINT",FACE,{"disambiguationData":[TD([[makeQuery(id+"F0.imprint","IMPRINT",EDGE,{"derivedFrom":subQ4}),1.0]])]});}
            var Q40;
            {var subQ3=sQuery(id+"F0.wireOp",EDGE,"E6.2.166");Q40=makeQuery(id+"F0.imprint","IMPRINT",FACE,{"disambiguationData":[TD([[makeQuery(id+"F0.imprint","IMPRINT",EDGE,{"derivedFrom":subQ3}),1.0]])]});}
            var Q41;
            {var subQ4=sQuery(id+"F0.wireOp",EDGE,"E6.2.201");Q41=makeQuery(id+"F0.imprint","IMPRINT",FACE,{"disambiguationData":[TD([[makeQuery(id+"F0.imprint","IMPRINT",EDGE,{"derivedFrom":subQ4}),1.0]])]});}
            var Q42;
            {var subQ3=sQuery(id+"F0.wireOp",EDGE,"E6.2.159");Q42=makeQuery(id+"F0.imprint","IMPRINT",FACE,{"disambiguationData":[TD([[makeQuery(id+"F0.imprint","IMPRINT",EDGE,{"derivedFrom":subQ3}),1.0]])]});}
            var Q43;
            {var subQ4=sQuery(id+"F0.wireOp",EDGE,"E6.2.221");Q43=makeQuery(id+"F0.imprint","IMPRINT",FACE,{"disambiguationData":[TD([[makeQuery(id+"F0.imprint","IMPRINT",EDGE,{"derivedFrom":subQ4}),1.0]])]});}
            var Q44;
            {var subQ0=sQuery(id+"F0.wireOp",EDGE,"E6.2.92");Q44=makeQuery(id+"F0.imprint","IMPRINT",FACE,{"disambiguationData":[TD([[makeQuery(id+"F0.imprint","IMPRINT",EDGE,{"derivedFrom":subQ0}),1.0]])]});}
            var Q45;
            {var subQ0=sQuery(id+"F0.wireOp",EDGE,"E6.2.93");Q45=makeQuery(id+"F0.imprint","IMPRINT",FACE,{"disambiguationData":[TD([[makeQuery(id+"F0.imprint","IMPRINT",EDGE,{"derivedFrom":subQ0}),1.0]])]});}
            var Q46;
            {var subQ3=sQuery(id+"F0.wireOp",EDGE,"E6.2.135");Q46=makeQuery(id+"F0.imprint","IMPRINT",FACE,{"disambiguationData":[TD([[makeQuery(id+"F0.imprint","IMPRINT",EDGE,{"derivedFrom":subQ3}),1.0]])]});}
            var Q47;
            {var subQ3=sQuery(id+"F0.wireOp",EDGE,"E6.2.210");Q47=makeQuery(id+"F0.imprint","IMPRINT",FACE,{"disambiguationData":[TD([[makeQuery(id+"F0.imprint","IMPRINT",EDGE,{"derivedFrom":subQ3}),1.0]])]});}
            var Q48;
            {var subQ0=sQuery(id+"F0.wireOp",EDGE,"E6.2.99");Q48=makeQuery(id+"F0.imprint","IMPRINT",FACE,{"disambiguationData":[TD([[makeQuery(id+"F0.imprint","IMPRINT",EDGE,{"derivedFrom":subQ0}),1.0]])]});}
            var Q49;
            {var subQ0=sQuery(id+"F0.wireOp",EDGE,"E6.2.82");Q49=makeQuery(id+"F0.imprint","IMPRINT",FACE,{"disambiguationData":[TD([[makeQuery(id+"F0.imprint","IMPRINT",EDGE,{"derivedFrom":subQ0}),1.0]])]});}
            var Q50;
            {var subQ4=sQuery(id+"F0.wireOp",EDGE,"E6.2.212");Q50=makeQuery(id+"F0.imprint","IMPRINT",FACE,{"disambiguationData":[TD([[makeQuery(id+"F0.imprint","IMPRINT",EDGE,{"derivedFrom":subQ4}),1.0]])]});}
            var Q51;
            {var subQ3=sQuery(id+"F0.wireOp",EDGE,"E6.2.130");Q51=makeQuery(id+"F0.imprint","IMPRINT",FACE,{"disambiguationData":[TD([[makeQuery(id+"F0.imprint","IMPRINT",EDGE,{"derivedFrom":subQ3}),1.0]])]});}
            var Q52;
            {var subQ3=sQuery(id+"F0.wireOp",EDGE,"E6.2.218");Q52=makeQuery(id+"F0.imprint","IMPRINT",FACE,{"disambiguationData":[TD([[makeQuery(id+"F0.imprint","IMPRINT",EDGE,{"derivedFrom":subQ3}),1.0]])]});}
            var Q53;
            {var subQ0=sQuery(id+"F0.wireOp",EDGE,"E6.2.84");Q53=makeQuery(id+"F0.imprint","IMPRINT",FACE,{"disambiguationData":[TD([[makeQuery(id+"F0.imprint","IMPRINT",EDGE,{"derivedFrom":subQ0}),1.0]])]});}
            var Q54;
            {var subQ3=sQuery(id+"F0.wireOp",EDGE,"E6.2.217");Q54=makeQuery(id+"F0.imprint","IMPRINT",FACE,{"disambiguationData":[TD([[makeQuery(id+"F0.imprint","IMPRINT",EDGE,{"derivedFrom":subQ3}),1.0]])]});}
            var Q55;
            {var subQ4=sQuery(id+"F0.wireOp",EDGE,"E6.1.202");Q55=makeQuery(id+"F0.imprint","IMPRINT",FACE,{"disambiguationData":[TD([[makeQuery(id+"F0.imprint","IMPRINT",EDGE,{"derivedFrom":subQ4}),1.0]])]});}
            var Q56;
            {var subQ3=sQuery(id+"F0.wireOp",EDGE,"E6.1.166");Q56=makeQuery(id+"F0.imprint","IMPRINT",FACE,{"disambiguationData":[TD([[makeQuery(id+"F0.imprint","IMPRINT",EDGE,{"derivedFrom":subQ3}),1.0]])]});}
            var Q57;
            {var subQ4=sQuery(id+"F0.wireOp",EDGE,"E6.1.201");Q57=makeQuery(id+"F0.imprint","IMPRINT",FACE,{"disambiguationData":[TD([[makeQuery(id+"F0.imprint","IMPRINT",EDGE,{"derivedFrom":subQ4}),1.0]])]});}
            var Q58;
            {var subQ3=sQuery(id+"F0.wireOp",EDGE,"E6.1.159");Q58=makeQuery(id+"F0.imprint","IMPRINT",FACE,{"disambiguationData":[TD([[makeQuery(id+"F0.imprint","IMPRINT",EDGE,{"derivedFrom":subQ3}),1.0]])]});}
            var Q59;
            {var subQ4=sQuery(id+"F0.wireOp",EDGE,"E6.1.221");Q59=makeQuery(id+"F0.imprint","IMPRINT",FACE,{"disambiguationData":[TD([[makeQuery(id+"F0.imprint","IMPRINT",EDGE,{"derivedFrom":subQ4}),1.0]])]});}
            var Q60;
            {var subQ0=sQuery(id+"F0.wireOp",EDGE,"E6.1.92");Q60=makeQuery(id+"F0.imprint","IMPRINT",FACE,{"disambiguationData":[TD([[makeQuery(id+"F0.imprint","IMPRINT",EDGE,{"derivedFrom":subQ0}),1.0]])]});}
            var Q61;
            {var subQ0=sQuery(id+"F0.wireOp",EDGE,"E6.1.93");Q61=makeQuery(id+"F0.imprint","IMPRINT",FACE,{"disambiguationData":[TD([[makeQuery(id+"F0.imprint","IMPRINT",EDGE,{"derivedFrom":subQ0}),1.0]])]});}
            var Q62;
            {var subQ3=sQuery(id+"F0.wireOp",EDGE,"E6.1.135");Q62=makeQuery(id+"F0.imprint","IMPRINT",FACE,{"disambiguationData":[TD([[makeQuery(id+"F0.imprint","IMPRINT",EDGE,{"derivedFrom":subQ3}),1.0]])]});}
            var Q63;
            {var subQ3=sQuery(id+"F0.wireOp",EDGE,"E6.1.210");Q63=makeQuery(id+"F0.imprint","IMPRINT",FACE,{"disambiguationData":[TD([[makeQuery(id+"F0.imprint","IMPRINT",EDGE,{"derivedFrom":subQ3}),1.0]])]});}
            var Q64;
            {var subQ0=sQuery(id+"F0.wireOp",EDGE,"E6.1.99");Q64=makeQuery(id+"F0.imprint","IMPRINT",FACE,{"disambiguationData":[TD([[makeQuery(id+"F0.imprint","IMPRINT",EDGE,{"derivedFrom":subQ0}),1.0]])]});}
            var Q65;
            {var subQ0=sQuery(id+"F0.wireOp",EDGE,"E6.1.82");Q65=makeQuery(id+"F0.imprint","IMPRINT",FACE,{"disambiguationData":[TD([[makeQuery(id+"F0.imprint","IMPRINT",EDGE,{"derivedFrom":subQ0}),1.0]])]});}
            var Q66;
            {var subQ4=sQuery(id+"F0.wireOp",EDGE,"E6.1.212");Q66=makeQuery(id+"F0.imprint","IMPRINT",FACE,{"disambiguationData":[TD([[makeQuery(id+"F0.imprint","IMPRINT",EDGE,{"derivedFrom":subQ4}),1.0]])]});}
            var Q67;
            {var subQ3=sQuery(id+"F0.wireOp",EDGE,"E6.1.130");Q67=makeQuery(id+"F0.imprint","IMPRINT",FACE,{"disambiguationData":[TD([[makeQuery(id+"F0.imprint","IMPRINT",EDGE,{"derivedFrom":subQ3}),1.0]])]});}
            var Q68;
            {var subQ3=sQuery(id+"F0.wireOp",EDGE,"E6.1.218");Q68=makeQuery(id+"F0.imprint","IMPRINT",FACE,{"disambiguationData":[TD([[makeQuery(id+"F0.imprint","IMPRINT",EDGE,{"derivedFrom":subQ3}),1.0]])]});}
            var Q69;
            {var subQ0=sQuery(id+"F0.wireOp",EDGE,"E6.1.84");Q69=makeQuery(id+"F0.imprint","IMPRINT",FACE,{"disambiguationData":[TD([[makeQuery(id+"F0.imprint","IMPRINT",EDGE,{"derivedFrom":subQ0}),1.0]])]});}
            var Q70;
            {var subQ3=sQuery(id+"F0.wireOp",EDGE,"E6.1.217");Q70=makeQuery(id+"F0.imprint","IMPRINT",FACE,{"disambiguationData":[TD([[makeQuery(id+"F0.imprint","IMPRINT",EDGE,{"derivedFrom":subQ3}),1.0]])]});}
            var Q71;
            {var subQ4=sQuery(id+"F0.wireOp",EDGE,"E6.1.216");Q71=makeQuery(id+"F0.imprint","IMPRINT",FACE,{"disambiguationData":[TD([[makeQuery(id+"F0.imprint","IMPRINT",EDGE,{"derivedFrom":subQ4}),1.0]])]});}
            var Q72;
            {var subQ3=sQuery(id+"F0.wireOp",EDGE,"E6.1.224");Q72=makeQuery(id+"F0.imprint","IMPRINT",FACE,{"disambiguationData":[TD([[makeQuery(id+"F0.imprint","IMPRINT",EDGE,{"derivedFrom":subQ3}),1.0]])]});}
            var Q73;
            {var subQ4=sQuery(id+"F0.wireOp",EDGE,"E6.1.150");Q73=makeQuery(id+"F0.imprint","IMPRINT",FACE,{"disambiguationData":[TD([[makeQuery(id+"F0.imprint","IMPRINT",EDGE,{"derivedFrom":subQ4}),1.0]])]});}
            var Q74;
            {var subQ4=sQuery(id+"F0.wireOp",EDGE,"E6.1.234");Q74=makeQuery(id+"F0.imprint","IMPRINT",FACE,{"disambiguationData":[TD([[makeQuery(id+"F0.imprint","IMPRINT",EDGE,{"derivedFrom":subQ4}),1.0]])]});}
            var Q75;
            {var subQ4=sQuery(id+"F0.wireOp",EDGE,"E6.2.216");Q75=makeQuery(id+"F0.imprint","IMPRINT",FACE,{"disambiguationData":[TD([[makeQuery(id+"F0.imprint","IMPRINT",EDGE,{"derivedFrom":subQ4}),1.0]])]});}
            var Q76;
            {var subQ3=sQuery(id+"F0.wireOp",EDGE,"E6.2.224");Q76=makeQuery(id+"F0.imprint","IMPRINT",FACE,{"disambiguationData":[TD([[makeQuery(id+"F0.imprint","IMPRINT",EDGE,{"derivedFrom":subQ3}),1.0]])]});}
            var Q77;
            {var subQ4=sQuery(id+"F0.wireOp",EDGE,"E6.2.150");Q77=makeQuery(id+"F0.imprint","IMPRINT",FACE,{"disambiguationData":[TD([[makeQuery(id+"F0.imprint","IMPRINT",EDGE,{"derivedFrom":subQ4}),1.0]])]});}
            var Q78;
            {var subQ4=sQuery(id+"F0.wireOp",EDGE,"E6.2.234");Q78=makeQuery(id+"F0.imprint","IMPRINT",FACE,{"disambiguationData":[TD([[makeQuery(id+"F0.imprint","IMPRINT",EDGE,{"derivedFrom":subQ4}),1.0]])]});}
            var Q79;
            {var subQ4=sQuery(id+"F0.wireOp",EDGE,"E6.3.216");Q79=makeQuery(id+"F0.imprint","IMPRINT",FACE,{"disambiguationData":[TD([[makeQuery(id+"F0.imprint","IMPRINT",EDGE,{"derivedFrom":subQ4}),1.0]])]});}
            var Q80;
            {var subQ3=sQuery(id+"F0.wireOp",EDGE,"E6.3.224");Q80=makeQuery(id+"F0.imprint","IMPRINT",FACE,{"disambiguationData":[TD([[makeQuery(id+"F0.imprint","IMPRINT",EDGE,{"derivedFrom":subQ3}),1.0]])]});}
            var Q81;
            {var subQ4=sQuery(id+"F0.wireOp",EDGE,"E6.3.150");Q81=makeQuery(id+"F0.imprint","IMPRINT",FACE,{"disambiguationData":[TD([[makeQuery(id+"F0.imprint","IMPRINT",EDGE,{"derivedFrom":subQ4}),1.0]])]});}
            var Q82;
            {var subQ4=sQuery(id+"F0.wireOp",EDGE,"E6.3.234");Q82=makeQuery(id+"F0.imprint","IMPRINT",FACE,{"disambiguationData":[TD([[makeQuery(id+"F0.imprint","IMPRINT",EDGE,{"derivedFrom":subQ4}),1.0]])]});}
            var Q83;
            {var subQ0=sQuery(id+"F0.wireOp",EDGE,"E6.2.69");Q83=makeQuery(id+"F0.imprint","IMPRINT",FACE,{"disambiguationData":[TD([[makeQuery(id+"F0.imprint","IMPRINT",EDGE,{"derivedFrom":subQ0}),1.0]])]});}
            var Q84;
            {var subQ4=sQuery(id+"F0.wireOp",EDGE,"E6.2.200");Q84=makeQuery(id+"F0.imprint","IMPRINT",FACE,{"disambiguationData":[TD([[makeQuery(id+"F0.imprint","IMPRINT",EDGE,{"derivedFrom":subQ4}),1.0]])]});}
            var Q85;
            {var subQ3=sQuery(id+"F0.wireOp",EDGE,"E6.2.154");Q85=makeQuery(id+"F0.imprint","IMPRINT",FACE,{"disambiguationData":[TD([[makeQuery(id+"F0.imprint","IMPRINT",EDGE,{"derivedFrom":subQ3}),1.0]])]});}
            var Q86;
            {var subQ3=sQuery(id+"F0.wireOp",EDGE,"E6.2.204");Q86=makeQuery(id+"F0.imprint","IMPRINT",FACE,{"disambiguationData":[TD([[makeQuery(id+"F0.imprint","IMPRINT",EDGE,{"derivedFrom":subQ3}),1.0]])]});}
            var Q87;
            {var subQ4=sQuery(id+"F0.wireOp",EDGE,"E6.2.206");Q87=makeQuery(id+"F0.imprint","IMPRINT",FACE,{"disambiguationData":[TD([[makeQuery(id+"F0.imprint","IMPRINT",EDGE,{"derivedFrom":subQ4}),1.0]])]});}
            var Q88;
            {var subQ3=sQuery(id+"F0.wireOp",EDGE,"E6.3.204");Q88=makeQuery(id+"F0.imprint","IMPRINT",FACE,{"disambiguationData":[TD([[makeQuery(id+"F0.imprint","IMPRINT",EDGE,{"derivedFrom":subQ3}),1.0]])]});}
            var Q89;
            {var subQ3=sQuery(id+"F0.wireOp",EDGE,"E6.3.154");Q89=makeQuery(id+"F0.imprint","IMPRINT",FACE,{"disambiguationData":[TD([[makeQuery(id+"F0.imprint","IMPRINT",EDGE,{"derivedFrom":subQ3}),1.0]])]});}
            var Q90;
            {var subQ4=sQuery(id+"F0.wireOp",EDGE,"E6.3.200");Q90=makeQuery(id+"F0.imprint","IMPRINT",FACE,{"disambiguationData":[TD([[makeQuery(id+"F0.imprint","IMPRINT",EDGE,{"derivedFrom":subQ4}),1.0]])]});}
            var Q91;
            {var subQ0=sQuery(id+"F0.wireOp",EDGE,"E6.3.69");Q91=makeQuery(id+"F0.imprint","IMPRINT",FACE,{"disambiguationData":[TD([[makeQuery(id+"F0.imprint","IMPRINT",EDGE,{"derivedFrom":subQ0}),1.0]])]});}
            var Q92;
            {var subQ4=sQuery(id+"F0.wireOp",EDGE,"E6.3.206");Q92=makeQuery(id+"F0.imprint","IMPRINT",FACE,{"disambiguationData":[TD([[makeQuery(id+"F0.imprint","IMPRINT",EDGE,{"derivedFrom":subQ4}),1.0]])]});}
            var Q93;
            {var subQ0=sQuery(id+"F0.wireOp",EDGE,"E6.3.93");Q93=makeQuery(id+"F0.imprint","IMPRINT",FACE,{"disambiguationData":[TD([[makeQuery(id+"F0.imprint","IMPRINT",EDGE,{"derivedFrom":subQ0}),1.0]])]});}
            var Q94;
            {var subQ0=sQuery(id+"F0.wireOp",EDGE,"E6.3.92");Q94=makeQuery(id+"F0.imprint","IMPRINT",FACE,{"disambiguationData":[TD([[makeQuery(id+"F0.imprint","IMPRINT",EDGE,{"derivedFrom":subQ0}),1.0]])]});}
            var Q95;
            {var subQ4=sQuery(id+"F0.wireOp",EDGE,"E6.3.221");Q95=makeQuery(id+"F0.imprint","IMPRINT",FACE,{"disambiguationData":[TD([[makeQuery(id+"F0.imprint","IMPRINT",EDGE,{"derivedFrom":subQ4}),1.0]])]});}
            var Q96;
            {var subQ3=sQuery(id+"F0.wireOp",EDGE,"E6.3.159");Q96=makeQuery(id+"F0.imprint","IMPRINT",FACE,{"disambiguationData":[TD([[makeQuery(id+"F0.imprint","IMPRINT",EDGE,{"derivedFrom":subQ3}),1.0]])]});}
            var Q97;
            {var subQ4=sQuery(id+"F0.wireOp",EDGE,"E6.3.201");Q97=makeQuery(id+"F0.imprint","IMPRINT",FACE,{"disambiguationData":[TD([[makeQuery(id+"F0.imprint","IMPRINT",EDGE,{"derivedFrom":subQ4}),1.0]])]});}
            var Q98;
            {var subQ3=sQuery(id+"F0.wireOp",EDGE,"E6.3.166");Q98=makeQuery(id+"F0.imprint","IMPRINT",FACE,{"disambiguationData":[TD([[makeQuery(id+"F0.imprint","IMPRINT",EDGE,{"derivedFrom":subQ3}),1.0]])]});}
            var Q99;
            {var subQ4=sQuery(id+"F0.wireOp",EDGE,"E6.3.202");Q99=makeQuery(id+"F0.imprint","IMPRINT",FACE,{"disambiguationData":[TD([[makeQuery(id+"F0.imprint","IMPRINT",EDGE,{"derivedFrom":subQ4}),1.0]])]});}
            var Q100;
            {var subQ4=sQuery(id+"F0.wireOp",EDGE,"E6.1.206");Q100=makeQuery(id+"F0.imprint","IMPRINT",FACE,{"disambiguationData":[TD([[makeQuery(id+"F0.imprint","IMPRINT",EDGE,{"derivedFrom":subQ4}),1.0]])]});}
            var Q101;
            {var subQ0=sQuery(id+"F0.wireOp",EDGE,"E6.1.69");Q101=makeQuery(id+"F0.imprint","IMPRINT",FACE,{"disambiguationData":[TD([[makeQuery(id+"F0.imprint","IMPRINT",EDGE,{"derivedFrom":subQ0}),1.0]])]});}
            var Q102;
            {var subQ4=sQuery(id+"F0.wireOp",EDGE,"E6.1.200");Q102=makeQuery(id+"F0.imprint","IMPRINT",FACE,{"disambiguationData":[TD([[makeQuery(id+"F0.imprint","IMPRINT",EDGE,{"derivedFrom":subQ4}),1.0]])]});}
            var Q103;
            {var subQ3=sQuery(id+"F0.wireOp",EDGE,"E6.1.154");Q103=makeQuery(id+"F0.imprint","IMPRINT",FACE,{"disambiguationData":[TD([[makeQuery(id+"F0.imprint","IMPRINT",EDGE,{"derivedFrom":subQ3}),1.0]])]});}
            var Q104;
            {var subQ3=sQuery(id+"F0.wireOp",EDGE,"E6.1.204");Q104=makeQuery(id+"F0.imprint","IMPRINT",FACE,{"disambiguationData":[TD([[makeQuery(id+"F0.imprint","IMPRINT",EDGE,{"derivedFrom":subQ3}),1.0]])]});}
            var Q105;
            {var subQ0=sQuery(id+"F0.wireOp",EDGE,"E5.2.2");Q105=makeQuery(id+"F0.imprint","IMPRINT",FACE,{"disambiguationData":[TD([[makeQuery(id+"F0.imprint","IMPRINT",EDGE,{"derivedFrom":subQ0}),1.0]])]});}
            var Q106;
            {var subQ0=sQuery(id+"F0.wireOp",EDGE,"E5.2.1");Q106=makeQuery(id+"F0.imprint","IMPRINT",FACE,{"disambiguationData":[TD([[makeQuery(id+"F0.imprint","IMPRINT",EDGE,{"derivedFrom":subQ0}),1.0]])]});}
            var Q107;
            {var subQ3=sQuery(id+"F0.wireOp",EDGE,"E5.2.14");Q107=makeQuery(id+"F0.imprint","IMPRINT",FACE,{"disambiguationData":[TD([[makeQuery(id+"F0.imprint","IMPRINT",EDGE,{"derivedFrom":subQ3}),1.0]])]});}
            var Q108;
            {var subQ4=sQuery(id+"F0.wireOp",EDGE,"E5.1.26");Q108=makeQuery(id+"F0.imprint","IMPRINT",FACE,{"disambiguationData":[TD([[makeQuery(id+"F0.imprint","IMPRINT",EDGE,{"derivedFrom":subQ4}),1.0]])]});}
            var Q109;
            {var subQ0=sQuery(id+"F0.wireOp",EDGE,"E5.1.2");Q109=makeQuery(id+"F0.imprint","IMPRINT",FACE,{"disambiguationData":[TD([[makeQuery(id+"F0.imprint","IMPRINT",EDGE,{"derivedFrom":subQ0}),1.0]])]});}
            var Q110;
            {var subQ0=sQuery(id+"F0.wireOp",EDGE,"E5.1.1");Q110=makeQuery(id+"F0.imprint","IMPRINT",FACE,{"disambiguationData":[TD([[makeQuery(id+"F0.imprint","IMPRINT",EDGE,{"derivedFrom":subQ0}),1.0]])]});}
            var Q111;
            {var subQ3=sQuery(id+"F0.wireOp",EDGE,"E5.1.14");Q111=makeQuery(id+"F0.imprint","IMPRINT",FACE,{"disambiguationData":[TD([[makeQuery(id+"F0.imprint","IMPRINT",EDGE,{"derivedFrom":subQ3}),1.0]])]});}
            var Q112;
            {var subQ4=sQuery(id+"F0.wireOp",EDGE,"E5.1.19");Q112=makeQuery(id+"F0.imprint","IMPRINT",FACE,{"disambiguationData":[TD([[makeQuery(id+"F0.imprint","IMPRINT",EDGE,{"derivedFrom":subQ4}),1.0]])]});}
            var Q113;
            {var subQ4=sQuery(id+"F0.wireOp",EDGE,"E4.1.4");Q113=makeQuery(id+"F0.imprint","IMPRINT",FACE,{"disambiguationData":[TD([[makeQuery(id+"F0.imprint","IMPRINT",EDGE,{"derivedFrom":subQ4}),1.0]])]});}
            var Q114;
            {var subQ3=sQuery(id+"F0.wireOp",EDGE,"E3.4");Q114=makeQuery(id+"F0.imprint","IMPRINT",FACE,{"disambiguationData":[TD([[makeQuery(id+"F0.imprint","IMPRINT",EDGE,{"derivedFrom":subQ3}),1.0]])]});}
            var Q115;
            {var subQ3=sQuery(id+"F0.wireOp",EDGE,"E3.1");Q115=makeQuery(id+"F0.imprint","IMPRINT",FACE,{"disambiguationData":[TD([[makeQuery(id+"F0.imprint","IMPRINT",EDGE,{"derivedFrom":subQ3}),1.0]])]});}
            var Q116;
            {var subQ4=sQuery(id+"F0.wireOp",EDGE,"E4.3.4");Q116=makeQuery(id+"F0.imprint","IMPRINT",FACE,{"disambiguationData":[TD([[makeQuery(id+"F0.imprint","IMPRINT",EDGE,{"derivedFrom":subQ4}),1.0]])]});}
            var Q117;
            {var subQ4=sQuery(id+"F0.wireOp",EDGE,"E4.2.4");Q117=makeQuery(id+"F0.imprint","IMPRINT",FACE,{"disambiguationData":[TD([[makeQuery(id+"F0.imprint","IMPRINT",EDGE,{"derivedFrom":subQ4}),1.0]])]});}
            var Q118;
            {var subQ4=sQuery(id+"F0.wireOp",EDGE,"E5.4.26");Q118=makeQuery(id+"F0.imprint","IMPRINT",FACE,{"disambiguationData":[TD([[makeQuery(id+"F0.imprint","IMPRINT",EDGE,{"derivedFrom":subQ4}),1.0]])]});}
            var Q119;
            {var subQ0=sQuery(id+"F0.wireOp",EDGE,"E5.4.2");Q119=makeQuery(id+"F0.imprint","IMPRINT",FACE,{"disambiguationData":[TD([[makeQuery(id+"F0.imprint","IMPRINT",EDGE,{"derivedFrom":subQ0}),1.0]])]});}
            var Q120;
            {var subQ0=sQuery(id+"F0.wireOp",EDGE,"E5.4.1");Q120=makeQuery(id+"F0.imprint","IMPRINT",FACE,{"disambiguationData":[TD([[makeQuery(id+"F0.imprint","IMPRINT",EDGE,{"derivedFrom":subQ0}),1.0]])]});}
            var Q121;
            {var subQ3=sQuery(id+"F0.wireOp",EDGE,"E5.4.14");Q121=makeQuery(id+"F0.imprint","IMPRINT",FACE,{"disambiguationData":[TD([[makeQuery(id+"F0.imprint","IMPRINT",EDGE,{"derivedFrom":subQ3}),1.0]])]});}
            var Q122;
            {var subQ4=sQuery(id+"F0.wireOp",EDGE,"E5.4.19");Q122=makeQuery(id+"F0.imprint","IMPRINT",FACE,{"disambiguationData":[TD([[makeQuery(id+"F0.imprint","IMPRINT",EDGE,{"derivedFrom":subQ4}),1.0]])]});}
            var Q123;
            {var subQ4=sQuery(id+"F0.wireOp",EDGE,"E5.3.26");Q123=makeQuery(id+"F0.imprint","IMPRINT",FACE,{"disambiguationData":[TD([[makeQuery(id+"F0.imprint","IMPRINT",EDGE,{"derivedFrom":subQ4}),1.0]])]});}
            var Q124;
            {var subQ0=sQuery(id+"F0.wireOp",EDGE,"E5.3.2");Q124=makeQuery(id+"F0.imprint","IMPRINT",FACE,{"disambiguationData":[TD([[makeQuery(id+"F0.imprint","IMPRINT",EDGE,{"derivedFrom":subQ0}),1.0]])]});}
            var Q125;
            {var subQ0=sQuery(id+"F0.wireOp",EDGE,"E5.3.1");Q125=makeQuery(id+"F0.imprint","IMPRINT",FACE,{"disambiguationData":[TD([[makeQuery(id+"F0.imprint","IMPRINT",EDGE,{"derivedFrom":subQ0}),1.0]])]});}
            var Q126;
            {var subQ3=sQuery(id+"F0.wireOp",EDGE,"E5.3.14");Q126=makeQuery(id+"F0.imprint","IMPRINT",FACE,{"disambiguationData":[TD([[makeQuery(id+"F0.imprint","IMPRINT",EDGE,{"derivedFrom":subQ3}),1.0]])]});}
            var Q127;
            {var subQ4=sQuery(id+"F0.wireOp",EDGE,"E5.3.19");Q127=makeQuery(id+"F0.imprint","IMPRINT",FACE,{"disambiguationData":[TD([[makeQuery(id+"F0.imprint","IMPRINT",EDGE,{"derivedFrom":subQ4}),1.0]])]});}
            var Q128;
            {var subQ4=sQuery(id+"F0.wireOp",EDGE,"E5.2.26");Q128=makeQuery(id+"F0.imprint","IMPRINT",FACE,{"disambiguationData":[TD([[makeQuery(id+"F0.imprint","IMPRINT",EDGE,{"derivedFrom":subQ4}),1.0]])]});}
            var Q129;
            {var subQ4=sQuery(id+"F0.wireOp",EDGE,"E5.2.19");Q129=makeQuery(id+"F0.imprint","IMPRINT",FACE,{"disambiguationData":[TD([[makeQuery(id+"F0.imprint","IMPRINT",EDGE,{"derivedFrom":subQ4}),1.0]])]});}
            var Q130;
            {var subQ3=sQuery(id+"F0.wireOp",EDGE,"E6.4.210");Q130=makeQuery(id+"F0.imprint","IMPRINT",FACE,{"disambiguationData":[TD([[makeQuery(id+"F0.imprint","IMPRINT",EDGE,{"derivedFrom":subQ3}),1.0]])]});}
            var Q131;
            {var subQ0=sQuery(id+"F0.wireOp",EDGE,"E6.4.99");Q131=makeQuery(id+"F0.imprint","IMPRINT",FACE,{"disambiguationData":[TD([[makeQuery(id+"F0.imprint","IMPRINT",EDGE,{"derivedFrom":subQ0}),1.0]])]});}
            var Q132;
            {var subQ4=sQuery(id+"F0.wireOp",EDGE,"E6.4.200");Q132=makeQuery(id+"F0.imprint","IMPRINT",FACE,{"disambiguationData":[TD([[makeQuery(id+"F0.imprint","IMPRINT",EDGE,{"derivedFrom":subQ4}),1.0]])]});}
            var Q133;
            {var subQ0=sQuery(id+"F0.wireOp",EDGE,"E6.4.93");Q133=makeQuery(id+"F0.imprint","IMPRINT",FACE,{"disambiguationData":[TD([[makeQuery(id+"F0.imprint","IMPRINT",EDGE,{"derivedFrom":subQ0}),1.0]])]});}
            var Q134;
            {var subQ3=sQuery(id+"F0.wireOp",EDGE,"E6.4.135");Q134=makeQuery(id+"F0.imprint","IMPRINT",FACE,{"disambiguationData":[TD([[makeQuery(id+"F0.imprint","IMPRINT",EDGE,{"derivedFrom":subQ3}),1.0]])]});}
            var Q135;
            {var subQ0=sQuery(id+"F0.wireOp",EDGE,"E6.4.82");Q135=makeQuery(id+"F0.imprint","IMPRINT",FACE,{"disambiguationData":[TD([[makeQuery(id+"F0.imprint","IMPRINT",EDGE,{"derivedFrom":subQ0}),1.0]])]});}
            var Q136;
            {var subQ4=sQuery(id+"F0.wireOp",EDGE,"E6.4.212");Q136=makeQuery(id+"F0.imprint","IMPRINT",FACE,{"disambiguationData":[TD([[makeQuery(id+"F0.imprint","IMPRINT",EDGE,{"derivedFrom":subQ4}),1.0]])]});}
            var Q137;
            {var subQ3=sQuery(id+"F0.wireOp",EDGE,"E6.4.130");Q137=makeQuery(id+"F0.imprint","IMPRINT",FACE,{"disambiguationData":[TD([[makeQuery(id+"F0.imprint","IMPRINT",EDGE,{"derivedFrom":subQ3}),1.0]])]});}
            var Q138;
            {var subQ3=sQuery(id+"F0.wireOp",EDGE,"E6.4.218");Q138=makeQuery(id+"F0.imprint","IMPRINT",FACE,{"disambiguationData":[TD([[makeQuery(id+"F0.imprint","IMPRINT",EDGE,{"derivedFrom":subQ3}),1.0]])]});}
            var Q139;
            {var subQ3=sQuery(id+"F0.wireOp",EDGE,"E6.4.154");Q139=makeQuery(id+"F0.imprint","IMPRINT",FACE,{"disambiguationData":[TD([[makeQuery(id+"F0.imprint","IMPRINT",EDGE,{"derivedFrom":subQ3}),1.0]])]});}
            var Q140;
            {var subQ3=sQuery(id+"F0.wireOp",EDGE,"E6.4.204");Q140=makeQuery(id+"F0.imprint","IMPRINT",FACE,{"disambiguationData":[TD([[makeQuery(id+"F0.imprint","IMPRINT",EDGE,{"derivedFrom":subQ3}),1.0]])]});}
            var Q141;
            {var subQ0=sQuery(id+"F0.wireOp",EDGE,"E6.4.84");Q141=makeQuery(id+"F0.imprint","IMPRINT",FACE,{"disambiguationData":[TD([[makeQuery(id+"F0.imprint","IMPRINT",EDGE,{"derivedFrom":subQ0}),1.0]])]});}
            var Q142;
            {var subQ3=sQuery(id+"F0.wireOp",EDGE,"E6.4.217");Q142=makeQuery(id+"F0.imprint","IMPRINT",FACE,{"disambiguationData":[TD([[makeQuery(id+"F0.imprint","IMPRINT",EDGE,{"derivedFrom":subQ3}),1.0]])]});}
            var Q143;
            {var subQ4=sQuery(id+"F0.wireOp",EDGE,"E6.4.216");Q143=makeQuery(id+"F0.imprint","IMPRINT",FACE,{"disambiguationData":[TD([[makeQuery(id+"F0.imprint","IMPRINT",EDGE,{"derivedFrom":subQ4}),1.0]])]});}
            var Q144;
            {var subQ3=sQuery(id+"F0.wireOp",EDGE,"E6.4.224");Q144=makeQuery(id+"F0.imprint","IMPRINT",FACE,{"disambiguationData":[TD([[makeQuery(id+"F0.imprint","IMPRINT",EDGE,{"derivedFrom":subQ3}),1.0]])]});}
            var Q145;
            {var subQ3=sQuery(id+"F0.wireOp",EDGE,"E6.4.166");Q145=makeQuery(id+"F0.imprint","IMPRINT",FACE,{"disambiguationData":[TD([[makeQuery(id+"F0.imprint","IMPRINT",EDGE,{"derivedFrom":subQ3}),1.0]])]});}
            var Q146;
            {var subQ4=sQuery(id+"F0.wireOp",EDGE,"E6.4.206");Q146=makeQuery(id+"F0.imprint","IMPRINT",FACE,{"disambiguationData":[TD([[makeQuery(id+"F0.imprint","IMPRINT",EDGE,{"derivedFrom":subQ4}),1.0]])]});}
            var Q147;
            {var subQ4=sQuery(id+"F0.wireOp",EDGE,"E6.4.150");Q147=makeQuery(id+"F0.imprint","IMPRINT",FACE,{"disambiguationData":[TD([[makeQuery(id+"F0.imprint","IMPRINT",EDGE,{"derivedFrom":subQ4}),1.0]])]});}
            var Q148;
            {var subQ4=sQuery(id+"F0.wireOp",EDGE,"E6.4.234");Q148=makeQuery(id+"F0.imprint","IMPRINT",FACE,{"disambiguationData":[TD([[makeQuery(id+"F0.imprint","IMPRINT",EDGE,{"derivedFrom":subQ4}),1.0]])]});}
            var Q149;
            {var subQ4=sQuery(id+"F0.wireOp",EDGE,"E6.4.202");Q149=makeQuery(id+"F0.imprint","IMPRINT",FACE,{"disambiguationData":[TD([[makeQuery(id+"F0.imprint","IMPRINT",EDGE,{"derivedFrom":subQ4}),1.0]])]});}
            var Q150;
            {var subQ3=sQuery(id+"F0.wireOp",EDGE,"E6.4.159");Q150=makeQuery(id+"F0.imprint","IMPRINT",FACE,{"disambiguationData":[TD([[makeQuery(id+"F0.imprint","IMPRINT",EDGE,{"derivedFrom":subQ3}),1.0]])]});}
            var Q151;
            {var subQ4=sQuery(id+"F0.wireOp",EDGE,"E6.4.221");Q151=makeQuery(id+"F0.imprint","IMPRINT",FACE,{"disambiguationData":[TD([[makeQuery(id+"F0.imprint","IMPRINT",EDGE,{"derivedFrom":subQ4}),1.0]])]});}
            var Q152;
            {var subQ0=sQuery(id+"F0.wireOp",EDGE,"E6.4.92");Q152=makeQuery(id+"F0.imprint","IMPRINT",FACE,{"disambiguationData":[TD([[makeQuery(id+"F0.imprint","IMPRINT",EDGE,{"derivedFrom":subQ0}),1.0]])]});}
            var Q153;
            {var subQ0=sQuery(id+"F0.wireOp",EDGE,"E6.4.69");Q153=makeQuery(id+"F0.imprint","IMPRINT",FACE,{"disambiguationData":[TD([[makeQuery(id+"F0.imprint","IMPRINT",EDGE,{"derivedFrom":subQ0}),1.0]])]});}
            var Q154;
            {var subQ4=sQuery(id+"F0.wireOp",EDGE,"E6.4.201");Q154=makeQuery(id+"F0.imprint","IMPRINT",FACE,{"disambiguationData":[TD([[makeQuery(id+"F0.imprint","IMPRINT",EDGE,{"derivedFrom":subQ4}),1.0]])]});}
            extrude(context, id + "F1", {"entities" : qUnion([Q0, Q1, Q2, Q3, Q4, Q5, Q6, Q7, Q8, Q9, Q10, Q11, Q12, Q13, Q14, Q15, Q16, Q17, Q18, Q19, Q20, Q21, Q22, Q23, Q24, Q25, Q26, Q27, Q28, Q29, Q30, Q31, Q32, Q33, Q34, Q35, Q36, Q37, Q38, Q39, Q40, Q41, Q42, Q43, Q44, Q45, Q46, Q47, Q48, Q49, Q50, Q51, Q52, Q53, Q54, Q55, Q56, Q57, Q58, Q59, Q60, Q61, Q62, Q63, Q64, Q65, Q66, Q67, Q68, Q69, Q70, Q71, Q72, Q73, Q74, Q75, Q76, Q77, Q78, Q79, Q80, Q81, Q82, Q83, Q84, Q85, Q86, Q87, Q88, Q89, Q90, Q91, Q92, Q93, Q94, Q95, Q96, Q97, Q98, Q99, Q100, Q101, Q102, Q103, Q104, Q105, Q106, Q107, Q108, Q109, Q110, Q111, Q112, Q113, Q114, Q115, Q116, Q117, Q118, Q119, Q120, Q121, Q122, Q123, Q124, Q125, Q126, Q127, Q128, Q129, Q130, Q131, Q132, Q133, Q134, Q135, Q136, Q137, Q138, Q139, Q140, Q141, Q142, Q143, Q144, Q145, Q146, Q147, Q148, Q149, Q150, Q151, Q152, Q153, Q154]), "depth" : 25.4 * mm, "offsetDistance" : 25.4 * mm});
        }
    });
